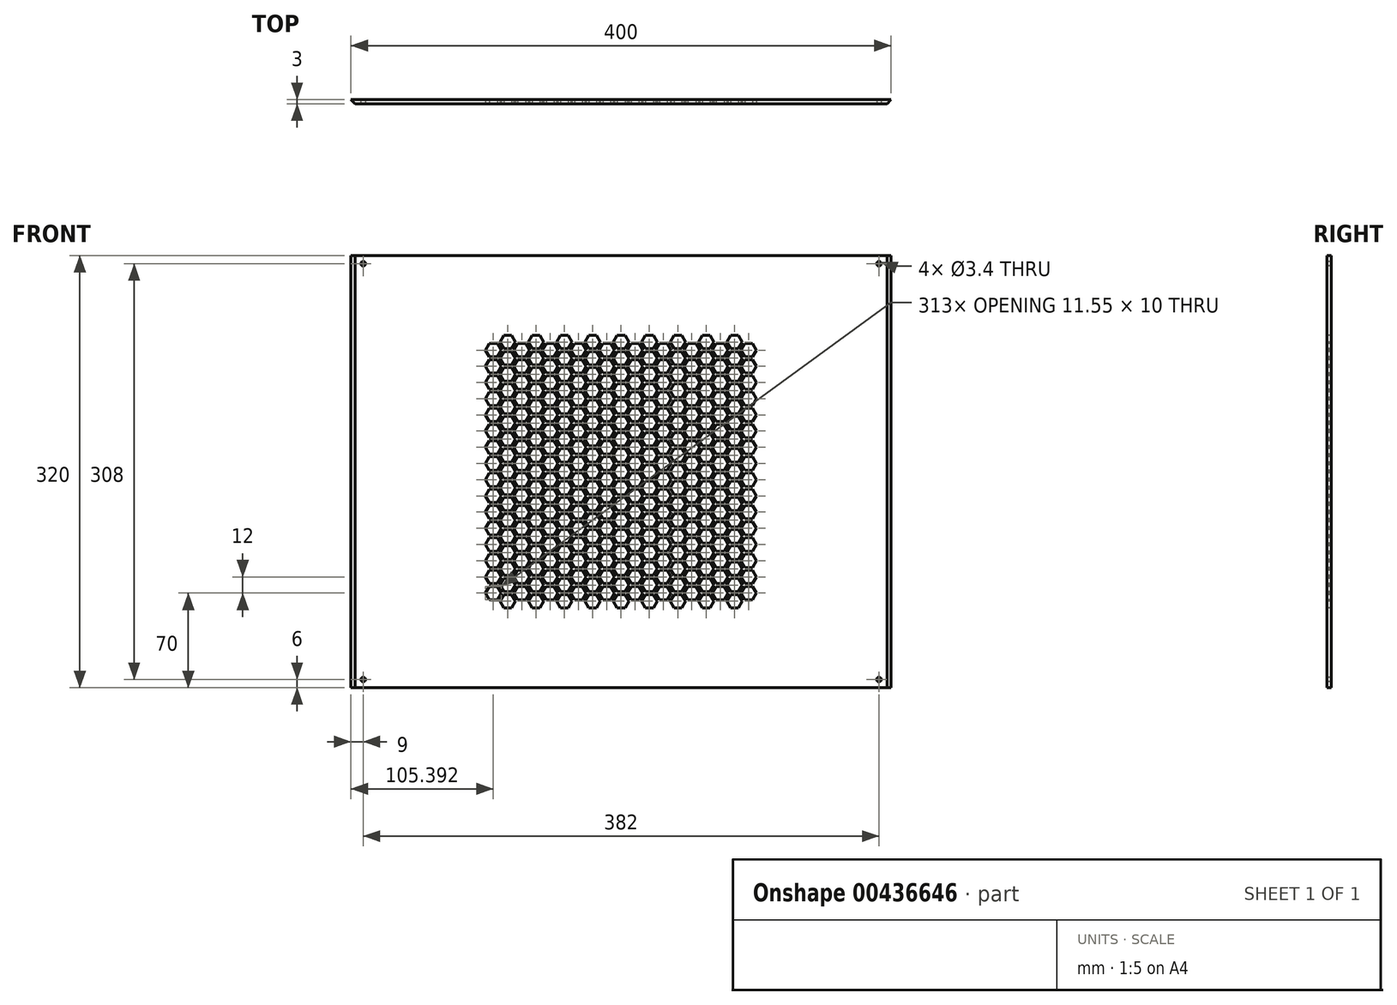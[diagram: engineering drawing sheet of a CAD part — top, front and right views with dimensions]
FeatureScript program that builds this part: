
annotation { "Feature Type Name" : "Feature", "Feature Type Description" : "" }
export const myFeature = defineFeature(function(context is Context, id is Id, definition is map)
    precondition{}
    {
        {
            var Q0;
            Q0=qCreatedBy(makeId("Top.planeOp"),FACE);
            var sketch = newSketch(context, id + "F0", { "sketchPlane" : qUnion([Q0])});
            skLineSegment(sketch, "E0", {"start": v(0, 0) * mm, "end": v(0, 1.5) * mm, "construction": true});
            skLineSegment(sketch, "E1", {"start": v(0, 0) * mm, "end": v(0, -1.5) * mm, "construction": true});
            skLineSegment(sketch, "E2", {"start": v(0, 1.5) * mm, "end": v(-200, 1.5) * mm});
            skLineSegment(sketch, "E3", {"start": v(0, 1.5) * mm, "end": v(200, 1.5) * mm});
            skLineSegment(sketch, "E4", {"start": v(0, -1.5) * mm, "end": v(-197, -1.5) * mm});
            skLineSegment(sketch, "E5", {"start": v(0, -1.5) * mm, "end": v(197, -1.5) * mm});
            skLineSegment(sketch, "E6", {"start": v(-197, -1.5) * mm, "end": v(-200, 1.5) * mm});
            skLineSegment(sketch, "E7", {"start": v(197, -1.5) * mm, "end": v(200, 1.5) * mm});
            skLineSegment(sketch, "E8", {"start": v(0, 0) * mm, "end": v(140, 0) * mm, "construction": true});
            skLineSegment(sketch, "E9", {"start": v(0, 0) * mm, "end": v(-140, 0) * mm, "construction": true});
            skLineSegment(sketch, "E10", {"start": v(140, 0) * mm, "end": v(140, 1.5) * mm});
            skLineSegment(sketch, "E11", {"start": v(140, 0) * mm, "end": v(140, -1.5) * mm});
            skLineSegment(sketch, "E12", {"start": v(-140, 0) * mm, "end": v(-140, 1.5) * mm});
            skLineSegment(sketch, "E13", {"start": v(-140, 0) * mm, "end": v(-140, -1.5) * mm});
            skSolve(sketch);
        }
        {
            var Q0;
            {var subQ8=sQuery(id+"F0.wireOp",EDGE,"E10");Q0=makeQuery(id+"F0.imprint","IMPRINT",FACE,{"disambiguationData":[TD([[makeQuery(id+"F0.imprint","IMPRINT",EDGE,{"derivedFrom":subQ8}),1.0]])]});}
            extrude(context, id + "F1", {"entities" : qUnion([Q0]), "oppositeDirection" : true, "depth" : 320 * mm});
        }
        {
            var Q0;
            {var subQ1=sQuery(id+"F0.wireOp",EDGE,"E6");Q0=makeQuery(id+"F0.imprint","IMPRINT",FACE,{"disambiguationData":[TD([[makeQuery(id+"F0.imprint","IMPRINT",EDGE,{"derivedFrom":subQ1}),-1.0]])]});}
            var Q1;
            {var subQ1=sQuery(id+"F0.wireOp",EDGE,"E7");Q1=makeQuery(id+"F0.imprint","IMPRINT",FACE,{"disambiguationData":[TD([[makeQuery(id+"F0.imprint","IMPRINT",EDGE,{"derivedFrom":subQ1}),1.0]])]});}
            extrude(context, id + "F2", {"entities" : qUnion([Q0, Q1]), "operationType" : NewBodyOperationType.ADD, "oppositeDirection" : true, "depth" : 320 * mm});
        }
        {
            var Q0;
            {var subQ0=sQuery(id+"F0.wireOp",EDGE,"E5");var subQ1=sQuery(id+"F0.wireOp",EDGE,"E4");Q0=makeQuery(id+"F2.boolean.opBoolean","MERGE",FACE,{"derivedFrom":[makeQuery(id+"F1.opExtrude","SWEPT_FACE",FACE,{"disambiguationData":[OSD([subQ1,subQ0])]}),makeQuery(id+"F2.opExtrude","SWEPT_FACE",FACE,{"disambiguationData":[OSD([subQ1])]}),makeQuery(id+"F2.opExtrude","SWEPT_FACE",FACE,{"disambiguationData":[OSD([subQ0])]})]});}
            var sketch = newSketch(context, id + "F3", { "sketchPlane" : qUnion([Q0])});
            skLineSegment(sketch, "E14", {"start": v(0, 0) * mm, "end": v(-191, 0) * mm, "construction": true});
            skLineSegment(sketch, "E15", {"start": v(-191, 0) * mm, "end": v(-191, -6) * mm, "construction": true});
            skCircle(sketch, "E16", {"center": v(-191, -6) * mm, "radius": 1.7 * mm});
            skLineSegment(sketch, "E17", {"start": v(-191, -6) * mm, "end": v(-191, -314) * mm, "construction": true});
            skCircle(sketch, "E18", {"center": v(-191, -314) * mm, "radius": 1.7 * mm});
            skLineSegment(sketch, "E19", {"start": v(0, 0) * mm, "end": v(191, 0) * mm, "construction": true});
            skLineSegment(sketch, "E20", {"start": v(191, 0) * mm, "end": v(191, -6) * mm, "construction": true});
            skLineSegment(sketch, "E21", {"start": v(191, -6) * mm, "end": v(191, -314) * mm, "construction": true});
            skCircle(sketch, "E22", {"center": v(191, -6) * mm, "radius": 1.7 * mm});
            skCircle(sketch, "E23", {"center": v(191, -314) * mm, "radius": 1.7 * mm});
            skSolve(sketch);
        }
        {
            var Q0;
            Q0=makeQuery(id+"F3.imprint","IMPRINT",FACE,{"disambiguationData":[TD([[makeQuery(id+"F3.imprint","IMPRINT",EDGE,{"derivedFrom":sQuery(id+"F3.wireOp",EDGE,"E22")}),1.0]])]});
            var Q1;
            Q1=makeQuery(id+"F3.imprint","IMPRINT",FACE,{"disambiguationData":[TD([[makeQuery(id+"F3.imprint","IMPRINT",EDGE,{"derivedFrom":sQuery(id+"F3.wireOp",EDGE,"E23")}),1.0]])]});
            var Q2;
            Q2=makeQuery(id+"F3.imprint","IMPRINT",FACE,{"disambiguationData":[TD([[makeQuery(id+"F3.imprint","IMPRINT",EDGE,{"derivedFrom":sQuery(id+"F3.wireOp",EDGE,"E18")}),1.0]])]});
            var Q3;
            Q3=makeQuery(id+"F3.imprint","IMPRINT",FACE,{"disambiguationData":[TD([[makeQuery(id+"F3.imprint","IMPRINT",EDGE,{"derivedFrom":sQuery(id+"F3.wireOp",EDGE,"E16")}),1.0]])]});
            extrude(context, id + "F4", {"entities" : qUnion([Q0, Q1, Q2, Q3]), "operationType" : NewBodyOperationType.REMOVE, "oppositeDirection" : true, "depth" : 3 * mm});
        }
        {
            var Q0;
            {var subQ0=sQuery(id+"F0.wireOp",EDGE,"E5");var subQ1=sQuery(id+"F0.wireOp",EDGE,"E4");Q0=makeQuery(id+"F2.boolean.opBoolean","MERGE",FACE,{"derivedFrom":[makeQuery(id+"F1.opExtrude","SWEPT_FACE",FACE,{"disambiguationData":[OSD([subQ1,subQ0])]}),makeQuery(id+"F2.opExtrude","SWEPT_FACE",FACE,{"disambiguationData":[OSD([subQ1])]}),makeQuery(id+"F2.opExtrude","SWEPT_FACE",FACE,{"disambiguationData":[OSD([subQ0])]})]});}
            var sketch = newSketch(context, id + "F5", { "sketchPlane" : qUnion([Q0])});
            skLineSegment(sketch, "E24", {"start": v(0, 0) * mm, "end": v(0, -160) * mm, "construction": true});
            skPoint(sketch, "E24.endSnap0", {"position": v(0, -320) * mm});
            skLineSegment(sketch, "E25.bottom", {"start": v(100, -260) * mm, "end": v(-100, -260) * mm, "construction": true});
            skLineSegment(sketch, "E25.top", {"start": v(100, -60) * mm, "end": v(-100, -60) * mm, "construction": true});
            skLineSegment(sketch, "E25.left", {"start": v(100, -260) * mm, "end": v(100, -60) * mm, "construction": true});
            skLineSegment(sketch, "E25.right", {"start": v(-100, -260) * mm, "end": v(-100, -60) * mm, "construction": true});
            skLineSegment(sketch, "E26", {"start": v(0, 0) * mm, "end": v(84, 0) * mm, "construction": true});
            skLineSegment(sketch, "E27", {"start": v(84, 0) * mm, "end": v(84, -64) * mm, "construction": true});
            skCircle(sketch, "E28.cCircle", {"center": v(84, -64) * mm, "radius": 5 * mm, "construction": true});
            skLineSegment(sketch, "E28.0", {"start": v(81.11, -59) * mm, "end": v(86.89, -59) * mm});
            skLineSegment(sketch, "E28.1", {"start": v(86.89, -59) * mm, "end": v(89.77, -64) * mm});
            skLineSegment(sketch, "E28.2", {"start": v(89.77, -64) * mm, "end": v(86.89, -69) * mm});
            skLineSegment(sketch, "E28.3", {"start": v(86.89, -69) * mm, "end": v(81.11, -69) * mm});
            skLineSegment(sketch, "E28.4", {"start": v(81.11, -69) * mm, "end": v(78.23, -64) * mm});
            skLineSegment(sketch, "E28.5", {"start": v(78.23, -64) * mm, "end": v(81.11, -59) * mm});
            skPoint(sketch, "E28.0.midPoint", {"position": v(84, -59) * mm});
            skLineSegment(sketch, "E29", {"start": v(84, -64) * mm, "end": v(94.4, -70) * mm, "construction": true});
            skCircle(sketch, "E30.cCircle", {"center": v(94.4, -70) * mm, "radius": 5 * mm, "construction": true});
            skLineSegment(sketch, "E30.0", {"start": v(91.5, -65) * mm, "end": v(97.28, -65) * mm});
            skLineSegment(sketch, "E30.1", {"start": v(97.28, -65) * mm, "end": v(100.17, -70) * mm});
            skLineSegment(sketch, "E30.2", {"start": v(100.17, -70) * mm, "end": v(97.28, -75) * mm});
            skLineSegment(sketch, "E30.3", {"start": v(97.28, -75) * mm, "end": v(91.5, -75) * mm});
            skLineSegment(sketch, "E30.4", {"start": v(91.5, -75) * mm, "end": v(88.62, -70) * mm});
            skLineSegment(sketch, "E30.5", {"start": v(88.62, -70) * mm, "end": v(91.5, -65) * mm});
            skPoint(sketch, "E30.0.midPoint", {"position": v(94.4, -65) * mm});
            skLineSegment(sketch, "E31.0.1.0", {"start": v(97.28, -77) * mm, "end": v(100.17, -82) * mm});
            skLineSegment(sketch, "E31.0.1.1", {"start": v(91.5, -87) * mm, "end": v(88.62, -82) * mm});
            skLineSegment(sketch, "E31.0.1.2", {"start": v(88.62, -82) * mm, "end": v(91.5, -77) * mm});
            skLineSegment(sketch, "E31.0.1.3", {"start": v(89.77, -76) * mm, "end": v(86.89, -81) * mm});
            skLineSegment(sketch, "E31.0.1.4", {"start": v(100.17, -82) * mm, "end": v(97.28, -87) * mm});
            skPoint(sketch, "E31.0.1.5", {"position": v(94.4, -77) * mm});
            skLineSegment(sketch, "E31.0.1.6", {"start": v(86.89, -71) * mm, "end": v(89.77, -76) * mm});
            skLineSegment(sketch, "E31.0.1.7", {"start": v(81.11, -71) * mm, "end": v(86.89, -71) * mm});
            skPoint(sketch, "E31.0.1.8", {"position": v(84, -71) * mm});
            skLineSegment(sketch, "E31.0.1.9", {"start": v(86.89, -81) * mm, "end": v(81.11, -81) * mm});
            skLineSegment(sketch, "E31.0.1.10", {"start": v(81.11, -81) * mm, "end": v(78.23, -76) * mm});
            skLineSegment(sketch, "E31.0.1.11", {"start": v(78.23, -76) * mm, "end": v(81.11, -71) * mm});
            skLineSegment(sketch, "E31.0.1.12", {"start": v(91.5, -77) * mm, "end": v(97.28, -77) * mm});
            skLineSegment(sketch, "E31.0.1.13", {"start": v(97.28, -87) * mm, "end": v(91.5, -87) * mm});
            skLineSegment(sketch, "E31.0.2.0", {"start": v(97.28, -89) * mm, "end": v(100.17, -94) * mm});
            skLineSegment(sketch, "E31.0.2.1", {"start": v(91.5, -99) * mm, "end": v(88.62, -94) * mm});
            skLineSegment(sketch, "E31.0.2.2", {"start": v(88.62, -94) * mm, "end": v(91.5, -89) * mm});
            skLineSegment(sketch, "E31.0.2.3", {"start": v(89.77, -88) * mm, "end": v(86.89, -93) * mm});
            skLineSegment(sketch, "E31.0.2.4", {"start": v(100.17, -94) * mm, "end": v(97.28, -99) * mm});
            skPoint(sketch, "E31.0.2.5", {"position": v(94.4, -89) * mm});
            skLineSegment(sketch, "E31.0.2.6", {"start": v(86.89, -83) * mm, "end": v(89.77, -88) * mm});
            skLineSegment(sketch, "E31.0.2.7", {"start": v(81.11, -83) * mm, "end": v(86.89, -83) * mm});
            skPoint(sketch, "E31.0.2.8", {"position": v(84, -83) * mm});
            skLineSegment(sketch, "E31.0.2.9", {"start": v(86.89, -93) * mm, "end": v(81.11, -93) * mm});
            skLineSegment(sketch, "E31.0.2.10", {"start": v(81.11, -93) * mm, "end": v(78.23, -88) * mm});
            skLineSegment(sketch, "E31.0.2.11", {"start": v(78.23, -88) * mm, "end": v(81.11, -83) * mm});
            skLineSegment(sketch, "E31.0.2.12", {"start": v(91.5, -89) * mm, "end": v(97.28, -89) * mm});
            skLineSegment(sketch, "E31.0.2.13", {"start": v(97.28, -99) * mm, "end": v(91.5, -99) * mm});
            skLineSegment(sketch, "E31.0.3.0", {"start": v(97.28, -101) * mm, "end": v(100.17, -106) * mm});
            skLineSegment(sketch, "E31.0.3.1", {"start": v(91.5, -111) * mm, "end": v(88.62, -106) * mm});
            skLineSegment(sketch, "E31.0.3.2", {"start": v(88.62, -106) * mm, "end": v(91.5, -101) * mm});
            skLineSegment(sketch, "E31.0.3.3", {"start": v(89.77, -100) * mm, "end": v(86.89, -105) * mm});
            skLineSegment(sketch, "E31.0.3.4", {"start": v(100.17, -106) * mm, "end": v(97.28, -111) * mm});
            skPoint(sketch, "E31.0.3.5", {"position": v(94.4, -101) * mm});
            skLineSegment(sketch, "E31.0.3.6", {"start": v(86.89, -95) * mm, "end": v(89.77, -100) * mm});
            skLineSegment(sketch, "E31.0.3.7", {"start": v(81.11, -95) * mm, "end": v(86.89, -95) * mm});
            skPoint(sketch, "E31.0.3.8", {"position": v(84, -95) * mm});
            skLineSegment(sketch, "E31.0.3.9", {"start": v(86.89, -105) * mm, "end": v(81.11, -105) * mm});
            skLineSegment(sketch, "E31.0.3.10", {"start": v(81.11, -105) * mm, "end": v(78.23, -100) * mm});
            skLineSegment(sketch, "E31.0.3.11", {"start": v(78.23, -100) * mm, "end": v(81.11, -95) * mm});
            skLineSegment(sketch, "E31.0.3.12", {"start": v(91.5, -101) * mm, "end": v(97.28, -101) * mm});
            skLineSegment(sketch, "E31.0.3.13", {"start": v(97.28, -111) * mm, "end": v(91.5, -111) * mm});
            skLineSegment(sketch, "E31.0.4.0", {"start": v(97.28, -113) * mm, "end": v(100.17, -118) * mm});
            skLineSegment(sketch, "E31.0.4.1", {"start": v(91.5, -123) * mm, "end": v(88.62, -118) * mm});
            skLineSegment(sketch, "E31.0.4.2", {"start": v(88.62, -118) * mm, "end": v(91.5, -113) * mm});
            skLineSegment(sketch, "E31.0.4.3", {"start": v(89.77, -112) * mm, "end": v(86.89, -117) * mm});
            skLineSegment(sketch, "E31.0.4.4", {"start": v(100.17, -118) * mm, "end": v(97.28, -123) * mm});
            skPoint(sketch, "E31.0.4.5", {"position": v(94.4, -113) * mm});
            skLineSegment(sketch, "E31.0.4.6", {"start": v(86.89, -107) * mm, "end": v(89.77, -112) * mm});
            skLineSegment(sketch, "E31.0.4.7", {"start": v(81.11, -107) * mm, "end": v(86.89, -107) * mm});
            skPoint(sketch, "E31.0.4.8", {"position": v(84, -107) * mm});
            skLineSegment(sketch, "E31.0.4.9", {"start": v(86.89, -117) * mm, "end": v(81.11, -117) * mm});
            skLineSegment(sketch, "E31.0.4.10", {"start": v(81.11, -117) * mm, "end": v(78.23, -112) * mm});
            skLineSegment(sketch, "E31.0.4.11", {"start": v(78.23, -112) * mm, "end": v(81.11, -107) * mm});
            skLineSegment(sketch, "E31.0.4.12", {"start": v(91.5, -113) * mm, "end": v(97.28, -113) * mm});
            skLineSegment(sketch, "E31.0.4.13", {"start": v(97.28, -123) * mm, "end": v(91.5, -123) * mm});
            skLineSegment(sketch, "E31.0.5.0", {"start": v(97.28, -125) * mm, "end": v(100.17, -130) * mm});
            skLineSegment(sketch, "E31.0.5.1", {"start": v(91.5, -135) * mm, "end": v(88.62, -130) * mm});
            skLineSegment(sketch, "E31.0.5.2", {"start": v(88.62, -130) * mm, "end": v(91.5, -125) * mm});
            skLineSegment(sketch, "E31.0.5.3", {"start": v(89.77, -124) * mm, "end": v(86.89, -129) * mm});
            skLineSegment(sketch, "E31.0.5.4", {"start": v(100.17, -130) * mm, "end": v(97.28, -135) * mm});
            skPoint(sketch, "E31.0.5.5", {"position": v(94.4, -125) * mm});
            skLineSegment(sketch, "E31.0.5.6", {"start": v(86.89, -119) * mm, "end": v(89.77, -124) * mm});
            skLineSegment(sketch, "E31.0.5.7", {"start": v(81.11, -119) * mm, "end": v(86.89, -119) * mm});
            skPoint(sketch, "E31.0.5.8", {"position": v(84, -119) * mm});
            skLineSegment(sketch, "E31.0.5.9", {"start": v(86.89, -129) * mm, "end": v(81.11, -129) * mm});
            skLineSegment(sketch, "E31.0.5.10", {"start": v(81.11, -129) * mm, "end": v(78.23, -124) * mm});
            skLineSegment(sketch, "E31.0.5.11", {"start": v(78.23, -124) * mm, "end": v(81.11, -119) * mm});
            skLineSegment(sketch, "E31.0.5.12", {"start": v(91.5, -125) * mm, "end": v(97.28, -125) * mm});
            skLineSegment(sketch, "E31.0.5.13", {"start": v(97.28, -135) * mm, "end": v(91.5, -135) * mm});
            skLineSegment(sketch, "E31.0.6.0", {"start": v(97.28, -137) * mm, "end": v(100.17, -142) * mm});
            skLineSegment(sketch, "E31.0.6.1", {"start": v(91.5, -147) * mm, "end": v(88.62, -142) * mm});
            skLineSegment(sketch, "E31.0.6.2", {"start": v(88.62, -142) * mm, "end": v(91.5, -137) * mm});
            skLineSegment(sketch, "E31.0.6.3", {"start": v(89.77, -136) * mm, "end": v(86.89, -141) * mm});
            skLineSegment(sketch, "E31.0.6.4", {"start": v(100.17, -142) * mm, "end": v(97.28, -147) * mm});
            skPoint(sketch, "E31.0.6.5", {"position": v(94.4, -137) * mm});
            skLineSegment(sketch, "E31.0.6.6", {"start": v(86.89, -131) * mm, "end": v(89.77, -136) * mm});
            skLineSegment(sketch, "E31.0.6.7", {"start": v(81.11, -131) * mm, "end": v(86.89, -131) * mm});
            skPoint(sketch, "E31.0.6.8", {"position": v(84, -131) * mm});
            skLineSegment(sketch, "E31.0.6.9", {"start": v(86.89, -141) * mm, "end": v(81.11, -141) * mm});
            skLineSegment(sketch, "E31.0.6.10", {"start": v(81.11, -141) * mm, "end": v(78.23, -136) * mm});
            skLineSegment(sketch, "E31.0.6.11", {"start": v(78.23, -136) * mm, "end": v(81.11, -131) * mm});
            skLineSegment(sketch, "E31.0.6.12", {"start": v(91.5, -137) * mm, "end": v(97.28, -137) * mm});
            skLineSegment(sketch, "E31.0.6.13", {"start": v(97.28, -147) * mm, "end": v(91.5, -147) * mm});
            skLineSegment(sketch, "E31.0.7.0", {"start": v(97.28, -149) * mm, "end": v(100.17, -154) * mm});
            skLineSegment(sketch, "E31.0.7.1", {"start": v(91.5, -159) * mm, "end": v(88.62, -154) * mm});
            skLineSegment(sketch, "E31.0.7.2", {"start": v(88.62, -154) * mm, "end": v(91.5, -149) * mm});
            skLineSegment(sketch, "E31.0.7.3", {"start": v(89.77, -148) * mm, "end": v(86.89, -153) * mm});
            skLineSegment(sketch, "E31.0.7.4", {"start": v(100.17, -154) * mm, "end": v(97.28, -159) * mm});
            skPoint(sketch, "E31.0.7.5", {"position": v(94.4, -149) * mm});
            skLineSegment(sketch, "E31.0.7.6", {"start": v(86.89, -143) * mm, "end": v(89.77, -148) * mm});
            skLineSegment(sketch, "E31.0.7.7", {"start": v(81.11, -143) * mm, "end": v(86.89, -143) * mm});
            skPoint(sketch, "E31.0.7.8", {"position": v(84, -143) * mm});
            skLineSegment(sketch, "E31.0.7.9", {"start": v(86.89, -153) * mm, "end": v(81.11, -153) * mm});
            skLineSegment(sketch, "E31.0.7.10", {"start": v(81.11, -153) * mm, "end": v(78.23, -148) * mm});
            skLineSegment(sketch, "E31.0.7.11", {"start": v(78.23, -148) * mm, "end": v(81.11, -143) * mm});
            skLineSegment(sketch, "E31.0.7.12", {"start": v(91.5, -149) * mm, "end": v(97.28, -149) * mm});
            skLineSegment(sketch, "E31.0.7.13", {"start": v(97.28, -159) * mm, "end": v(91.5, -159) * mm});
            skLineSegment(sketch, "E31.0.8.0", {"start": v(97.28, -161) * mm, "end": v(100.17, -166) * mm});
            skLineSegment(sketch, "E31.0.8.1", {"start": v(91.5, -171) * mm, "end": v(88.62, -166) * mm});
            skLineSegment(sketch, "E31.0.8.2", {"start": v(88.62, -166) * mm, "end": v(91.5, -161) * mm});
            skLineSegment(sketch, "E31.0.8.3", {"start": v(89.77, -160) * mm, "end": v(86.89, -165) * mm});
            skLineSegment(sketch, "E31.0.8.4", {"start": v(100.17, -166) * mm, "end": v(97.28, -171) * mm});
            skPoint(sketch, "E31.0.8.5", {"position": v(94.4, -161) * mm});
            skLineSegment(sketch, "E31.0.8.6", {"start": v(86.89, -155) * mm, "end": v(89.77, -160) * mm});
            skLineSegment(sketch, "E31.0.8.7", {"start": v(81.11, -155) * mm, "end": v(86.89, -155) * mm});
            skPoint(sketch, "E31.0.8.8", {"position": v(84, -155) * mm});
            skLineSegment(sketch, "E31.0.8.9", {"start": v(86.89, -165) * mm, "end": v(81.11, -165) * mm});
            skLineSegment(sketch, "E31.0.8.10", {"start": v(81.11, -165) * mm, "end": v(78.23, -160) * mm});
            skLineSegment(sketch, "E31.0.8.11", {"start": v(78.23, -160) * mm, "end": v(81.11, -155) * mm});
            skLineSegment(sketch, "E31.0.8.12", {"start": v(91.5, -161) * mm, "end": v(97.28, -161) * mm});
            skLineSegment(sketch, "E31.0.8.13", {"start": v(97.28, -171) * mm, "end": v(91.5, -171) * mm});
            skLineSegment(sketch, "E31.0.9.0", {"start": v(97.28, -173) * mm, "end": v(100.17, -178) * mm});
            skLineSegment(sketch, "E31.0.9.1", {"start": v(91.5, -183) * mm, "end": v(88.62, -178) * mm});
            skLineSegment(sketch, "E31.0.9.2", {"start": v(88.62, -178) * mm, "end": v(91.5, -173) * mm});
            skLineSegment(sketch, "E31.0.9.3", {"start": v(89.77, -172) * mm, "end": v(86.89, -177) * mm});
            skLineSegment(sketch, "E31.0.9.4", {"start": v(100.17, -178) * mm, "end": v(97.28, -183) * mm});
            skPoint(sketch, "E31.0.9.5", {"position": v(94.4, -173) * mm});
            skLineSegment(sketch, "E31.0.9.6", {"start": v(86.89, -167) * mm, "end": v(89.77, -172) * mm});
            skLineSegment(sketch, "E31.0.9.7", {"start": v(81.11, -167) * mm, "end": v(86.89, -167) * mm});
            skPoint(sketch, "E31.0.9.8", {"position": v(84, -167) * mm});
            skLineSegment(sketch, "E31.0.9.9", {"start": v(86.89, -177) * mm, "end": v(81.11, -177) * mm});
            skLineSegment(sketch, "E31.0.9.10", {"start": v(81.11, -177) * mm, "end": v(78.23, -172) * mm});
            skLineSegment(sketch, "E31.0.9.11", {"start": v(78.23, -172) * mm, "end": v(81.11, -167) * mm});
            skLineSegment(sketch, "E31.0.9.12", {"start": v(91.5, -173) * mm, "end": v(97.28, -173) * mm});
            skLineSegment(sketch, "E31.0.9.13", {"start": v(97.28, -183) * mm, "end": v(91.5, -183) * mm});
            skLineSegment(sketch, "E31.0.10.0", {"start": v(97.28, -185) * mm, "end": v(100.17, -190) * mm});
            skLineSegment(sketch, "E31.0.10.1", {"start": v(91.5, -195) * mm, "end": v(88.62, -190) * mm});
            skLineSegment(sketch, "E31.0.10.2", {"start": v(88.62, -190) * mm, "end": v(91.5, -185) * mm});
            skLineSegment(sketch, "E31.0.10.3", {"start": v(89.77, -184) * mm, "end": v(86.89, -189) * mm});
            skLineSegment(sketch, "E31.0.10.4", {"start": v(100.17, -190) * mm, "end": v(97.28, -195) * mm});
            skPoint(sketch, "E31.0.10.5", {"position": v(94.4, -185) * mm});
            skLineSegment(sketch, "E31.0.10.6", {"start": v(86.89, -179) * mm, "end": v(89.77, -184) * mm});
            skLineSegment(sketch, "E31.0.10.7", {"start": v(81.11, -179) * mm, "end": v(86.89, -179) * mm});
            skPoint(sketch, "E31.0.10.8", {"position": v(84, -179) * mm});
            skLineSegment(sketch, "E31.0.10.9", {"start": v(86.89, -189) * mm, "end": v(81.11, -189) * mm});
            skLineSegment(sketch, "E31.0.10.10", {"start": v(81.11, -189) * mm, "end": v(78.23, -184) * mm});
            skLineSegment(sketch, "E31.0.10.11", {"start": v(78.23, -184) * mm, "end": v(81.11, -179) * mm});
            skLineSegment(sketch, "E31.0.10.12", {"start": v(91.5, -185) * mm, "end": v(97.28, -185) * mm});
            skLineSegment(sketch, "E31.0.10.13", {"start": v(97.28, -195) * mm, "end": v(91.5, -195) * mm});
            skLineSegment(sketch, "E31.0.11.0", {"start": v(97.28, -197) * mm, "end": v(100.17, -202) * mm});
            skLineSegment(sketch, "E31.0.11.1", {"start": v(91.5, -207) * mm, "end": v(88.62, -202) * mm});
            skLineSegment(sketch, "E31.0.11.2", {"start": v(88.62, -202) * mm, "end": v(91.5, -197) * mm});
            skLineSegment(sketch, "E31.0.11.3", {"start": v(89.77, -196) * mm, "end": v(86.89, -201) * mm});
            skLineSegment(sketch, "E31.0.11.4", {"start": v(100.17, -202) * mm, "end": v(97.28, -207) * mm});
            skPoint(sketch, "E31.0.11.5", {"position": v(94.4, -197) * mm});
            skLineSegment(sketch, "E31.0.11.6", {"start": v(86.89, -191) * mm, "end": v(89.77, -196) * mm});
            skLineSegment(sketch, "E31.0.11.7", {"start": v(81.11, -191) * mm, "end": v(86.89, -191) * mm});
            skPoint(sketch, "E31.0.11.8", {"position": v(84, -191) * mm});
            skLineSegment(sketch, "E31.0.11.9", {"start": v(86.89, -201) * mm, "end": v(81.11, -201) * mm});
            skLineSegment(sketch, "E31.0.11.10", {"start": v(81.11, -201) * mm, "end": v(78.23, -196) * mm});
            skLineSegment(sketch, "E31.0.11.11", {"start": v(78.23, -196) * mm, "end": v(81.11, -191) * mm});
            skLineSegment(sketch, "E31.0.11.12", {"start": v(91.5, -197) * mm, "end": v(97.28, -197) * mm});
            skLineSegment(sketch, "E31.0.11.13", {"start": v(97.28, -207) * mm, "end": v(91.5, -207) * mm});
            skLineSegment(sketch, "E31.0.12.0", {"start": v(97.28, -209) * mm, "end": v(100.17, -214) * mm});
            skLineSegment(sketch, "E31.0.12.1", {"start": v(91.5, -219) * mm, "end": v(88.62, -214) * mm});
            skLineSegment(sketch, "E31.0.12.2", {"start": v(88.62, -214) * mm, "end": v(91.5, -209) * mm});
            skLineSegment(sketch, "E31.0.12.3", {"start": v(89.77, -208) * mm, "end": v(86.89, -213) * mm});
            skLineSegment(sketch, "E31.0.12.4", {"start": v(100.17, -214) * mm, "end": v(97.28, -219) * mm});
            skPoint(sketch, "E31.0.12.5", {"position": v(94.4, -209) * mm});
            skLineSegment(sketch, "E31.0.12.6", {"start": v(86.89, -203) * mm, "end": v(89.77, -208) * mm});
            skLineSegment(sketch, "E31.0.12.7", {"start": v(81.11, -203) * mm, "end": v(86.89, -203) * mm});
            skPoint(sketch, "E31.0.12.8", {"position": v(84, -203) * mm});
            skLineSegment(sketch, "E31.0.12.9", {"start": v(86.89, -213) * mm, "end": v(81.11, -213) * mm});
            skLineSegment(sketch, "E31.0.12.10", {"start": v(81.11, -213) * mm, "end": v(78.23, -208) * mm});
            skLineSegment(sketch, "E31.0.12.11", {"start": v(78.23, -208) * mm, "end": v(81.11, -203) * mm});
            skLineSegment(sketch, "E31.0.12.12", {"start": v(91.5, -209) * mm, "end": v(97.28, -209) * mm});
            skLineSegment(sketch, "E31.0.12.13", {"start": v(97.28, -219) * mm, "end": v(91.5, -219) * mm});
            skLineSegment(sketch, "E31.0.13.0", {"start": v(97.28, -221) * mm, "end": v(100.17, -226) * mm});
            skLineSegment(sketch, "E31.0.13.1", {"start": v(91.5, -231) * mm, "end": v(88.62, -226) * mm});
            skLineSegment(sketch, "E31.0.13.2", {"start": v(88.62, -226) * mm, "end": v(91.5, -221) * mm});
            skLineSegment(sketch, "E31.0.13.3", {"start": v(89.77, -220) * mm, "end": v(86.89, -225) * mm});
            skLineSegment(sketch, "E31.0.13.4", {"start": v(100.17, -226) * mm, "end": v(97.28, -231) * mm});
            skPoint(sketch, "E31.0.13.5", {"position": v(94.4, -221) * mm});
            skLineSegment(sketch, "E31.0.13.6", {"start": v(86.89, -215) * mm, "end": v(89.77, -220) * mm});
            skLineSegment(sketch, "E31.0.13.7", {"start": v(81.11, -215) * mm, "end": v(86.89, -215) * mm});
            skPoint(sketch, "E31.0.13.8", {"position": v(84, -215) * mm});
            skLineSegment(sketch, "E31.0.13.9", {"start": v(86.89, -225) * mm, "end": v(81.11, -225) * mm});
            skLineSegment(sketch, "E31.0.13.10", {"start": v(81.11, -225) * mm, "end": v(78.23, -220) * mm});
            skLineSegment(sketch, "E31.0.13.11", {"start": v(78.23, -220) * mm, "end": v(81.11, -215) * mm});
            skLineSegment(sketch, "E31.0.13.12", {"start": v(91.5, -221) * mm, "end": v(97.28, -221) * mm});
            skLineSegment(sketch, "E31.0.13.13", {"start": v(97.28, -231) * mm, "end": v(91.5, -231) * mm});
            skLineSegment(sketch, "E31.0.14.0", {"start": v(97.28, -233) * mm, "end": v(100.17, -238) * mm});
            skLineSegment(sketch, "E31.0.14.1", {"start": v(91.5, -243) * mm, "end": v(88.62, -238) * mm});
            skLineSegment(sketch, "E31.0.14.2", {"start": v(88.62, -238) * mm, "end": v(91.5, -233) * mm});
            skLineSegment(sketch, "E31.0.14.3", {"start": v(89.77, -232) * mm, "end": v(86.89, -237) * mm});
            skLineSegment(sketch, "E31.0.14.4", {"start": v(100.17, -238) * mm, "end": v(97.28, -243) * mm});
            skPoint(sketch, "E31.0.14.5", {"position": v(94.4, -233) * mm});
            skLineSegment(sketch, "E31.0.14.6", {"start": v(86.89, -227) * mm, "end": v(89.77, -232) * mm});
            skLineSegment(sketch, "E31.0.14.7", {"start": v(81.11, -227) * mm, "end": v(86.89, -227) * mm});
            skPoint(sketch, "E31.0.14.8", {"position": v(84, -227) * mm});
            skLineSegment(sketch, "E31.0.14.9", {"start": v(86.89, -237) * mm, "end": v(81.11, -237) * mm});
            skLineSegment(sketch, "E31.0.14.10", {"start": v(81.11, -237) * mm, "end": v(78.23, -232) * mm});
            skLineSegment(sketch, "E31.0.14.11", {"start": v(78.23, -232) * mm, "end": v(81.11, -227) * mm});
            skLineSegment(sketch, "E31.0.14.12", {"start": v(91.5, -233) * mm, "end": v(97.28, -233) * mm});
            skLineSegment(sketch, "E31.0.14.13", {"start": v(97.28, -243) * mm, "end": v(91.5, -243) * mm});
            skLineSegment(sketch, "E31.0.15.0", {"start": v(97.28, -245) * mm, "end": v(100.17, -250) * mm});
            skLineSegment(sketch, "E31.0.15.1", {"start": v(91.5, -255) * mm, "end": v(88.62, -250) * mm});
            skLineSegment(sketch, "E31.0.15.2", {"start": v(88.62, -250) * mm, "end": v(91.5, -245) * mm});
            skLineSegment(sketch, "E31.0.15.3", {"start": v(89.77, -244) * mm, "end": v(86.89, -249) * mm});
            skLineSegment(sketch, "E31.0.15.4", {"start": v(100.17, -250) * mm, "end": v(97.28, -255) * mm});
            skPoint(sketch, "E31.0.15.5", {"position": v(94.4, -245) * mm});
            skLineSegment(sketch, "E31.0.15.6", {"start": v(86.89, -239) * mm, "end": v(89.77, -244) * mm});
            skLineSegment(sketch, "E31.0.15.7", {"start": v(81.11, -239) * mm, "end": v(86.89, -239) * mm});
            skPoint(sketch, "E31.0.15.8", {"position": v(84, -239) * mm});
            skLineSegment(sketch, "E31.0.15.9", {"start": v(86.89, -249) * mm, "end": v(81.11, -249) * mm});
            skLineSegment(sketch, "E31.0.15.10", {"start": v(81.11, -249) * mm, "end": v(78.23, -244) * mm});
            skLineSegment(sketch, "E31.0.15.11", {"start": v(78.23, -244) * mm, "end": v(81.11, -239) * mm});
            skLineSegment(sketch, "E31.0.15.12", {"start": v(91.5, -245) * mm, "end": v(97.28, -245) * mm});
            skLineSegment(sketch, "E31.0.15.13", {"start": v(97.28, -255) * mm, "end": v(91.5, -255) * mm});
            skLineSegment(sketch, "E31.0.16.3", {"start": v(89.77, -256) * mm, "end": v(86.89, -261) * mm});
            skLineSegment(sketch, "E31.0.16.6", {"start": v(86.89, -251) * mm, "end": v(89.77, -256) * mm});
            skLineSegment(sketch, "E31.0.16.7", {"start": v(81.11, -251) * mm, "end": v(86.89, -251) * mm});
            skPoint(sketch, "E31.0.16.8", {"position": v(84, -251) * mm});
            skLineSegment(sketch, "E31.0.16.9", {"start": v(86.89, -261) * mm, "end": v(81.11, -261) * mm});
            skLineSegment(sketch, "E31.0.16.10", {"start": v(81.11, -261) * mm, "end": v(78.23, -256) * mm});
            skLineSegment(sketch, "E31.0.16.11", {"start": v(78.23, -256) * mm, "end": v(81.11, -251) * mm});
            skLineSegment(sketch, "E31.1.0.0", {"start": v(76.28, -65) * mm, "end": v(79.17, -70) * mm});
            skLineSegment(sketch, "E31.1.0.1", {"start": v(70.5, -75) * mm, "end": v(67.62, -70) * mm});
            skLineSegment(sketch, "E31.1.0.2", {"start": v(67.62, -70) * mm, "end": v(70.5, -65) * mm});
            skLineSegment(sketch, "E31.1.0.3", {"start": v(68.77, -64) * mm, "end": v(65.89, -69) * mm});
            skLineSegment(sketch, "E31.1.0.4", {"start": v(79.17, -70) * mm, "end": v(76.28, -75) * mm});
            skPoint(sketch, "E31.1.0.5", {"position": v(73.4, -65) * mm});
            skLineSegment(sketch, "E31.1.0.6", {"start": v(65.89, -59) * mm, "end": v(68.77, -64) * mm});
            skLineSegment(sketch, "E31.1.0.7", {"start": v(60.11, -59) * mm, "end": v(65.89, -59) * mm});
            skPoint(sketch, "E31.1.0.8", {"position": v(63, -59) * mm});
            skLineSegment(sketch, "E31.1.0.9", {"start": v(65.89, -69) * mm, "end": v(60.11, -69) * mm});
            skLineSegment(sketch, "E31.1.0.10", {"start": v(60.11, -69) * mm, "end": v(57.23, -64) * mm});
            skLineSegment(sketch, "E31.1.0.11", {"start": v(57.23, -64) * mm, "end": v(60.11, -59) * mm});
            skLineSegment(sketch, "E31.1.0.12", {"start": v(70.5, -65) * mm, "end": v(76.28, -65) * mm});
            skLineSegment(sketch, "E31.1.0.13", {"start": v(76.28, -75) * mm, "end": v(70.5, -75) * mm});
            skLineSegment(sketch, "E31.1.1.0", {"start": v(76.28, -77) * mm, "end": v(79.17, -82) * mm});
            skLineSegment(sketch, "E31.1.1.1", {"start": v(70.5, -87) * mm, "end": v(67.62, -82) * mm});
            skLineSegment(sketch, "E31.1.1.2", {"start": v(67.62, -82) * mm, "end": v(70.5, -77) * mm});
            skLineSegment(sketch, "E31.1.1.3", {"start": v(68.77, -76) * mm, "end": v(65.89, -81) * mm});
            skLineSegment(sketch, "E31.1.1.4", {"start": v(79.17, -82) * mm, "end": v(76.28, -87) * mm});
            skPoint(sketch, "E31.1.1.5", {"position": v(73.4, -77) * mm});
            skLineSegment(sketch, "E31.1.1.6", {"start": v(65.89, -71) * mm, "end": v(68.77, -76) * mm});
            skLineSegment(sketch, "E31.1.1.7", {"start": v(60.11, -71) * mm, "end": v(65.89, -71) * mm});
            skPoint(sketch, "E31.1.1.8", {"position": v(63, -71) * mm});
            skLineSegment(sketch, "E31.1.1.9", {"start": v(65.89, -81) * mm, "end": v(60.11, -81) * mm});
            skLineSegment(sketch, "E31.1.1.10", {"start": v(60.11, -81) * mm, "end": v(57.23, -76) * mm});
            skLineSegment(sketch, "E31.1.1.11", {"start": v(57.23, -76) * mm, "end": v(60.11, -71) * mm});
            skLineSegment(sketch, "E31.1.1.12", {"start": v(70.5, -77) * mm, "end": v(76.28, -77) * mm});
            skLineSegment(sketch, "E31.1.1.13", {"start": v(76.28, -87) * mm, "end": v(70.5, -87) * mm});
            skLineSegment(sketch, "E31.1.2.0", {"start": v(76.28, -89) * mm, "end": v(79.17, -94) * mm});
            skLineSegment(sketch, "E31.1.2.1", {"start": v(70.5, -99) * mm, "end": v(67.62, -94) * mm});
            skLineSegment(sketch, "E31.1.2.2", {"start": v(67.62, -94) * mm, "end": v(70.5, -89) * mm});
            skLineSegment(sketch, "E31.1.2.3", {"start": v(68.77, -88) * mm, "end": v(65.89, -93) * mm});
            skLineSegment(sketch, "E31.1.2.4", {"start": v(79.17, -94) * mm, "end": v(76.28, -99) * mm});
            skPoint(sketch, "E31.1.2.5", {"position": v(73.4, -89) * mm});
            skLineSegment(sketch, "E31.1.2.6", {"start": v(65.89, -83) * mm, "end": v(68.77, -88) * mm});
            skLineSegment(sketch, "E31.1.2.7", {"start": v(60.11, -83) * mm, "end": v(65.89, -83) * mm});
            skPoint(sketch, "E31.1.2.8", {"position": v(63, -83) * mm});
            skLineSegment(sketch, "E31.1.2.9", {"start": v(65.89, -93) * mm, "end": v(60.11, -93) * mm});
            skLineSegment(sketch, "E31.1.2.10", {"start": v(60.11, -93) * mm, "end": v(57.23, -88) * mm});
            skLineSegment(sketch, "E31.1.2.11", {"start": v(57.23, -88) * mm, "end": v(60.11, -83) * mm});
            skLineSegment(sketch, "E31.1.2.12", {"start": v(70.5, -89) * mm, "end": v(76.28, -89) * mm});
            skLineSegment(sketch, "E31.1.2.13", {"start": v(76.28, -99) * mm, "end": v(70.5, -99) * mm});
            skLineSegment(sketch, "E31.1.3.0", {"start": v(76.28, -101) * mm, "end": v(79.17, -106) * mm});
            skLineSegment(sketch, "E31.1.3.1", {"start": v(70.5, -111) * mm, "end": v(67.62, -106) * mm});
            skLineSegment(sketch, "E31.1.3.2", {"start": v(67.62, -106) * mm, "end": v(70.5, -101) * mm});
            skLineSegment(sketch, "E31.1.3.3", {"start": v(68.77, -100) * mm, "end": v(65.89, -105) * mm});
            skLineSegment(sketch, "E31.1.3.4", {"start": v(79.17, -106) * mm, "end": v(76.28, -111) * mm});
            skPoint(sketch, "E31.1.3.5", {"position": v(73.4, -101) * mm});
            skLineSegment(sketch, "E31.1.3.6", {"start": v(65.89, -95) * mm, "end": v(68.77, -100) * mm});
            skLineSegment(sketch, "E31.1.3.7", {"start": v(60.11, -95) * mm, "end": v(65.89, -95) * mm});
            skPoint(sketch, "E31.1.3.8", {"position": v(63, -95) * mm});
            skLineSegment(sketch, "E31.1.3.9", {"start": v(65.89, -105) * mm, "end": v(60.11, -105) * mm});
            skLineSegment(sketch, "E31.1.3.10", {"start": v(60.11, -105) * mm, "end": v(57.23, -100) * mm});
            skLineSegment(sketch, "E31.1.3.11", {"start": v(57.23, -100) * mm, "end": v(60.11, -95) * mm});
            skLineSegment(sketch, "E31.1.3.12", {"start": v(70.5, -101) * mm, "end": v(76.28, -101) * mm});
            skLineSegment(sketch, "E31.1.3.13", {"start": v(76.28, -111) * mm, "end": v(70.5, -111) * mm});
            skLineSegment(sketch, "E31.1.4.0", {"start": v(76.28, -113) * mm, "end": v(79.17, -118) * mm});
            skLineSegment(sketch, "E31.1.4.1", {"start": v(70.5, -123) * mm, "end": v(67.62, -118) * mm});
            skLineSegment(sketch, "E31.1.4.2", {"start": v(67.62, -118) * mm, "end": v(70.5, -113) * mm});
            skLineSegment(sketch, "E31.1.4.3", {"start": v(68.77, -112) * mm, "end": v(65.89, -117) * mm});
            skLineSegment(sketch, "E31.1.4.4", {"start": v(79.17, -118) * mm, "end": v(76.28, -123) * mm});
            skPoint(sketch, "E31.1.4.5", {"position": v(73.4, -113) * mm});
            skLineSegment(sketch, "E31.1.4.6", {"start": v(65.89, -107) * mm, "end": v(68.77, -112) * mm});
            skLineSegment(sketch, "E31.1.4.7", {"start": v(60.11, -107) * mm, "end": v(65.89, -107) * mm});
            skPoint(sketch, "E31.1.4.8", {"position": v(63, -107) * mm});
            skLineSegment(sketch, "E31.1.4.9", {"start": v(65.89, -117) * mm, "end": v(60.11, -117) * mm});
            skLineSegment(sketch, "E31.1.4.10", {"start": v(60.11, -117) * mm, "end": v(57.23, -112) * mm});
            skLineSegment(sketch, "E31.1.4.11", {"start": v(57.23, -112) * mm, "end": v(60.11, -107) * mm});
            skLineSegment(sketch, "E31.1.4.12", {"start": v(70.5, -113) * mm, "end": v(76.28, -113) * mm});
            skLineSegment(sketch, "E31.1.4.13", {"start": v(76.28, -123) * mm, "end": v(70.5, -123) * mm});
            skLineSegment(sketch, "E31.1.5.0", {"start": v(76.28, -125) * mm, "end": v(79.17, -130) * mm});
            skLineSegment(sketch, "E31.1.5.1", {"start": v(70.5, -135) * mm, "end": v(67.62, -130) * mm});
            skLineSegment(sketch, "E31.1.5.2", {"start": v(67.62, -130) * mm, "end": v(70.5, -125) * mm});
            skLineSegment(sketch, "E31.1.5.3", {"start": v(68.77, -124) * mm, "end": v(65.89, -129) * mm});
            skLineSegment(sketch, "E31.1.5.4", {"start": v(79.17, -130) * mm, "end": v(76.28, -135) * mm});
            skPoint(sketch, "E31.1.5.5", {"position": v(73.4, -125) * mm});
            skLineSegment(sketch, "E31.1.5.6", {"start": v(65.89, -119) * mm, "end": v(68.77, -124) * mm});
            skLineSegment(sketch, "E31.1.5.7", {"start": v(60.11, -119) * mm, "end": v(65.89, -119) * mm});
            skPoint(sketch, "E31.1.5.8", {"position": v(63, -119) * mm});
            skLineSegment(sketch, "E31.1.5.9", {"start": v(65.89, -129) * mm, "end": v(60.11, -129) * mm});
            skLineSegment(sketch, "E31.1.5.10", {"start": v(60.11, -129) * mm, "end": v(57.23, -124) * mm});
            skLineSegment(sketch, "E31.1.5.11", {"start": v(57.23, -124) * mm, "end": v(60.11, -119) * mm});
            skLineSegment(sketch, "E31.1.5.12", {"start": v(70.5, -125) * mm, "end": v(76.28, -125) * mm});
            skLineSegment(sketch, "E31.1.5.13", {"start": v(76.28, -135) * mm, "end": v(70.5, -135) * mm});
            skLineSegment(sketch, "E31.1.6.0", {"start": v(76.28, -137) * mm, "end": v(79.17, -142) * mm});
            skLineSegment(sketch, "E31.1.6.1", {"start": v(70.5, -147) * mm, "end": v(67.62, -142) * mm});
            skLineSegment(sketch, "E31.1.6.2", {"start": v(67.62, -142) * mm, "end": v(70.5, -137) * mm});
            skLineSegment(sketch, "E31.1.6.3", {"start": v(68.77, -136) * mm, "end": v(65.89, -141) * mm});
            skLineSegment(sketch, "E31.1.6.4", {"start": v(79.17, -142) * mm, "end": v(76.28, -147) * mm});
            skPoint(sketch, "E31.1.6.5", {"position": v(73.4, -137) * mm});
            skLineSegment(sketch, "E31.1.6.6", {"start": v(65.89, -131) * mm, "end": v(68.77, -136) * mm});
            skLineSegment(sketch, "E31.1.6.7", {"start": v(60.11, -131) * mm, "end": v(65.89, -131) * mm});
            skPoint(sketch, "E31.1.6.8", {"position": v(63, -131) * mm});
            skLineSegment(sketch, "E31.1.6.9", {"start": v(65.89, -141) * mm, "end": v(60.11, -141) * mm});
            skLineSegment(sketch, "E31.1.6.10", {"start": v(60.11, -141) * mm, "end": v(57.23, -136) * mm});
            skLineSegment(sketch, "E31.1.6.11", {"start": v(57.23, -136) * mm, "end": v(60.11, -131) * mm});
            skLineSegment(sketch, "E31.1.6.12", {"start": v(70.5, -137) * mm, "end": v(76.28, -137) * mm});
            skLineSegment(sketch, "E31.1.6.13", {"start": v(76.28, -147) * mm, "end": v(70.5, -147) * mm});
            skLineSegment(sketch, "E31.1.7.0", {"start": v(76.28, -149) * mm, "end": v(79.17, -154) * mm});
            skLineSegment(sketch, "E31.1.7.1", {"start": v(70.5, -159) * mm, "end": v(67.62, -154) * mm});
            skLineSegment(sketch, "E31.1.7.2", {"start": v(67.62, -154) * mm, "end": v(70.5, -149) * mm});
            skLineSegment(sketch, "E31.1.7.3", {"start": v(68.77, -148) * mm, "end": v(65.89, -153) * mm});
            skLineSegment(sketch, "E31.1.7.4", {"start": v(79.17, -154) * mm, "end": v(76.28, -159) * mm});
            skPoint(sketch, "E31.1.7.5", {"position": v(73.4, -149) * mm});
            skLineSegment(sketch, "E31.1.7.6", {"start": v(65.89, -143) * mm, "end": v(68.77, -148) * mm});
            skLineSegment(sketch, "E31.1.7.7", {"start": v(60.11, -143) * mm, "end": v(65.89, -143) * mm});
            skPoint(sketch, "E31.1.7.8", {"position": v(63, -143) * mm});
            skLineSegment(sketch, "E31.1.7.9", {"start": v(65.89, -153) * mm, "end": v(60.11, -153) * mm});
            skLineSegment(sketch, "E31.1.7.10", {"start": v(60.11, -153) * mm, "end": v(57.23, -148) * mm});
            skLineSegment(sketch, "E31.1.7.11", {"start": v(57.23, -148) * mm, "end": v(60.11, -143) * mm});
            skLineSegment(sketch, "E31.1.7.12", {"start": v(70.5, -149) * mm, "end": v(76.28, -149) * mm});
            skLineSegment(sketch, "E31.1.7.13", {"start": v(76.28, -159) * mm, "end": v(70.5, -159) * mm});
            skLineSegment(sketch, "E31.1.8.0", {"start": v(76.28, -161) * mm, "end": v(79.17, -166) * mm});
            skLineSegment(sketch, "E31.1.8.1", {"start": v(70.5, -171) * mm, "end": v(67.62, -166) * mm});
            skLineSegment(sketch, "E31.1.8.2", {"start": v(67.62, -166) * mm, "end": v(70.5, -161) * mm});
            skLineSegment(sketch, "E31.1.8.3", {"start": v(68.77, -160) * mm, "end": v(65.89, -165) * mm});
            skLineSegment(sketch, "E31.1.8.4", {"start": v(79.17, -166) * mm, "end": v(76.28, -171) * mm});
            skPoint(sketch, "E31.1.8.5", {"position": v(73.4, -161) * mm});
            skLineSegment(sketch, "E31.1.8.6", {"start": v(65.89, -155) * mm, "end": v(68.77, -160) * mm});
            skLineSegment(sketch, "E31.1.8.7", {"start": v(60.11, -155) * mm, "end": v(65.89, -155) * mm});
            skPoint(sketch, "E31.1.8.8", {"position": v(63, -155) * mm});
            skLineSegment(sketch, "E31.1.8.9", {"start": v(65.89, -165) * mm, "end": v(60.11, -165) * mm});
            skLineSegment(sketch, "E31.1.8.10", {"start": v(60.11, -165) * mm, "end": v(57.23, -160) * mm});
            skLineSegment(sketch, "E31.1.8.11", {"start": v(57.23, -160) * mm, "end": v(60.11, -155) * mm});
            skLineSegment(sketch, "E31.1.8.12", {"start": v(70.5, -161) * mm, "end": v(76.28, -161) * mm});
            skLineSegment(sketch, "E31.1.8.13", {"start": v(76.28, -171) * mm, "end": v(70.5, -171) * mm});
            skLineSegment(sketch, "E31.1.9.0", {"start": v(76.28, -173) * mm, "end": v(79.17, -178) * mm});
            skLineSegment(sketch, "E31.1.9.1", {"start": v(70.5, -183) * mm, "end": v(67.62, -178) * mm});
            skLineSegment(sketch, "E31.1.9.2", {"start": v(67.62, -178) * mm, "end": v(70.5, -173) * mm});
            skLineSegment(sketch, "E31.1.9.3", {"start": v(68.77, -172) * mm, "end": v(65.89, -177) * mm});
            skLineSegment(sketch, "E31.1.9.4", {"start": v(79.17, -178) * mm, "end": v(76.28, -183) * mm});
            skPoint(sketch, "E31.1.9.5", {"position": v(73.4, -173) * mm});
            skLineSegment(sketch, "E31.1.9.6", {"start": v(65.89, -167) * mm, "end": v(68.77, -172) * mm});
            skLineSegment(sketch, "E31.1.9.7", {"start": v(60.11, -167) * mm, "end": v(65.89, -167) * mm});
            skPoint(sketch, "E31.1.9.8", {"position": v(63, -167) * mm});
            skLineSegment(sketch, "E31.1.9.9", {"start": v(65.89, -177) * mm, "end": v(60.11, -177) * mm});
            skLineSegment(sketch, "E31.1.9.10", {"start": v(60.11, -177) * mm, "end": v(57.23, -172) * mm});
            skLineSegment(sketch, "E31.1.9.11", {"start": v(57.23, -172) * mm, "end": v(60.11, -167) * mm});
            skLineSegment(sketch, "E31.1.9.12", {"start": v(70.5, -173) * mm, "end": v(76.28, -173) * mm});
            skLineSegment(sketch, "E31.1.9.13", {"start": v(76.28, -183) * mm, "end": v(70.5, -183) * mm});
            skLineSegment(sketch, "E31.1.10.0", {"start": v(76.28, -185) * mm, "end": v(79.17, -190) * mm});
            skLineSegment(sketch, "E31.1.10.1", {"start": v(70.5, -195) * mm, "end": v(67.62, -190) * mm});
            skLineSegment(sketch, "E31.1.10.2", {"start": v(67.62, -190) * mm, "end": v(70.5, -185) * mm});
            skLineSegment(sketch, "E31.1.10.3", {"start": v(68.77, -184) * mm, "end": v(65.89, -189) * mm});
            skLineSegment(sketch, "E31.1.10.4", {"start": v(79.17, -190) * mm, "end": v(76.28, -195) * mm});
            skPoint(sketch, "E31.1.10.5", {"position": v(73.4, -185) * mm});
            skLineSegment(sketch, "E31.1.10.6", {"start": v(65.89, -179) * mm, "end": v(68.77, -184) * mm});
            skLineSegment(sketch, "E31.1.10.7", {"start": v(60.11, -179) * mm, "end": v(65.89, -179) * mm});
            skPoint(sketch, "E31.1.10.8", {"position": v(63, -179) * mm});
            skLineSegment(sketch, "E31.1.10.9", {"start": v(65.89, -189) * mm, "end": v(60.11, -189) * mm});
            skLineSegment(sketch, "E31.1.10.10", {"start": v(60.11, -189) * mm, "end": v(57.23, -184) * mm});
            skLineSegment(sketch, "E31.1.10.11", {"start": v(57.23, -184) * mm, "end": v(60.11, -179) * mm});
            skLineSegment(sketch, "E31.1.10.12", {"start": v(70.5, -185) * mm, "end": v(76.28, -185) * mm});
            skLineSegment(sketch, "E31.1.10.13", {"start": v(76.28, -195) * mm, "end": v(70.5, -195) * mm});
            skLineSegment(sketch, "E31.1.11.0", {"start": v(76.28, -197) * mm, "end": v(79.17, -202) * mm});
            skLineSegment(sketch, "E31.1.11.1", {"start": v(70.5, -207) * mm, "end": v(67.62, -202) * mm});
            skLineSegment(sketch, "E31.1.11.2", {"start": v(67.62, -202) * mm, "end": v(70.5, -197) * mm});
            skLineSegment(sketch, "E31.1.11.3", {"start": v(68.77, -196) * mm, "end": v(65.89, -201) * mm});
            skLineSegment(sketch, "E31.1.11.4", {"start": v(79.17, -202) * mm, "end": v(76.28, -207) * mm});
            skPoint(sketch, "E31.1.11.5", {"position": v(73.4, -197) * mm});
            skLineSegment(sketch, "E31.1.11.6", {"start": v(65.89, -191) * mm, "end": v(68.77, -196) * mm});
            skLineSegment(sketch, "E31.1.11.7", {"start": v(60.11, -191) * mm, "end": v(65.89, -191) * mm});
            skPoint(sketch, "E31.1.11.8", {"position": v(63, -191) * mm});
            skLineSegment(sketch, "E31.1.11.9", {"start": v(65.89, -201) * mm, "end": v(60.11, -201) * mm});
            skLineSegment(sketch, "E31.1.11.10", {"start": v(60.11, -201) * mm, "end": v(57.23, -196) * mm});
            skLineSegment(sketch, "E31.1.11.11", {"start": v(57.23, -196) * mm, "end": v(60.11, -191) * mm});
            skLineSegment(sketch, "E31.1.11.12", {"start": v(70.5, -197) * mm, "end": v(76.28, -197) * mm});
            skLineSegment(sketch, "E31.1.11.13", {"start": v(76.28, -207) * mm, "end": v(70.5, -207) * mm});
            skLineSegment(sketch, "E31.1.12.0", {"start": v(76.28, -209) * mm, "end": v(79.17, -214) * mm});
            skLineSegment(sketch, "E31.1.12.1", {"start": v(70.5, -219) * mm, "end": v(67.62, -214) * mm});
            skLineSegment(sketch, "E31.1.12.2", {"start": v(67.62, -214) * mm, "end": v(70.5, -209) * mm});
            skLineSegment(sketch, "E31.1.12.3", {"start": v(68.77, -208) * mm, "end": v(65.89, -213) * mm});
            skLineSegment(sketch, "E31.1.12.4", {"start": v(79.17, -214) * mm, "end": v(76.28, -219) * mm});
            skPoint(sketch, "E31.1.12.5", {"position": v(73.4, -209) * mm});
            skLineSegment(sketch, "E31.1.12.6", {"start": v(65.89, -203) * mm, "end": v(68.77, -208) * mm});
            skLineSegment(sketch, "E31.1.12.7", {"start": v(60.11, -203) * mm, "end": v(65.89, -203) * mm});
            skPoint(sketch, "E31.1.12.8", {"position": v(63, -203) * mm});
            skLineSegment(sketch, "E31.1.12.9", {"start": v(65.89, -213) * mm, "end": v(60.11, -213) * mm});
            skLineSegment(sketch, "E31.1.12.10", {"start": v(60.11, -213) * mm, "end": v(57.23, -208) * mm});
            skLineSegment(sketch, "E31.1.12.11", {"start": v(57.23, -208) * mm, "end": v(60.11, -203) * mm});
            skLineSegment(sketch, "E31.1.12.12", {"start": v(70.5, -209) * mm, "end": v(76.28, -209) * mm});
            skLineSegment(sketch, "E31.1.12.13", {"start": v(76.28, -219) * mm, "end": v(70.5, -219) * mm});
            skLineSegment(sketch, "E31.1.13.0", {"start": v(76.28, -221) * mm, "end": v(79.17, -226) * mm});
            skLineSegment(sketch, "E31.1.13.1", {"start": v(70.5, -231) * mm, "end": v(67.62, -226) * mm});
            skLineSegment(sketch, "E31.1.13.2", {"start": v(67.62, -226) * mm, "end": v(70.5, -221) * mm});
            skLineSegment(sketch, "E31.1.13.3", {"start": v(68.77, -220) * mm, "end": v(65.89, -225) * mm});
            skLineSegment(sketch, "E31.1.13.4", {"start": v(79.17, -226) * mm, "end": v(76.28, -231) * mm});
            skPoint(sketch, "E31.1.13.5", {"position": v(73.4, -221) * mm});
            skLineSegment(sketch, "E31.1.13.6", {"start": v(65.89, -215) * mm, "end": v(68.77, -220) * mm});
            skLineSegment(sketch, "E31.1.13.7", {"start": v(60.11, -215) * mm, "end": v(65.89, -215) * mm});
            skPoint(sketch, "E31.1.13.8", {"position": v(63, -215) * mm});
            skLineSegment(sketch, "E31.1.13.9", {"start": v(65.89, -225) * mm, "end": v(60.11, -225) * mm});
            skLineSegment(sketch, "E31.1.13.10", {"start": v(60.11, -225) * mm, "end": v(57.23, -220) * mm});
            skLineSegment(sketch, "E31.1.13.11", {"start": v(57.23, -220) * mm, "end": v(60.11, -215) * mm});
            skLineSegment(sketch, "E31.1.13.12", {"start": v(70.5, -221) * mm, "end": v(76.28, -221) * mm});
            skLineSegment(sketch, "E31.1.13.13", {"start": v(76.28, -231) * mm, "end": v(70.5, -231) * mm});
            skLineSegment(sketch, "E31.1.14.0", {"start": v(76.28, -233) * mm, "end": v(79.17, -238) * mm});
            skLineSegment(sketch, "E31.1.14.1", {"start": v(70.5, -243) * mm, "end": v(67.62, -238) * mm});
            skLineSegment(sketch, "E31.1.14.2", {"start": v(67.62, -238) * mm, "end": v(70.5, -233) * mm});
            skLineSegment(sketch, "E31.1.14.3", {"start": v(68.77, -232) * mm, "end": v(65.89, -237) * mm});
            skLineSegment(sketch, "E31.1.14.4", {"start": v(79.17, -238) * mm, "end": v(76.28, -243) * mm});
            skPoint(sketch, "E31.1.14.5", {"position": v(73.4, -233) * mm});
            skLineSegment(sketch, "E31.1.14.6", {"start": v(65.89, -227) * mm, "end": v(68.77, -232) * mm});
            skLineSegment(sketch, "E31.1.14.7", {"start": v(60.11, -227) * mm, "end": v(65.89, -227) * mm});
            skPoint(sketch, "E31.1.14.8", {"position": v(63, -227) * mm});
            skLineSegment(sketch, "E31.1.14.9", {"start": v(65.89, -237) * mm, "end": v(60.11, -237) * mm});
            skLineSegment(sketch, "E31.1.14.10", {"start": v(60.11, -237) * mm, "end": v(57.23, -232) * mm});
            skLineSegment(sketch, "E31.1.14.11", {"start": v(57.23, -232) * mm, "end": v(60.11, -227) * mm});
            skLineSegment(sketch, "E31.1.14.12", {"start": v(70.5, -233) * mm, "end": v(76.28, -233) * mm});
            skLineSegment(sketch, "E31.1.14.13", {"start": v(76.28, -243) * mm, "end": v(70.5, -243) * mm});
            skLineSegment(sketch, "E31.1.15.0", {"start": v(76.28, -245) * mm, "end": v(79.17, -250) * mm});
            skLineSegment(sketch, "E31.1.15.1", {"start": v(70.5, -255) * mm, "end": v(67.62, -250) * mm});
            skLineSegment(sketch, "E31.1.15.2", {"start": v(67.62, -250) * mm, "end": v(70.5, -245) * mm});
            skLineSegment(sketch, "E31.1.15.3", {"start": v(68.77, -244) * mm, "end": v(65.89, -249) * mm});
            skLineSegment(sketch, "E31.1.15.4", {"start": v(79.17, -250) * mm, "end": v(76.28, -255) * mm});
            skPoint(sketch, "E31.1.15.5", {"position": v(73.4, -245) * mm});
            skLineSegment(sketch, "E31.1.15.6", {"start": v(65.89, -239) * mm, "end": v(68.77, -244) * mm});
            skLineSegment(sketch, "E31.1.15.7", {"start": v(60.11, -239) * mm, "end": v(65.89, -239) * mm});
            skPoint(sketch, "E31.1.15.8", {"position": v(63, -239) * mm});
            skLineSegment(sketch, "E31.1.15.9", {"start": v(65.89, -249) * mm, "end": v(60.11, -249) * mm});
            skLineSegment(sketch, "E31.1.15.10", {"start": v(60.11, -249) * mm, "end": v(57.23, -244) * mm});
            skLineSegment(sketch, "E31.1.15.11", {"start": v(57.23, -244) * mm, "end": v(60.11, -239) * mm});
            skLineSegment(sketch, "E31.1.15.12", {"start": v(70.5, -245) * mm, "end": v(76.28, -245) * mm});
            skLineSegment(sketch, "E31.1.15.13", {"start": v(76.28, -255) * mm, "end": v(70.5, -255) * mm});
            skLineSegment(sketch, "E31.1.16.3", {"start": v(68.77, -256) * mm, "end": v(65.89, -261) * mm});
            skLineSegment(sketch, "E31.1.16.6", {"start": v(65.89, -251) * mm, "end": v(68.77, -256) * mm});
            skLineSegment(sketch, "E31.1.16.7", {"start": v(60.11, -251) * mm, "end": v(65.89, -251) * mm});
            skPoint(sketch, "E31.1.16.8", {"position": v(63, -251) * mm});
            skLineSegment(sketch, "E31.1.16.9", {"start": v(65.89, -261) * mm, "end": v(60.11, -261) * mm});
            skLineSegment(sketch, "E31.1.16.10", {"start": v(60.11, -261) * mm, "end": v(57.23, -256) * mm});
            skLineSegment(sketch, "E31.1.16.11", {"start": v(57.23, -256) * mm, "end": v(60.11, -251) * mm});
            skLineSegment(sketch, "E31.2.0.0", {"start": v(55.28, -65) * mm, "end": v(58.17, -70) * mm});
            skLineSegment(sketch, "E31.2.0.1", {"start": v(49.5, -75) * mm, "end": v(46.62, -70) * mm});
            skLineSegment(sketch, "E31.2.0.2", {"start": v(46.62, -70) * mm, "end": v(49.5, -65) * mm});
            skLineSegment(sketch, "E31.2.0.3", {"start": v(47.77, -64) * mm, "end": v(44.89, -69) * mm});
            skLineSegment(sketch, "E31.2.0.4", {"start": v(58.17, -70) * mm, "end": v(55.28, -75) * mm});
            skPoint(sketch, "E31.2.0.5", {"position": v(52.4, -65) * mm});
            skLineSegment(sketch, "E31.2.0.6", {"start": v(44.89, -59) * mm, "end": v(47.77, -64) * mm});
            skLineSegment(sketch, "E31.2.0.7", {"start": v(39.11, -59) * mm, "end": v(44.89, -59) * mm});
            skPoint(sketch, "E31.2.0.8", {"position": v(42, -59) * mm});
            skLineSegment(sketch, "E31.2.0.9", {"start": v(44.89, -69) * mm, "end": v(39.11, -69) * mm});
            skLineSegment(sketch, "E31.2.0.10", {"start": v(39.11, -69) * mm, "end": v(36.23, -64) * mm});
            skLineSegment(sketch, "E31.2.0.11", {"start": v(36.23, -64) * mm, "end": v(39.11, -59) * mm});
            skLineSegment(sketch, "E31.2.0.12", {"start": v(49.5, -65) * mm, "end": v(55.28, -65) * mm});
            skLineSegment(sketch, "E31.2.0.13", {"start": v(55.28, -75) * mm, "end": v(49.5, -75) * mm});
            skLineSegment(sketch, "E31.2.1.0", {"start": v(55.28, -77) * mm, "end": v(58.17, -82) * mm});
            skLineSegment(sketch, "E31.2.1.1", {"start": v(49.5, -87) * mm, "end": v(46.62, -82) * mm});
            skLineSegment(sketch, "E31.2.1.2", {"start": v(46.62, -82) * mm, "end": v(49.5, -77) * mm});
            skLineSegment(sketch, "E31.2.1.3", {"start": v(47.77, -76) * mm, "end": v(44.89, -81) * mm});
            skLineSegment(sketch, "E31.2.1.4", {"start": v(58.17, -82) * mm, "end": v(55.28, -87) * mm});
            skPoint(sketch, "E31.2.1.5", {"position": v(52.4, -77) * mm});
            skLineSegment(sketch, "E31.2.1.6", {"start": v(44.89, -71) * mm, "end": v(47.77, -76) * mm});
            skLineSegment(sketch, "E31.2.1.7", {"start": v(39.11, -71) * mm, "end": v(44.89, -71) * mm});
            skPoint(sketch, "E31.2.1.8", {"position": v(42, -71) * mm});
            skLineSegment(sketch, "E31.2.1.9", {"start": v(44.89, -81) * mm, "end": v(39.11, -81) * mm});
            skLineSegment(sketch, "E31.2.1.10", {"start": v(39.11, -81) * mm, "end": v(36.23, -76) * mm});
            skLineSegment(sketch, "E31.2.1.11", {"start": v(36.23, -76) * mm, "end": v(39.11, -71) * mm});
            skLineSegment(sketch, "E31.2.1.12", {"start": v(49.5, -77) * mm, "end": v(55.28, -77) * mm});
            skLineSegment(sketch, "E31.2.1.13", {"start": v(55.28, -87) * mm, "end": v(49.5, -87) * mm});
            skLineSegment(sketch, "E31.2.2.0", {"start": v(55.28, -89) * mm, "end": v(58.17, -94) * mm});
            skLineSegment(sketch, "E31.2.2.1", {"start": v(49.5, -99) * mm, "end": v(46.62, -94) * mm});
            skLineSegment(sketch, "E31.2.2.2", {"start": v(46.62, -94) * mm, "end": v(49.5, -89) * mm});
            skLineSegment(sketch, "E31.2.2.3", {"start": v(47.77, -88) * mm, "end": v(44.89, -93) * mm});
            skLineSegment(sketch, "E31.2.2.4", {"start": v(58.17, -94) * mm, "end": v(55.28, -99) * mm});
            skPoint(sketch, "E31.2.2.5", {"position": v(52.4, -89) * mm});
            skLineSegment(sketch, "E31.2.2.6", {"start": v(44.89, -83) * mm, "end": v(47.77, -88) * mm});
            skLineSegment(sketch, "E31.2.2.7", {"start": v(39.11, -83) * mm, "end": v(44.89, -83) * mm});
            skPoint(sketch, "E31.2.2.8", {"position": v(42, -83) * mm});
            skLineSegment(sketch, "E31.2.2.9", {"start": v(44.89, -93) * mm, "end": v(39.11, -93) * mm});
            skLineSegment(sketch, "E31.2.2.10", {"start": v(39.11, -93) * mm, "end": v(36.23, -88) * mm});
            skLineSegment(sketch, "E31.2.2.11", {"start": v(36.23, -88) * mm, "end": v(39.11, -83) * mm});
            skLineSegment(sketch, "E31.2.2.12", {"start": v(49.5, -89) * mm, "end": v(55.28, -89) * mm});
            skLineSegment(sketch, "E31.2.2.13", {"start": v(55.28, -99) * mm, "end": v(49.5, -99) * mm});
            skLineSegment(sketch, "E31.2.3.0", {"start": v(55.28, -101) * mm, "end": v(58.17, -106) * mm});
            skLineSegment(sketch, "E31.2.3.1", {"start": v(49.5, -111) * mm, "end": v(46.62, -106) * mm});
            skLineSegment(sketch, "E31.2.3.2", {"start": v(46.62, -106) * mm, "end": v(49.5, -101) * mm});
            skLineSegment(sketch, "E31.2.3.3", {"start": v(47.77, -100) * mm, "end": v(44.89, -105) * mm});
            skLineSegment(sketch, "E31.2.3.4", {"start": v(58.17, -106) * mm, "end": v(55.28, -111) * mm});
            skPoint(sketch, "E31.2.3.5", {"position": v(52.4, -101) * mm});
            skLineSegment(sketch, "E31.2.3.6", {"start": v(44.89, -95) * mm, "end": v(47.77, -100) * mm});
            skLineSegment(sketch, "E31.2.3.7", {"start": v(39.11, -95) * mm, "end": v(44.89, -95) * mm});
            skPoint(sketch, "E31.2.3.8", {"position": v(42, -95) * mm});
            skLineSegment(sketch, "E31.2.3.9", {"start": v(44.89, -105) * mm, "end": v(39.11, -105) * mm});
            skLineSegment(sketch, "E31.2.3.10", {"start": v(39.11, -105) * mm, "end": v(36.23, -100) * mm});
            skLineSegment(sketch, "E31.2.3.11", {"start": v(36.23, -100) * mm, "end": v(39.11, -95) * mm});
            skLineSegment(sketch, "E31.2.3.12", {"start": v(49.5, -101) * mm, "end": v(55.28, -101) * mm});
            skLineSegment(sketch, "E31.2.3.13", {"start": v(55.28, -111) * mm, "end": v(49.5, -111) * mm});
            skLineSegment(sketch, "E31.2.4.0", {"start": v(55.28, -113) * mm, "end": v(58.17, -118) * mm});
            skLineSegment(sketch, "E31.2.4.1", {"start": v(49.5, -123) * mm, "end": v(46.62, -118) * mm});
            skLineSegment(sketch, "E31.2.4.2", {"start": v(46.62, -118) * mm, "end": v(49.5, -113) * mm});
            skLineSegment(sketch, "E31.2.4.3", {"start": v(47.77, -112) * mm, "end": v(44.89, -117) * mm});
            skLineSegment(sketch, "E31.2.4.4", {"start": v(58.17, -118) * mm, "end": v(55.28, -123) * mm});
            skPoint(sketch, "E31.2.4.5", {"position": v(52.4, -113) * mm});
            skLineSegment(sketch, "E31.2.4.6", {"start": v(44.89, -107) * mm, "end": v(47.77, -112) * mm});
            skLineSegment(sketch, "E31.2.4.7", {"start": v(39.11, -107) * mm, "end": v(44.89, -107) * mm});
            skPoint(sketch, "E31.2.4.8", {"position": v(42, -107) * mm});
            skLineSegment(sketch, "E31.2.4.9", {"start": v(44.89, -117) * mm, "end": v(39.11, -117) * mm});
            skLineSegment(sketch, "E31.2.4.10", {"start": v(39.11, -117) * mm, "end": v(36.23, -112) * mm});
            skLineSegment(sketch, "E31.2.4.11", {"start": v(36.23, -112) * mm, "end": v(39.11, -107) * mm});
            skLineSegment(sketch, "E31.2.4.12", {"start": v(49.5, -113) * mm, "end": v(55.28, -113) * mm});
            skLineSegment(sketch, "E31.2.4.13", {"start": v(55.28, -123) * mm, "end": v(49.5, -123) * mm});
            skLineSegment(sketch, "E31.2.5.0", {"start": v(55.28, -125) * mm, "end": v(58.17, -130) * mm});
            skLineSegment(sketch, "E31.2.5.1", {"start": v(49.5, -135) * mm, "end": v(46.62, -130) * mm});
            skLineSegment(sketch, "E31.2.5.2", {"start": v(46.62, -130) * mm, "end": v(49.5, -125) * mm});
            skLineSegment(sketch, "E31.2.5.3", {"start": v(47.77, -124) * mm, "end": v(44.89, -129) * mm});
            skLineSegment(sketch, "E31.2.5.4", {"start": v(58.17, -130) * mm, "end": v(55.28, -135) * mm});
            skPoint(sketch, "E31.2.5.5", {"position": v(52.4, -125) * mm});
            skLineSegment(sketch, "E31.2.5.6", {"start": v(44.89, -119) * mm, "end": v(47.77, -124) * mm});
            skLineSegment(sketch, "E31.2.5.7", {"start": v(39.11, -119) * mm, "end": v(44.89, -119) * mm});
            skPoint(sketch, "E31.2.5.8", {"position": v(42, -119) * mm});
            skLineSegment(sketch, "E31.2.5.9", {"start": v(44.89, -129) * mm, "end": v(39.11, -129) * mm});
            skLineSegment(sketch, "E31.2.5.10", {"start": v(39.11, -129) * mm, "end": v(36.23, -124) * mm});
            skLineSegment(sketch, "E31.2.5.11", {"start": v(36.23, -124) * mm, "end": v(39.11, -119) * mm});
            skLineSegment(sketch, "E31.2.5.12", {"start": v(49.5, -125) * mm, "end": v(55.28, -125) * mm});
            skLineSegment(sketch, "E31.2.5.13", {"start": v(55.28, -135) * mm, "end": v(49.5, -135) * mm});
            skLineSegment(sketch, "E31.2.6.0", {"start": v(55.28, -137) * mm, "end": v(58.17, -142) * mm});
            skLineSegment(sketch, "E31.2.6.1", {"start": v(49.5, -147) * mm, "end": v(46.62, -142) * mm});
            skLineSegment(sketch, "E31.2.6.2", {"start": v(46.62, -142) * mm, "end": v(49.5, -137) * mm});
            skLineSegment(sketch, "E31.2.6.3", {"start": v(47.77, -136) * mm, "end": v(44.89, -141) * mm});
            skLineSegment(sketch, "E31.2.6.4", {"start": v(58.17, -142) * mm, "end": v(55.28, -147) * mm});
            skPoint(sketch, "E31.2.6.5", {"position": v(52.4, -137) * mm});
            skLineSegment(sketch, "E31.2.6.6", {"start": v(44.89, -131) * mm, "end": v(47.77, -136) * mm});
            skLineSegment(sketch, "E31.2.6.7", {"start": v(39.11, -131) * mm, "end": v(44.89, -131) * mm});
            skPoint(sketch, "E31.2.6.8", {"position": v(42, -131) * mm});
            skLineSegment(sketch, "E31.2.6.9", {"start": v(44.89, -141) * mm, "end": v(39.11, -141) * mm});
            skLineSegment(sketch, "E31.2.6.10", {"start": v(39.11, -141) * mm, "end": v(36.23, -136) * mm});
            skLineSegment(sketch, "E31.2.6.11", {"start": v(36.23, -136) * mm, "end": v(39.11, -131) * mm});
            skLineSegment(sketch, "E31.2.6.12", {"start": v(49.5, -137) * mm, "end": v(55.28, -137) * mm});
            skLineSegment(sketch, "E31.2.6.13", {"start": v(55.28, -147) * mm, "end": v(49.5, -147) * mm});
            skLineSegment(sketch, "E31.2.7.0", {"start": v(55.28, -149) * mm, "end": v(58.17, -154) * mm});
            skLineSegment(sketch, "E31.2.7.1", {"start": v(49.5, -159) * mm, "end": v(46.62, -154) * mm});
            skLineSegment(sketch, "E31.2.7.2", {"start": v(46.62, -154) * mm, "end": v(49.5, -149) * mm});
            skLineSegment(sketch, "E31.2.7.3", {"start": v(47.77, -148) * mm, "end": v(44.89, -153) * mm});
            skLineSegment(sketch, "E31.2.7.4", {"start": v(58.17, -154) * mm, "end": v(55.28, -159) * mm});
            skPoint(sketch, "E31.2.7.5", {"position": v(52.4, -149) * mm});
            skLineSegment(sketch, "E31.2.7.6", {"start": v(44.89, -143) * mm, "end": v(47.77, -148) * mm});
            skLineSegment(sketch, "E31.2.7.7", {"start": v(39.11, -143) * mm, "end": v(44.89, -143) * mm});
            skPoint(sketch, "E31.2.7.8", {"position": v(42, -143) * mm});
            skLineSegment(sketch, "E31.2.7.9", {"start": v(44.89, -153) * mm, "end": v(39.11, -153) * mm});
            skLineSegment(sketch, "E31.2.7.10", {"start": v(39.11, -153) * mm, "end": v(36.23, -148) * mm});
            skLineSegment(sketch, "E31.2.7.11", {"start": v(36.23, -148) * mm, "end": v(39.11, -143) * mm});
            skLineSegment(sketch, "E31.2.7.12", {"start": v(49.5, -149) * mm, "end": v(55.28, -149) * mm});
            skLineSegment(sketch, "E31.2.7.13", {"start": v(55.28, -159) * mm, "end": v(49.5, -159) * mm});
            skLineSegment(sketch, "E31.2.8.0", {"start": v(55.28, -161) * mm, "end": v(58.17, -166) * mm});
            skLineSegment(sketch, "E31.2.8.1", {"start": v(49.5, -171) * mm, "end": v(46.62, -166) * mm});
            skLineSegment(sketch, "E31.2.8.2", {"start": v(46.62, -166) * mm, "end": v(49.5, -161) * mm});
            skLineSegment(sketch, "E31.2.8.3", {"start": v(47.77, -160) * mm, "end": v(44.89, -165) * mm});
            skLineSegment(sketch, "E31.2.8.4", {"start": v(58.17, -166) * mm, "end": v(55.28, -171) * mm});
            skPoint(sketch, "E31.2.8.5", {"position": v(52.4, -161) * mm});
            skLineSegment(sketch, "E31.2.8.6", {"start": v(44.89, -155) * mm, "end": v(47.77, -160) * mm});
            skLineSegment(sketch, "E31.2.8.7", {"start": v(39.11, -155) * mm, "end": v(44.89, -155) * mm});
            skPoint(sketch, "E31.2.8.8", {"position": v(42, -155) * mm});
            skLineSegment(sketch, "E31.2.8.9", {"start": v(44.89, -165) * mm, "end": v(39.11, -165) * mm});
            skLineSegment(sketch, "E31.2.8.10", {"start": v(39.11, -165) * mm, "end": v(36.23, -160) * mm});
            skLineSegment(sketch, "E31.2.8.11", {"start": v(36.23, -160) * mm, "end": v(39.11, -155) * mm});
            skLineSegment(sketch, "E31.2.8.12", {"start": v(49.5, -161) * mm, "end": v(55.28, -161) * mm});
            skLineSegment(sketch, "E31.2.8.13", {"start": v(55.28, -171) * mm, "end": v(49.5, -171) * mm});
            skLineSegment(sketch, "E31.2.9.0", {"start": v(55.28, -173) * mm, "end": v(58.17, -178) * mm});
            skLineSegment(sketch, "E31.2.9.1", {"start": v(49.5, -183) * mm, "end": v(46.62, -178) * mm});
            skLineSegment(sketch, "E31.2.9.2", {"start": v(46.62, -178) * mm, "end": v(49.5, -173) * mm});
            skLineSegment(sketch, "E31.2.9.3", {"start": v(47.77, -172) * mm, "end": v(44.89, -177) * mm});
            skLineSegment(sketch, "E31.2.9.4", {"start": v(58.17, -178) * mm, "end": v(55.28, -183) * mm});
            skPoint(sketch, "E31.2.9.5", {"position": v(52.4, -173) * mm});
            skLineSegment(sketch, "E31.2.9.6", {"start": v(44.89, -167) * mm, "end": v(47.77, -172) * mm});
            skLineSegment(sketch, "E31.2.9.7", {"start": v(39.11, -167) * mm, "end": v(44.89, -167) * mm});
            skPoint(sketch, "E31.2.9.8", {"position": v(42, -167) * mm});
            skLineSegment(sketch, "E31.2.9.9", {"start": v(44.89, -177) * mm, "end": v(39.11, -177) * mm});
            skLineSegment(sketch, "E31.2.9.10", {"start": v(39.11, -177) * mm, "end": v(36.23, -172) * mm});
            skLineSegment(sketch, "E31.2.9.11", {"start": v(36.23, -172) * mm, "end": v(39.11, -167) * mm});
            skLineSegment(sketch, "E31.2.9.12", {"start": v(49.5, -173) * mm, "end": v(55.28, -173) * mm});
            skLineSegment(sketch, "E31.2.9.13", {"start": v(55.28, -183) * mm, "end": v(49.5, -183) * mm});
            skLineSegment(sketch, "E31.2.10.0", {"start": v(55.28, -185) * mm, "end": v(58.17, -190) * mm});
            skLineSegment(sketch, "E31.2.10.1", {"start": v(49.5, -195) * mm, "end": v(46.62, -190) * mm});
            skLineSegment(sketch, "E31.2.10.2", {"start": v(46.62, -190) * mm, "end": v(49.5, -185) * mm});
            skLineSegment(sketch, "E31.2.10.3", {"start": v(47.77, -184) * mm, "end": v(44.89, -189) * mm});
            skLineSegment(sketch, "E31.2.10.4", {"start": v(58.17, -190) * mm, "end": v(55.28, -195) * mm});
            skPoint(sketch, "E31.2.10.5", {"position": v(52.4, -185) * mm});
            skLineSegment(sketch, "E31.2.10.6", {"start": v(44.89, -179) * mm, "end": v(47.77, -184) * mm});
            skLineSegment(sketch, "E31.2.10.7", {"start": v(39.11, -179) * mm, "end": v(44.89, -179) * mm});
            skPoint(sketch, "E31.2.10.8", {"position": v(42, -179) * mm});
            skLineSegment(sketch, "E31.2.10.9", {"start": v(44.89, -189) * mm, "end": v(39.11, -189) * mm});
            skLineSegment(sketch, "E31.2.10.10", {"start": v(39.11, -189) * mm, "end": v(36.23, -184) * mm});
            skLineSegment(sketch, "E31.2.10.11", {"start": v(36.23, -184) * mm, "end": v(39.11, -179) * mm});
            skLineSegment(sketch, "E31.2.10.12", {"start": v(49.5, -185) * mm, "end": v(55.28, -185) * mm});
            skLineSegment(sketch, "E31.2.10.13", {"start": v(55.28, -195) * mm, "end": v(49.5, -195) * mm});
            skLineSegment(sketch, "E31.2.11.0", {"start": v(55.28, -197) * mm, "end": v(58.17, -202) * mm});
            skLineSegment(sketch, "E31.2.11.1", {"start": v(49.5, -207) * mm, "end": v(46.62, -202) * mm});
            skLineSegment(sketch, "E31.2.11.2", {"start": v(46.62, -202) * mm, "end": v(49.5, -197) * mm});
            skLineSegment(sketch, "E31.2.11.3", {"start": v(47.77, -196) * mm, "end": v(44.89, -201) * mm});
            skLineSegment(sketch, "E31.2.11.4", {"start": v(58.17, -202) * mm, "end": v(55.28, -207) * mm});
            skPoint(sketch, "E31.2.11.5", {"position": v(52.4, -197) * mm});
            skLineSegment(sketch, "E31.2.11.6", {"start": v(44.89, -191) * mm, "end": v(47.77, -196) * mm});
            skLineSegment(sketch, "E31.2.11.7", {"start": v(39.11, -191) * mm, "end": v(44.89, -191) * mm});
            skPoint(sketch, "E31.2.11.8", {"position": v(42, -191) * mm});
            skLineSegment(sketch, "E31.2.11.9", {"start": v(44.89, -201) * mm, "end": v(39.11, -201) * mm});
            skLineSegment(sketch, "E31.2.11.10", {"start": v(39.11, -201) * mm, "end": v(36.23, -196) * mm});
            skLineSegment(sketch, "E31.2.11.11", {"start": v(36.23, -196) * mm, "end": v(39.11, -191) * mm});
            skLineSegment(sketch, "E31.2.11.12", {"start": v(49.5, -197) * mm, "end": v(55.28, -197) * mm});
            skLineSegment(sketch, "E31.2.11.13", {"start": v(55.28, -207) * mm, "end": v(49.5, -207) * mm});
            skLineSegment(sketch, "E31.2.12.0", {"start": v(55.28, -209) * mm, "end": v(58.17, -214) * mm});
            skLineSegment(sketch, "E31.2.12.1", {"start": v(49.5, -219) * mm, "end": v(46.62, -214) * mm});
            skLineSegment(sketch, "E31.2.12.2", {"start": v(46.62, -214) * mm, "end": v(49.5, -209) * mm});
            skLineSegment(sketch, "E31.2.12.3", {"start": v(47.77, -208) * mm, "end": v(44.89, -213) * mm});
            skLineSegment(sketch, "E31.2.12.4", {"start": v(58.17, -214) * mm, "end": v(55.28, -219) * mm});
            skPoint(sketch, "E31.2.12.5", {"position": v(52.4, -209) * mm});
            skLineSegment(sketch, "E31.2.12.6", {"start": v(44.89, -203) * mm, "end": v(47.77, -208) * mm});
            skLineSegment(sketch, "E31.2.12.7", {"start": v(39.11, -203) * mm, "end": v(44.89, -203) * mm});
            skPoint(sketch, "E31.2.12.8", {"position": v(42, -203) * mm});
            skLineSegment(sketch, "E31.2.12.9", {"start": v(44.89, -213) * mm, "end": v(39.11, -213) * mm});
            skLineSegment(sketch, "E31.2.12.10", {"start": v(39.11, -213) * mm, "end": v(36.23, -208) * mm});
            skLineSegment(sketch, "E31.2.12.11", {"start": v(36.23, -208) * mm, "end": v(39.11, -203) * mm});
            skLineSegment(sketch, "E31.2.12.12", {"start": v(49.5, -209) * mm, "end": v(55.28, -209) * mm});
            skLineSegment(sketch, "E31.2.12.13", {"start": v(55.28, -219) * mm, "end": v(49.5, -219) * mm});
            skLineSegment(sketch, "E31.2.13.0", {"start": v(55.28, -221) * mm, "end": v(58.17, -226) * mm});
            skLineSegment(sketch, "E31.2.13.1", {"start": v(49.5, -231) * mm, "end": v(46.62, -226) * mm});
            skLineSegment(sketch, "E31.2.13.2", {"start": v(46.62, -226) * mm, "end": v(49.5, -221) * mm});
            skLineSegment(sketch, "E31.2.13.3", {"start": v(47.77, -220) * mm, "end": v(44.89, -225) * mm});
            skLineSegment(sketch, "E31.2.13.4", {"start": v(58.17, -226) * mm, "end": v(55.28, -231) * mm});
            skPoint(sketch, "E31.2.13.5", {"position": v(52.4, -221) * mm});
            skLineSegment(sketch, "E31.2.13.6", {"start": v(44.89, -215) * mm, "end": v(47.77, -220) * mm});
            skLineSegment(sketch, "E31.2.13.7", {"start": v(39.11, -215) * mm, "end": v(44.89, -215) * mm});
            skPoint(sketch, "E31.2.13.8", {"position": v(42, -215) * mm});
            skLineSegment(sketch, "E31.2.13.9", {"start": v(44.89, -225) * mm, "end": v(39.11, -225) * mm});
            skLineSegment(sketch, "E31.2.13.10", {"start": v(39.11, -225) * mm, "end": v(36.23, -220) * mm});
            skLineSegment(sketch, "E31.2.13.11", {"start": v(36.23, -220) * mm, "end": v(39.11, -215) * mm});
            skLineSegment(sketch, "E31.2.13.12", {"start": v(49.5, -221) * mm, "end": v(55.28, -221) * mm});
            skLineSegment(sketch, "E31.2.13.13", {"start": v(55.28, -231) * mm, "end": v(49.5, -231) * mm});
            skLineSegment(sketch, "E31.2.14.0", {"start": v(55.28, -233) * mm, "end": v(58.17, -238) * mm});
            skLineSegment(sketch, "E31.2.14.1", {"start": v(49.5, -243) * mm, "end": v(46.62, -238) * mm});
            skLineSegment(sketch, "E31.2.14.2", {"start": v(46.62, -238) * mm, "end": v(49.5, -233) * mm});
            skLineSegment(sketch, "E31.2.14.3", {"start": v(47.77, -232) * mm, "end": v(44.89, -237) * mm});
            skLineSegment(sketch, "E31.2.14.4", {"start": v(58.17, -238) * mm, "end": v(55.28, -243) * mm});
            skPoint(sketch, "E31.2.14.5", {"position": v(52.4, -233) * mm});
            skLineSegment(sketch, "E31.2.14.6", {"start": v(44.89, -227) * mm, "end": v(47.77, -232) * mm});
            skLineSegment(sketch, "E31.2.14.7", {"start": v(39.11, -227) * mm, "end": v(44.89, -227) * mm});
            skPoint(sketch, "E31.2.14.8", {"position": v(42, -227) * mm});
            skLineSegment(sketch, "E31.2.14.9", {"start": v(44.89, -237) * mm, "end": v(39.11, -237) * mm});
            skLineSegment(sketch, "E31.2.14.10", {"start": v(39.11, -237) * mm, "end": v(36.23, -232) * mm});
            skLineSegment(sketch, "E31.2.14.11", {"start": v(36.23, -232) * mm, "end": v(39.11, -227) * mm});
            skLineSegment(sketch, "E31.2.14.12", {"start": v(49.5, -233) * mm, "end": v(55.28, -233) * mm});
            skLineSegment(sketch, "E31.2.14.13", {"start": v(55.28, -243) * mm, "end": v(49.5, -243) * mm});
            skLineSegment(sketch, "E31.2.15.0", {"start": v(55.28, -245) * mm, "end": v(58.17, -250) * mm});
            skLineSegment(sketch, "E31.2.15.1", {"start": v(49.5, -255) * mm, "end": v(46.62, -250) * mm});
            skLineSegment(sketch, "E31.2.15.2", {"start": v(46.62, -250) * mm, "end": v(49.5, -245) * mm});
            skLineSegment(sketch, "E31.2.15.3", {"start": v(47.77, -244) * mm, "end": v(44.89, -249) * mm});
            skLineSegment(sketch, "E31.2.15.4", {"start": v(58.17, -250) * mm, "end": v(55.28, -255) * mm});
            skPoint(sketch, "E31.2.15.5", {"position": v(52.4, -245) * mm});
            skLineSegment(sketch, "E31.2.15.6", {"start": v(44.89, -239) * mm, "end": v(47.77, -244) * mm});
            skLineSegment(sketch, "E31.2.15.7", {"start": v(39.11, -239) * mm, "end": v(44.89, -239) * mm});
            skPoint(sketch, "E31.2.15.8", {"position": v(42, -239) * mm});
            skLineSegment(sketch, "E31.2.15.9", {"start": v(44.89, -249) * mm, "end": v(39.11, -249) * mm});
            skLineSegment(sketch, "E31.2.15.10", {"start": v(39.11, -249) * mm, "end": v(36.23, -244) * mm});
            skLineSegment(sketch, "E31.2.15.11", {"start": v(36.23, -244) * mm, "end": v(39.11, -239) * mm});
            skLineSegment(sketch, "E31.2.15.12", {"start": v(49.5, -245) * mm, "end": v(55.28, -245) * mm});
            skLineSegment(sketch, "E31.2.15.13", {"start": v(55.28, -255) * mm, "end": v(49.5, -255) * mm});
            skLineSegment(sketch, "E31.2.16.3", {"start": v(47.77, -256) * mm, "end": v(44.89, -261) * mm});
            skLineSegment(sketch, "E31.2.16.6", {"start": v(44.89, -251) * mm, "end": v(47.77, -256) * mm});
            skLineSegment(sketch, "E31.2.16.7", {"start": v(39.11, -251) * mm, "end": v(44.89, -251) * mm});
            skPoint(sketch, "E31.2.16.8", {"position": v(42, -251) * mm});
            skLineSegment(sketch, "E31.2.16.9", {"start": v(44.89, -261) * mm, "end": v(39.11, -261) * mm});
            skLineSegment(sketch, "E31.2.16.10", {"start": v(39.11, -261) * mm, "end": v(36.23, -256) * mm});
            skLineSegment(sketch, "E31.2.16.11", {"start": v(36.23, -256) * mm, "end": v(39.11, -251) * mm});
            skLineSegment(sketch, "E31.3.0.0", {"start": v(34.28, -65) * mm, "end": v(37.17, -70) * mm});
            skLineSegment(sketch, "E31.3.0.1", {"start": v(28.5, -75) * mm, "end": v(25.62, -70) * mm});
            skLineSegment(sketch, "E31.3.0.2", {"start": v(25.62, -70) * mm, "end": v(28.5, -65) * mm});
            skLineSegment(sketch, "E31.3.0.3", {"start": v(26.77, -64) * mm, "end": v(23.89, -69) * mm});
            skLineSegment(sketch, "E31.3.0.4", {"start": v(37.17, -70) * mm, "end": v(34.28, -75) * mm});
            skPoint(sketch, "E31.3.0.5", {"position": v(31.4, -65) * mm});
            skLineSegment(sketch, "E31.3.0.6", {"start": v(23.89, -59) * mm, "end": v(26.77, -64) * mm});
            skLineSegment(sketch, "E31.3.0.7", {"start": v(18.11, -59) * mm, "end": v(23.89, -59) * mm});
            skPoint(sketch, "E31.3.0.8", {"position": v(21, -59) * mm});
            skLineSegment(sketch, "E31.3.0.9", {"start": v(23.89, -69) * mm, "end": v(18.11, -69) * mm});
            skLineSegment(sketch, "E31.3.0.10", {"start": v(18.11, -69) * mm, "end": v(15.23, -64) * mm});
            skLineSegment(sketch, "E31.3.0.11", {"start": v(15.23, -64) * mm, "end": v(18.11, -59) * mm});
            skLineSegment(sketch, "E31.3.0.12", {"start": v(28.5, -65) * mm, "end": v(34.28, -65) * mm});
            skLineSegment(sketch, "E31.3.0.13", {"start": v(34.28, -75) * mm, "end": v(28.5, -75) * mm});
            skLineSegment(sketch, "E31.3.1.0", {"start": v(34.28, -77) * mm, "end": v(37.17, -82) * mm});
            skLineSegment(sketch, "E31.3.1.1", {"start": v(28.5, -87) * mm, "end": v(25.62, -82) * mm});
            skLineSegment(sketch, "E31.3.1.2", {"start": v(25.62, -82) * mm, "end": v(28.5, -77) * mm});
            skLineSegment(sketch, "E31.3.1.3", {"start": v(26.77, -76) * mm, "end": v(23.89, -81) * mm});
            skLineSegment(sketch, "E31.3.1.4", {"start": v(37.17, -82) * mm, "end": v(34.28, -87) * mm});
            skPoint(sketch, "E31.3.1.5", {"position": v(31.4, -77) * mm});
            skLineSegment(sketch, "E31.3.1.6", {"start": v(23.89, -71) * mm, "end": v(26.77, -76) * mm});
            skLineSegment(sketch, "E31.3.1.7", {"start": v(18.11, -71) * mm, "end": v(23.89, -71) * mm});
            skPoint(sketch, "E31.3.1.8", {"position": v(21, -71) * mm});
            skLineSegment(sketch, "E31.3.1.9", {"start": v(23.89, -81) * mm, "end": v(18.11, -81) * mm});
            skLineSegment(sketch, "E31.3.1.10", {"start": v(18.11, -81) * mm, "end": v(15.23, -76) * mm});
            skLineSegment(sketch, "E31.3.1.11", {"start": v(15.23, -76) * mm, "end": v(18.11, -71) * mm});
            skLineSegment(sketch, "E31.3.1.12", {"start": v(28.5, -77) * mm, "end": v(34.28, -77) * mm});
            skLineSegment(sketch, "E31.3.1.13", {"start": v(34.28, -87) * mm, "end": v(28.5, -87) * mm});
            skLineSegment(sketch, "E31.3.2.0", {"start": v(34.28, -89) * mm, "end": v(37.17, -94) * mm});
            skLineSegment(sketch, "E31.3.2.1", {"start": v(28.5, -99) * mm, "end": v(25.62, -94) * mm});
            skLineSegment(sketch, "E31.3.2.2", {"start": v(25.62, -94) * mm, "end": v(28.5, -89) * mm});
            skLineSegment(sketch, "E31.3.2.3", {"start": v(26.77, -88) * mm, "end": v(23.89, -93) * mm});
            skLineSegment(sketch, "E31.3.2.4", {"start": v(37.17, -94) * mm, "end": v(34.28, -99) * mm});
            skPoint(sketch, "E31.3.2.5", {"position": v(31.4, -89) * mm});
            skLineSegment(sketch, "E31.3.2.6", {"start": v(23.89, -83) * mm, "end": v(26.77, -88) * mm});
            skLineSegment(sketch, "E31.3.2.7", {"start": v(18.11, -83) * mm, "end": v(23.89, -83) * mm});
            skPoint(sketch, "E31.3.2.8", {"position": v(21, -83) * mm});
            skLineSegment(sketch, "E31.3.2.9", {"start": v(23.89, -93) * mm, "end": v(18.11, -93) * mm});
            skLineSegment(sketch, "E31.3.2.10", {"start": v(18.11, -93) * mm, "end": v(15.23, -88) * mm});
            skLineSegment(sketch, "E31.3.2.11", {"start": v(15.23, -88) * mm, "end": v(18.11, -83) * mm});
            skLineSegment(sketch, "E31.3.2.12", {"start": v(28.5, -89) * mm, "end": v(34.28, -89) * mm});
            skLineSegment(sketch, "E31.3.2.13", {"start": v(34.28, -99) * mm, "end": v(28.5, -99) * mm});
            skLineSegment(sketch, "E31.3.3.0", {"start": v(34.28, -101) * mm, "end": v(37.17, -106) * mm});
            skLineSegment(sketch, "E31.3.3.1", {"start": v(28.5, -111) * mm, "end": v(25.62, -106) * mm});
            skLineSegment(sketch, "E31.3.3.2", {"start": v(25.62, -106) * mm, "end": v(28.5, -101) * mm});
            skLineSegment(sketch, "E31.3.3.3", {"start": v(26.77, -100) * mm, "end": v(23.89, -105) * mm});
            skLineSegment(sketch, "E31.3.3.4", {"start": v(37.17, -106) * mm, "end": v(34.28, -111) * mm});
            skPoint(sketch, "E31.3.3.5", {"position": v(31.4, -101) * mm});
            skLineSegment(sketch, "E31.3.3.6", {"start": v(23.89, -95) * mm, "end": v(26.77, -100) * mm});
            skLineSegment(sketch, "E31.3.3.7", {"start": v(18.11, -95) * mm, "end": v(23.89, -95) * mm});
            skPoint(sketch, "E31.3.3.8", {"position": v(21, -95) * mm});
            skLineSegment(sketch, "E31.3.3.9", {"start": v(23.89, -105) * mm, "end": v(18.11, -105) * mm});
            skLineSegment(sketch, "E31.3.3.10", {"start": v(18.11, -105) * mm, "end": v(15.23, -100) * mm});
            skLineSegment(sketch, "E31.3.3.11", {"start": v(15.23, -100) * mm, "end": v(18.11, -95) * mm});
            skLineSegment(sketch, "E31.3.3.12", {"start": v(28.5, -101) * mm, "end": v(34.28, -101) * mm});
            skLineSegment(sketch, "E31.3.3.13", {"start": v(34.28, -111) * mm, "end": v(28.5, -111) * mm});
            skLineSegment(sketch, "E31.3.4.0", {"start": v(34.28, -113) * mm, "end": v(37.17, -118) * mm});
            skLineSegment(sketch, "E31.3.4.1", {"start": v(28.5, -123) * mm, "end": v(25.62, -118) * mm});
            skLineSegment(sketch, "E31.3.4.2", {"start": v(25.62, -118) * mm, "end": v(28.5, -113) * mm});
            skLineSegment(sketch, "E31.3.4.3", {"start": v(26.77, -112) * mm, "end": v(23.89, -117) * mm});
            skLineSegment(sketch, "E31.3.4.4", {"start": v(37.17, -118) * mm, "end": v(34.28, -123) * mm});
            skPoint(sketch, "E31.3.4.5", {"position": v(31.4, -113) * mm});
            skLineSegment(sketch, "E31.3.4.6", {"start": v(23.89, -107) * mm, "end": v(26.77, -112) * mm});
            skLineSegment(sketch, "E31.3.4.7", {"start": v(18.11, -107) * mm, "end": v(23.89, -107) * mm});
            skPoint(sketch, "E31.3.4.8", {"position": v(21, -107) * mm});
            skLineSegment(sketch, "E31.3.4.9", {"start": v(23.89, -117) * mm, "end": v(18.11, -117) * mm});
            skLineSegment(sketch, "E31.3.4.10", {"start": v(18.11, -117) * mm, "end": v(15.23, -112) * mm});
            skLineSegment(sketch, "E31.3.4.11", {"start": v(15.23, -112) * mm, "end": v(18.11, -107) * mm});
            skLineSegment(sketch, "E31.3.4.12", {"start": v(28.5, -113) * mm, "end": v(34.28, -113) * mm});
            skLineSegment(sketch, "E31.3.4.13", {"start": v(34.28, -123) * mm, "end": v(28.5, -123) * mm});
            skLineSegment(sketch, "E31.3.5.0", {"start": v(34.28, -125) * mm, "end": v(37.17, -130) * mm});
            skLineSegment(sketch, "E31.3.5.1", {"start": v(28.5, -135) * mm, "end": v(25.62, -130) * mm});
            skLineSegment(sketch, "E31.3.5.2", {"start": v(25.62, -130) * mm, "end": v(28.5, -125) * mm});
            skLineSegment(sketch, "E31.3.5.3", {"start": v(26.77, -124) * mm, "end": v(23.89, -129) * mm});
            skLineSegment(sketch, "E31.3.5.4", {"start": v(37.17, -130) * mm, "end": v(34.28, -135) * mm});
            skPoint(sketch, "E31.3.5.5", {"position": v(31.4, -125) * mm});
            skLineSegment(sketch, "E31.3.5.6", {"start": v(23.89, -119) * mm, "end": v(26.77, -124) * mm});
            skLineSegment(sketch, "E31.3.5.7", {"start": v(18.11, -119) * mm, "end": v(23.89, -119) * mm});
            skPoint(sketch, "E31.3.5.8", {"position": v(21, -119) * mm});
            skLineSegment(sketch, "E31.3.5.9", {"start": v(23.89, -129) * mm, "end": v(18.11, -129) * mm});
            skLineSegment(sketch, "E31.3.5.10", {"start": v(18.11, -129) * mm, "end": v(15.23, -124) * mm});
            skLineSegment(sketch, "E31.3.5.11", {"start": v(15.23, -124) * mm, "end": v(18.11, -119) * mm});
            skLineSegment(sketch, "E31.3.5.12", {"start": v(28.5, -125) * mm, "end": v(34.28, -125) * mm});
            skLineSegment(sketch, "E31.3.5.13", {"start": v(34.28, -135) * mm, "end": v(28.5, -135) * mm});
            skLineSegment(sketch, "E31.3.6.0", {"start": v(34.28, -137) * mm, "end": v(37.17, -142) * mm});
            skLineSegment(sketch, "E31.3.6.1", {"start": v(28.5, -147) * mm, "end": v(25.62, -142) * mm});
            skLineSegment(sketch, "E31.3.6.2", {"start": v(25.62, -142) * mm, "end": v(28.5, -137) * mm});
            skLineSegment(sketch, "E31.3.6.3", {"start": v(26.77, -136) * mm, "end": v(23.89, -141) * mm});
            skLineSegment(sketch, "E31.3.6.4", {"start": v(37.17, -142) * mm, "end": v(34.28, -147) * mm});
            skPoint(sketch, "E31.3.6.5", {"position": v(31.4, -137) * mm});
            skLineSegment(sketch, "E31.3.6.6", {"start": v(23.89, -131) * mm, "end": v(26.77, -136) * mm});
            skLineSegment(sketch, "E31.3.6.7", {"start": v(18.11, -131) * mm, "end": v(23.89, -131) * mm});
            skPoint(sketch, "E31.3.6.8", {"position": v(21, -131) * mm});
            skLineSegment(sketch, "E31.3.6.9", {"start": v(23.89, -141) * mm, "end": v(18.11, -141) * mm});
            skLineSegment(sketch, "E31.3.6.10", {"start": v(18.11, -141) * mm, "end": v(15.23, -136) * mm});
            skLineSegment(sketch, "E31.3.6.11", {"start": v(15.23, -136) * mm, "end": v(18.11, -131) * mm});
            skLineSegment(sketch, "E31.3.6.12", {"start": v(28.5, -137) * mm, "end": v(34.28, -137) * mm});
            skLineSegment(sketch, "E31.3.6.13", {"start": v(34.28, -147) * mm, "end": v(28.5, -147) * mm});
            skLineSegment(sketch, "E31.3.7.0", {"start": v(34.28, -149) * mm, "end": v(37.17, -154) * mm});
            skLineSegment(sketch, "E31.3.7.1", {"start": v(28.5, -159) * mm, "end": v(25.62, -154) * mm});
            skLineSegment(sketch, "E31.3.7.2", {"start": v(25.62, -154) * mm, "end": v(28.5, -149) * mm});
            skLineSegment(sketch, "E31.3.7.3", {"start": v(26.77, -148) * mm, "end": v(23.89, -153) * mm});
            skLineSegment(sketch, "E31.3.7.4", {"start": v(37.17, -154) * mm, "end": v(34.28, -159) * mm});
            skPoint(sketch, "E31.3.7.5", {"position": v(31.4, -149) * mm});
            skLineSegment(sketch, "E31.3.7.6", {"start": v(23.89, -143) * mm, "end": v(26.77, -148) * mm});
            skLineSegment(sketch, "E31.3.7.7", {"start": v(18.11, -143) * mm, "end": v(23.89, -143) * mm});
            skPoint(sketch, "E31.3.7.8", {"position": v(21, -143) * mm});
            skLineSegment(sketch, "E31.3.7.9", {"start": v(23.89, -153) * mm, "end": v(18.11, -153) * mm});
            skLineSegment(sketch, "E31.3.7.10", {"start": v(18.11, -153) * mm, "end": v(15.23, -148) * mm});
            skLineSegment(sketch, "E31.3.7.11", {"start": v(15.23, -148) * mm, "end": v(18.11, -143) * mm});
            skLineSegment(sketch, "E31.3.7.12", {"start": v(28.5, -149) * mm, "end": v(34.28, -149) * mm});
            skLineSegment(sketch, "E31.3.7.13", {"start": v(34.28, -159) * mm, "end": v(28.5, -159) * mm});
            skLineSegment(sketch, "E31.3.8.0", {"start": v(34.28, -161) * mm, "end": v(37.17, -166) * mm});
            skLineSegment(sketch, "E31.3.8.1", {"start": v(28.5, -171) * mm, "end": v(25.62, -166) * mm});
            skLineSegment(sketch, "E31.3.8.2", {"start": v(25.62, -166) * mm, "end": v(28.5, -161) * mm});
            skLineSegment(sketch, "E31.3.8.3", {"start": v(26.77, -160) * mm, "end": v(23.89, -165) * mm});
            skLineSegment(sketch, "E31.3.8.4", {"start": v(37.17, -166) * mm, "end": v(34.28, -171) * mm});
            skPoint(sketch, "E31.3.8.5", {"position": v(31.4, -161) * mm});
            skLineSegment(sketch, "E31.3.8.6", {"start": v(23.89, -155) * mm, "end": v(26.77, -160) * mm});
            skLineSegment(sketch, "E31.3.8.7", {"start": v(18.11, -155) * mm, "end": v(23.89, -155) * mm});
            skPoint(sketch, "E31.3.8.8", {"position": v(21, -155) * mm});
            skLineSegment(sketch, "E31.3.8.9", {"start": v(23.89, -165) * mm, "end": v(18.11, -165) * mm});
            skLineSegment(sketch, "E31.3.8.10", {"start": v(18.11, -165) * mm, "end": v(15.23, -160) * mm});
            skLineSegment(sketch, "E31.3.8.11", {"start": v(15.23, -160) * mm, "end": v(18.11, -155) * mm});
            skLineSegment(sketch, "E31.3.8.12", {"start": v(28.5, -161) * mm, "end": v(34.28, -161) * mm});
            skLineSegment(sketch, "E31.3.8.13", {"start": v(34.28, -171) * mm, "end": v(28.5, -171) * mm});
            skLineSegment(sketch, "E31.3.9.0", {"start": v(34.28, -173) * mm, "end": v(37.17, -178) * mm});
            skLineSegment(sketch, "E31.3.9.1", {"start": v(28.5, -183) * mm, "end": v(25.62, -178) * mm});
            skLineSegment(sketch, "E31.3.9.2", {"start": v(25.62, -178) * mm, "end": v(28.5, -173) * mm});
            skLineSegment(sketch, "E31.3.9.3", {"start": v(26.77, -172) * mm, "end": v(23.89, -177) * mm});
            skLineSegment(sketch, "E31.3.9.4", {"start": v(37.17, -178) * mm, "end": v(34.28, -183) * mm});
            skPoint(sketch, "E31.3.9.5", {"position": v(31.4, -173) * mm});
            skLineSegment(sketch, "E31.3.9.6", {"start": v(23.89, -167) * mm, "end": v(26.77, -172) * mm});
            skLineSegment(sketch, "E31.3.9.7", {"start": v(18.11, -167) * mm, "end": v(23.89, -167) * mm});
            skPoint(sketch, "E31.3.9.8", {"position": v(21, -167) * mm});
            skLineSegment(sketch, "E31.3.9.9", {"start": v(23.89, -177) * mm, "end": v(18.11, -177) * mm});
            skLineSegment(sketch, "E31.3.9.10", {"start": v(18.11, -177) * mm, "end": v(15.23, -172) * mm});
            skLineSegment(sketch, "E31.3.9.11", {"start": v(15.23, -172) * mm, "end": v(18.11, -167) * mm});
            skLineSegment(sketch, "E31.3.9.12", {"start": v(28.5, -173) * mm, "end": v(34.28, -173) * mm});
            skLineSegment(sketch, "E31.3.9.13", {"start": v(34.28, -183) * mm, "end": v(28.5, -183) * mm});
            skLineSegment(sketch, "E31.3.10.0", {"start": v(34.28, -185) * mm, "end": v(37.17, -190) * mm});
            skLineSegment(sketch, "E31.3.10.1", {"start": v(28.5, -195) * mm, "end": v(25.62, -190) * mm});
            skLineSegment(sketch, "E31.3.10.2", {"start": v(25.62, -190) * mm, "end": v(28.5, -185) * mm});
            skLineSegment(sketch, "E31.3.10.3", {"start": v(26.77, -184) * mm, "end": v(23.89, -189) * mm});
            skLineSegment(sketch, "E31.3.10.4", {"start": v(37.17, -190) * mm, "end": v(34.28, -195) * mm});
            skPoint(sketch, "E31.3.10.5", {"position": v(31.4, -185) * mm});
            skLineSegment(sketch, "E31.3.10.6", {"start": v(23.89, -179) * mm, "end": v(26.77, -184) * mm});
            skLineSegment(sketch, "E31.3.10.7", {"start": v(18.11, -179) * mm, "end": v(23.89, -179) * mm});
            skPoint(sketch, "E31.3.10.8", {"position": v(21, -179) * mm});
            skLineSegment(sketch, "E31.3.10.9", {"start": v(23.89, -189) * mm, "end": v(18.11, -189) * mm});
            skLineSegment(sketch, "E31.3.10.10", {"start": v(18.11, -189) * mm, "end": v(15.23, -184) * mm});
            skLineSegment(sketch, "E31.3.10.11", {"start": v(15.23, -184) * mm, "end": v(18.11, -179) * mm});
            skLineSegment(sketch, "E31.3.10.12", {"start": v(28.5, -185) * mm, "end": v(34.28, -185) * mm});
            skLineSegment(sketch, "E31.3.10.13", {"start": v(34.28, -195) * mm, "end": v(28.5, -195) * mm});
            skLineSegment(sketch, "E31.3.11.0", {"start": v(34.28, -197) * mm, "end": v(37.17, -202) * mm});
            skLineSegment(sketch, "E31.3.11.1", {"start": v(28.5, -207) * mm, "end": v(25.62, -202) * mm});
            skLineSegment(sketch, "E31.3.11.2", {"start": v(25.62, -202) * mm, "end": v(28.5, -197) * mm});
            skLineSegment(sketch, "E31.3.11.3", {"start": v(26.77, -196) * mm, "end": v(23.89, -201) * mm});
            skLineSegment(sketch, "E31.3.11.4", {"start": v(37.17, -202) * mm, "end": v(34.28, -207) * mm});
            skPoint(sketch, "E31.3.11.5", {"position": v(31.4, -197) * mm});
            skLineSegment(sketch, "E31.3.11.6", {"start": v(23.89, -191) * mm, "end": v(26.77, -196) * mm});
            skLineSegment(sketch, "E31.3.11.7", {"start": v(18.11, -191) * mm, "end": v(23.89, -191) * mm});
            skPoint(sketch, "E31.3.11.8", {"position": v(21, -191) * mm});
            skLineSegment(sketch, "E31.3.11.9", {"start": v(23.89, -201) * mm, "end": v(18.11, -201) * mm});
            skLineSegment(sketch, "E31.3.11.10", {"start": v(18.11, -201) * mm, "end": v(15.23, -196) * mm});
            skLineSegment(sketch, "E31.3.11.11", {"start": v(15.23, -196) * mm, "end": v(18.11, -191) * mm});
            skLineSegment(sketch, "E31.3.11.12", {"start": v(28.5, -197) * mm, "end": v(34.28, -197) * mm});
            skLineSegment(sketch, "E31.3.11.13", {"start": v(34.28, -207) * mm, "end": v(28.5, -207) * mm});
            skLineSegment(sketch, "E31.3.12.0", {"start": v(34.28, -209) * mm, "end": v(37.17, -214) * mm});
            skLineSegment(sketch, "E31.3.12.1", {"start": v(28.5, -219) * mm, "end": v(25.62, -214) * mm});
            skLineSegment(sketch, "E31.3.12.2", {"start": v(25.62, -214) * mm, "end": v(28.5, -209) * mm});
            skLineSegment(sketch, "E31.3.12.3", {"start": v(26.77, -208) * mm, "end": v(23.89, -213) * mm});
            skLineSegment(sketch, "E31.3.12.4", {"start": v(37.17, -214) * mm, "end": v(34.28, -219) * mm});
            skPoint(sketch, "E31.3.12.5", {"position": v(31.4, -209) * mm});
            skLineSegment(sketch, "E31.3.12.6", {"start": v(23.89, -203) * mm, "end": v(26.77, -208) * mm});
            skLineSegment(sketch, "E31.3.12.7", {"start": v(18.11, -203) * mm, "end": v(23.89, -203) * mm});
            skPoint(sketch, "E31.3.12.8", {"position": v(21, -203) * mm});
            skLineSegment(sketch, "E31.3.12.9", {"start": v(23.89, -213) * mm, "end": v(18.11, -213) * mm});
            skLineSegment(sketch, "E31.3.12.10", {"start": v(18.11, -213) * mm, "end": v(15.23, -208) * mm});
            skLineSegment(sketch, "E31.3.12.11", {"start": v(15.23, -208) * mm, "end": v(18.11, -203) * mm});
            skLineSegment(sketch, "E31.3.12.12", {"start": v(28.5, -209) * mm, "end": v(34.28, -209) * mm});
            skLineSegment(sketch, "E31.3.12.13", {"start": v(34.28, -219) * mm, "end": v(28.5, -219) * mm});
            skLineSegment(sketch, "E31.3.13.0", {"start": v(34.28, -221) * mm, "end": v(37.17, -226) * mm});
            skLineSegment(sketch, "E31.3.13.1", {"start": v(28.5, -231) * mm, "end": v(25.62, -226) * mm});
            skLineSegment(sketch, "E31.3.13.2", {"start": v(25.62, -226) * mm, "end": v(28.5, -221) * mm});
            skLineSegment(sketch, "E31.3.13.3", {"start": v(26.77, -220) * mm, "end": v(23.89, -225) * mm});
            skLineSegment(sketch, "E31.3.13.4", {"start": v(37.17, -226) * mm, "end": v(34.28, -231) * mm});
            skPoint(sketch, "E31.3.13.5", {"position": v(31.4, -221) * mm});
            skLineSegment(sketch, "E31.3.13.6", {"start": v(23.89, -215) * mm, "end": v(26.77, -220) * mm});
            skLineSegment(sketch, "E31.3.13.7", {"start": v(18.11, -215) * mm, "end": v(23.89, -215) * mm});
            skPoint(sketch, "E31.3.13.8", {"position": v(21, -215) * mm});
            skLineSegment(sketch, "E31.3.13.9", {"start": v(23.89, -225) * mm, "end": v(18.11, -225) * mm});
            skLineSegment(sketch, "E31.3.13.10", {"start": v(18.11, -225) * mm, "end": v(15.23, -220) * mm});
            skLineSegment(sketch, "E31.3.13.11", {"start": v(15.23, -220) * mm, "end": v(18.11, -215) * mm});
            skLineSegment(sketch, "E31.3.13.12", {"start": v(28.5, -221) * mm, "end": v(34.28, -221) * mm});
            skLineSegment(sketch, "E31.3.13.13", {"start": v(34.28, -231) * mm, "end": v(28.5, -231) * mm});
            skLineSegment(sketch, "E31.3.14.0", {"start": v(34.28, -233) * mm, "end": v(37.17, -238) * mm});
            skLineSegment(sketch, "E31.3.14.1", {"start": v(28.5, -243) * mm, "end": v(25.62, -238) * mm});
            skLineSegment(sketch, "E31.3.14.2", {"start": v(25.62, -238) * mm, "end": v(28.5, -233) * mm});
            skLineSegment(sketch, "E31.3.14.3", {"start": v(26.77, -232) * mm, "end": v(23.89, -237) * mm});
            skLineSegment(sketch, "E31.3.14.4", {"start": v(37.17, -238) * mm, "end": v(34.28, -243) * mm});
            skPoint(sketch, "E31.3.14.5", {"position": v(31.4, -233) * mm});
            skLineSegment(sketch, "E31.3.14.6", {"start": v(23.89, -227) * mm, "end": v(26.77, -232) * mm});
            skLineSegment(sketch, "E31.3.14.7", {"start": v(18.11, -227) * mm, "end": v(23.89, -227) * mm});
            skPoint(sketch, "E31.3.14.8", {"position": v(21, -227) * mm});
            skLineSegment(sketch, "E31.3.14.9", {"start": v(23.89, -237) * mm, "end": v(18.11, -237) * mm});
            skLineSegment(sketch, "E31.3.14.10", {"start": v(18.11, -237) * mm, "end": v(15.23, -232) * mm});
            skLineSegment(sketch, "E31.3.14.11", {"start": v(15.23, -232) * mm, "end": v(18.11, -227) * mm});
            skLineSegment(sketch, "E31.3.14.12", {"start": v(28.5, -233) * mm, "end": v(34.28, -233) * mm});
            skLineSegment(sketch, "E31.3.14.13", {"start": v(34.28, -243) * mm, "end": v(28.5, -243) * mm});
            skLineSegment(sketch, "E31.3.15.0", {"start": v(34.28, -245) * mm, "end": v(37.17, -250) * mm});
            skLineSegment(sketch, "E31.3.15.1", {"start": v(28.5, -255) * mm, "end": v(25.62, -250) * mm});
            skLineSegment(sketch, "E31.3.15.2", {"start": v(25.62, -250) * mm, "end": v(28.5, -245) * mm});
            skLineSegment(sketch, "E31.3.15.3", {"start": v(26.77, -244) * mm, "end": v(23.89, -249) * mm});
            skLineSegment(sketch, "E31.3.15.4", {"start": v(37.17, -250) * mm, "end": v(34.28, -255) * mm});
            skPoint(sketch, "E31.3.15.5", {"position": v(31.4, -245) * mm});
            skLineSegment(sketch, "E31.3.15.6", {"start": v(23.89, -239) * mm, "end": v(26.77, -244) * mm});
            skLineSegment(sketch, "E31.3.15.7", {"start": v(18.11, -239) * mm, "end": v(23.89, -239) * mm});
            skPoint(sketch, "E31.3.15.8", {"position": v(21, -239) * mm});
            skLineSegment(sketch, "E31.3.15.9", {"start": v(23.89, -249) * mm, "end": v(18.11, -249) * mm});
            skLineSegment(sketch, "E31.3.15.10", {"start": v(18.11, -249) * mm, "end": v(15.23, -244) * mm});
            skLineSegment(sketch, "E31.3.15.11", {"start": v(15.23, -244) * mm, "end": v(18.11, -239) * mm});
            skLineSegment(sketch, "E31.3.15.12", {"start": v(28.5, -245) * mm, "end": v(34.28, -245) * mm});
            skLineSegment(sketch, "E31.3.15.13", {"start": v(34.28, -255) * mm, "end": v(28.5, -255) * mm});
            skLineSegment(sketch, "E31.3.16.3", {"start": v(26.77, -256) * mm, "end": v(23.89, -261) * mm});
            skLineSegment(sketch, "E31.3.16.6", {"start": v(23.89, -251) * mm, "end": v(26.77, -256) * mm});
            skLineSegment(sketch, "E31.3.16.7", {"start": v(18.11, -251) * mm, "end": v(23.89, -251) * mm});
            skPoint(sketch, "E31.3.16.8", {"position": v(21, -251) * mm});
            skLineSegment(sketch, "E31.3.16.9", {"start": v(23.89, -261) * mm, "end": v(18.11, -261) * mm});
            skLineSegment(sketch, "E31.3.16.10", {"start": v(18.11, -261) * mm, "end": v(15.23, -256) * mm});
            skLineSegment(sketch, "E31.3.16.11", {"start": v(15.23, -256) * mm, "end": v(18.11, -251) * mm});
            skLineSegment(sketch, "E31.4.0.0", {"start": v(13.28, -65) * mm, "end": v(16.17, -70) * mm});
            skLineSegment(sketch, "E31.4.0.1", {"start": v(7.5, -75) * mm, "end": v(4.62, -70) * mm});
            skLineSegment(sketch, "E31.4.0.2", {"start": v(4.62, -70) * mm, "end": v(7.5, -65) * mm});
            skLineSegment(sketch, "E31.4.0.3", {"start": v(5.77, -64) * mm, "end": v(2.89, -69) * mm});
            skLineSegment(sketch, "E31.4.0.4", {"start": v(16.17, -70) * mm, "end": v(13.28, -75) * mm});
            skPoint(sketch, "E31.4.0.5", {"position": v(10.4, -65) * mm});
            skLineSegment(sketch, "E31.4.0.6", {"start": v(2.89, -59) * mm, "end": v(5.77, -64) * mm});
            skLineSegment(sketch, "E31.4.0.7", {"start": v(-2.89, -59) * mm, "end": v(2.89, -59) * mm});
            skPoint(sketch, "E31.4.0.8", {"position": v(0, -59) * mm});
            skLineSegment(sketch, "E31.4.0.9", {"start": v(2.89, -69) * mm, "end": v(-2.89, -69) * mm});
            skLineSegment(sketch, "E31.4.0.10", {"start": v(-2.89, -69) * mm, "end": v(-5.77, -64) * mm});
            skLineSegment(sketch, "E31.4.0.11", {"start": v(-5.77, -64) * mm, "end": v(-2.89, -59) * mm});
            skLineSegment(sketch, "E31.4.0.12", {"start": v(7.5, -65) * mm, "end": v(13.28, -65) * mm});
            skLineSegment(sketch, "E31.4.0.13", {"start": v(13.28, -75) * mm, "end": v(7.5, -75) * mm});
            skLineSegment(sketch, "E31.4.1.0", {"start": v(13.28, -77) * mm, "end": v(16.17, -82) * mm});
            skLineSegment(sketch, "E31.4.1.1", {"start": v(7.5, -87) * mm, "end": v(4.62, -82) * mm});
            skLineSegment(sketch, "E31.4.1.2", {"start": v(4.62, -82) * mm, "end": v(7.5, -77) * mm});
            skLineSegment(sketch, "E31.4.1.3", {"start": v(5.77, -76) * mm, "end": v(2.89, -81) * mm});
            skLineSegment(sketch, "E31.4.1.4", {"start": v(16.17, -82) * mm, "end": v(13.28, -87) * mm});
            skPoint(sketch, "E31.4.1.5", {"position": v(10.4, -77) * mm});
            skLineSegment(sketch, "E31.4.1.6", {"start": v(2.89, -71) * mm, "end": v(5.77, -76) * mm});
            skLineSegment(sketch, "E31.4.1.7", {"start": v(-2.89, -71) * mm, "end": v(2.89, -71) * mm});
            skPoint(sketch, "E31.4.1.8", {"position": v(0, -71) * mm});
            skLineSegment(sketch, "E31.4.1.9", {"start": v(2.89, -81) * mm, "end": v(-2.89, -81) * mm});
            skLineSegment(sketch, "E31.4.1.10", {"start": v(-2.89, -81) * mm, "end": v(-5.77, -76) * mm});
            skLineSegment(sketch, "E31.4.1.11", {"start": v(-5.77, -76) * mm, "end": v(-2.89, -71) * mm});
            skLineSegment(sketch, "E31.4.1.12", {"start": v(7.5, -77) * mm, "end": v(13.28, -77) * mm});
            skLineSegment(sketch, "E31.4.1.13", {"start": v(13.28, -87) * mm, "end": v(7.5, -87) * mm});
            skLineSegment(sketch, "E31.4.2.0", {"start": v(13.28, -89) * mm, "end": v(16.17, -94) * mm});
            skLineSegment(sketch, "E31.4.2.1", {"start": v(7.5, -99) * mm, "end": v(4.62, -94) * mm});
            skLineSegment(sketch, "E31.4.2.2", {"start": v(4.62, -94) * mm, "end": v(7.5, -89) * mm});
            skLineSegment(sketch, "E31.4.2.3", {"start": v(5.77, -88) * mm, "end": v(2.89, -93) * mm});
            skLineSegment(sketch, "E31.4.2.4", {"start": v(16.17, -94) * mm, "end": v(13.28, -99) * mm});
            skPoint(sketch, "E31.4.2.5", {"position": v(10.4, -89) * mm});
            skLineSegment(sketch, "E31.4.2.6", {"start": v(2.89, -83) * mm, "end": v(5.77, -88) * mm});
            skLineSegment(sketch, "E31.4.2.7", {"start": v(-2.89, -83) * mm, "end": v(2.89, -83) * mm});
            skPoint(sketch, "E31.4.2.8", {"position": v(0, -83) * mm});
            skLineSegment(sketch, "E31.4.2.9", {"start": v(2.89, -93) * mm, "end": v(-2.89, -93) * mm});
            skLineSegment(sketch, "E31.4.2.10", {"start": v(-2.89, -93) * mm, "end": v(-5.77, -88) * mm});
            skLineSegment(sketch, "E31.4.2.11", {"start": v(-5.77, -88) * mm, "end": v(-2.89, -83) * mm});
            skLineSegment(sketch, "E31.4.2.12", {"start": v(7.5, -89) * mm, "end": v(13.28, -89) * mm});
            skLineSegment(sketch, "E31.4.2.13", {"start": v(13.28, -99) * mm, "end": v(7.5, -99) * mm});
            skLineSegment(sketch, "E31.4.3.0", {"start": v(13.28, -101) * mm, "end": v(16.17, -106) * mm});
            skLineSegment(sketch, "E31.4.3.1", {"start": v(7.5, -111) * mm, "end": v(4.62, -106) * mm});
            skLineSegment(sketch, "E31.4.3.2", {"start": v(4.62, -106) * mm, "end": v(7.5, -101) * mm});
            skLineSegment(sketch, "E31.4.3.3", {"start": v(5.77, -100) * mm, "end": v(2.89, -105) * mm});
            skLineSegment(sketch, "E31.4.3.4", {"start": v(16.17, -106) * mm, "end": v(13.28, -111) * mm});
            skPoint(sketch, "E31.4.3.5", {"position": v(10.4, -101) * mm});
            skLineSegment(sketch, "E31.4.3.6", {"start": v(2.89, -95) * mm, "end": v(5.77, -100) * mm});
            skLineSegment(sketch, "E31.4.3.7", {"start": v(-2.89, -95) * mm, "end": v(2.89, -95) * mm});
            skPoint(sketch, "E31.4.3.8", {"position": v(0, -95) * mm});
            skLineSegment(sketch, "E31.4.3.9", {"start": v(2.89, -105) * mm, "end": v(-2.89, -105) * mm});
            skLineSegment(sketch, "E31.4.3.10", {"start": v(-2.89, -105) * mm, "end": v(-5.77, -100) * mm});
            skLineSegment(sketch, "E31.4.3.11", {"start": v(-5.77, -100) * mm, "end": v(-2.89, -95) * mm});
            skLineSegment(sketch, "E31.4.3.12", {"start": v(7.5, -101) * mm, "end": v(13.28, -101) * mm});
            skLineSegment(sketch, "E31.4.3.13", {"start": v(13.28, -111) * mm, "end": v(7.5, -111) * mm});
            skLineSegment(sketch, "E31.4.4.0", {"start": v(13.28, -113) * mm, "end": v(16.17, -118) * mm});
            skLineSegment(sketch, "E31.4.4.1", {"start": v(7.5, -123) * mm, "end": v(4.62, -118) * mm});
            skLineSegment(sketch, "E31.4.4.2", {"start": v(4.62, -118) * mm, "end": v(7.5, -113) * mm});
            skLineSegment(sketch, "E31.4.4.3", {"start": v(5.77, -112) * mm, "end": v(2.89, -117) * mm});
            skLineSegment(sketch, "E31.4.4.4", {"start": v(16.17, -118) * mm, "end": v(13.28, -123) * mm});
            skPoint(sketch, "E31.4.4.5", {"position": v(10.4, -113) * mm});
            skLineSegment(sketch, "E31.4.4.6", {"start": v(2.89, -107) * mm, "end": v(5.77, -112) * mm});
            skLineSegment(sketch, "E31.4.4.7", {"start": v(-2.89, -107) * mm, "end": v(2.89, -107) * mm});
            skPoint(sketch, "E31.4.4.8", {"position": v(0, -107) * mm});
            skLineSegment(sketch, "E31.4.4.9", {"start": v(2.89, -117) * mm, "end": v(-2.89, -117) * mm});
            skLineSegment(sketch, "E31.4.4.10", {"start": v(-2.89, -117) * mm, "end": v(-5.77, -112) * mm});
            skLineSegment(sketch, "E31.4.4.11", {"start": v(-5.77, -112) * mm, "end": v(-2.89, -107) * mm});
            skLineSegment(sketch, "E31.4.4.12", {"start": v(7.5, -113) * mm, "end": v(13.28, -113) * mm});
            skLineSegment(sketch, "E31.4.4.13", {"start": v(13.28, -123) * mm, "end": v(7.5, -123) * mm});
            skLineSegment(sketch, "E31.4.5.0", {"start": v(13.28, -125) * mm, "end": v(16.17, -130) * mm});
            skLineSegment(sketch, "E31.4.5.1", {"start": v(7.5, -135) * mm, "end": v(4.62, -130) * mm});
            skLineSegment(sketch, "E31.4.5.2", {"start": v(4.62, -130) * mm, "end": v(7.5, -125) * mm});
            skLineSegment(sketch, "E31.4.5.3", {"start": v(5.77, -124) * mm, "end": v(2.89, -129) * mm});
            skLineSegment(sketch, "E31.4.5.4", {"start": v(16.17, -130) * mm, "end": v(13.28, -135) * mm});
            skPoint(sketch, "E31.4.5.5", {"position": v(10.4, -125) * mm});
            skLineSegment(sketch, "E31.4.5.6", {"start": v(2.89, -119) * mm, "end": v(5.77, -124) * mm});
            skLineSegment(sketch, "E31.4.5.7", {"start": v(-2.89, -119) * mm, "end": v(2.89, -119) * mm});
            skPoint(sketch, "E31.4.5.8", {"position": v(0, -119) * mm});
            skLineSegment(sketch, "E31.4.5.9", {"start": v(2.89, -129) * mm, "end": v(-2.89, -129) * mm});
            skLineSegment(sketch, "E31.4.5.10", {"start": v(-2.89, -129) * mm, "end": v(-5.77, -124) * mm});
            skLineSegment(sketch, "E31.4.5.11", {"start": v(-5.77, -124) * mm, "end": v(-2.89, -119) * mm});
            skLineSegment(sketch, "E31.4.5.12", {"start": v(7.5, -125) * mm, "end": v(13.28, -125) * mm});
            skLineSegment(sketch, "E31.4.5.13", {"start": v(13.28, -135) * mm, "end": v(7.5, -135) * mm});
            skLineSegment(sketch, "E31.4.6.0", {"start": v(13.28, -137) * mm, "end": v(16.17, -142) * mm});
            skLineSegment(sketch, "E31.4.6.1", {"start": v(7.5, -147) * mm, "end": v(4.62, -142) * mm});
            skLineSegment(sketch, "E31.4.6.2", {"start": v(4.62, -142) * mm, "end": v(7.5, -137) * mm});
            skLineSegment(sketch, "E31.4.6.3", {"start": v(5.77, -136) * mm, "end": v(2.89, -141) * mm});
            skLineSegment(sketch, "E31.4.6.4", {"start": v(16.17, -142) * mm, "end": v(13.28, -147) * mm});
            skPoint(sketch, "E31.4.6.5", {"position": v(10.4, -137) * mm});
            skLineSegment(sketch, "E31.4.6.6", {"start": v(2.89, -131) * mm, "end": v(5.77, -136) * mm});
            skLineSegment(sketch, "E31.4.6.7", {"start": v(-2.89, -131) * mm, "end": v(2.89, -131) * mm});
            skPoint(sketch, "E31.4.6.8", {"position": v(0, -131) * mm});
            skLineSegment(sketch, "E31.4.6.9", {"start": v(2.89, -141) * mm, "end": v(-2.89, -141) * mm});
            skLineSegment(sketch, "E31.4.6.10", {"start": v(-2.89, -141) * mm, "end": v(-5.77, -136) * mm});
            skLineSegment(sketch, "E31.4.6.11", {"start": v(-5.77, -136) * mm, "end": v(-2.89, -131) * mm});
            skLineSegment(sketch, "E31.4.6.12", {"start": v(7.5, -137) * mm, "end": v(13.28, -137) * mm});
            skLineSegment(sketch, "E31.4.6.13", {"start": v(13.28, -147) * mm, "end": v(7.5, -147) * mm});
            skLineSegment(sketch, "E31.4.7.0", {"start": v(13.28, -149) * mm, "end": v(16.17, -154) * mm});
            skLineSegment(sketch, "E31.4.7.1", {"start": v(7.5, -159) * mm, "end": v(4.62, -154) * mm});
            skLineSegment(sketch, "E31.4.7.2", {"start": v(4.62, -154) * mm, "end": v(7.5, -149) * mm});
            skLineSegment(sketch, "E31.4.7.3", {"start": v(5.77, -148) * mm, "end": v(2.89, -153) * mm});
            skLineSegment(sketch, "E31.4.7.4", {"start": v(16.17, -154) * mm, "end": v(13.28, -159) * mm});
            skPoint(sketch, "E31.4.7.5", {"position": v(10.4, -149) * mm});
            skLineSegment(sketch, "E31.4.7.6", {"start": v(2.89, -143) * mm, "end": v(5.77, -148) * mm});
            skLineSegment(sketch, "E31.4.7.7", {"start": v(-2.89, -143) * mm, "end": v(2.89, -143) * mm});
            skPoint(sketch, "E31.4.7.8", {"position": v(0, -143) * mm});
            skLineSegment(sketch, "E31.4.7.9", {"start": v(2.89, -153) * mm, "end": v(-2.89, -153) * mm});
            skLineSegment(sketch, "E31.4.7.10", {"start": v(-2.89, -153) * mm, "end": v(-5.77, -148) * mm});
            skLineSegment(sketch, "E31.4.7.11", {"start": v(-5.77, -148) * mm, "end": v(-2.89, -143) * mm});
            skLineSegment(sketch, "E31.4.7.12", {"start": v(7.5, -149) * mm, "end": v(13.28, -149) * mm});
            skLineSegment(sketch, "E31.4.7.13", {"start": v(13.28, -159) * mm, "end": v(7.5, -159) * mm});
            skLineSegment(sketch, "E31.4.8.0", {"start": v(13.28, -161) * mm, "end": v(16.17, -166) * mm});
            skLineSegment(sketch, "E31.4.8.1", {"start": v(7.5, -171) * mm, "end": v(4.62, -166) * mm});
            skLineSegment(sketch, "E31.4.8.2", {"start": v(4.62, -166) * mm, "end": v(7.5, -161) * mm});
            skLineSegment(sketch, "E31.4.8.3", {"start": v(5.77, -160) * mm, "end": v(2.89, -165) * mm});
            skLineSegment(sketch, "E31.4.8.4", {"start": v(16.17, -166) * mm, "end": v(13.28, -171) * mm});
            skPoint(sketch, "E31.4.8.5", {"position": v(10.4, -161) * mm});
            skLineSegment(sketch, "E31.4.8.6", {"start": v(2.89, -155) * mm, "end": v(5.77, -160) * mm});
            skLineSegment(sketch, "E31.4.8.7", {"start": v(-2.89, -155) * mm, "end": v(2.89, -155) * mm});
            skPoint(sketch, "E31.4.8.8", {"position": v(0, -155) * mm});
            skLineSegment(sketch, "E31.4.8.9", {"start": v(2.89, -165) * mm, "end": v(-2.89, -165) * mm});
            skLineSegment(sketch, "E31.4.8.10", {"start": v(-2.89, -165) * mm, "end": v(-5.77, -160) * mm});
            skLineSegment(sketch, "E31.4.8.11", {"start": v(-5.77, -160) * mm, "end": v(-2.89, -155) * mm});
            skLineSegment(sketch, "E31.4.8.12", {"start": v(7.5, -161) * mm, "end": v(13.28, -161) * mm});
            skLineSegment(sketch, "E31.4.8.13", {"start": v(13.28, -171) * mm, "end": v(7.5, -171) * mm});
            skLineSegment(sketch, "E31.4.9.0", {"start": v(13.28, -173) * mm, "end": v(16.17, -178) * mm});
            skLineSegment(sketch, "E31.4.9.1", {"start": v(7.5, -183) * mm, "end": v(4.62, -178) * mm});
            skLineSegment(sketch, "E31.4.9.2", {"start": v(4.62, -178) * mm, "end": v(7.5, -173) * mm});
            skLineSegment(sketch, "E31.4.9.3", {"start": v(5.77, -172) * mm, "end": v(2.89, -177) * mm});
            skLineSegment(sketch, "E31.4.9.4", {"start": v(16.17, -178) * mm, "end": v(13.28, -183) * mm});
            skPoint(sketch, "E31.4.9.5", {"position": v(10.4, -173) * mm});
            skLineSegment(sketch, "E31.4.9.6", {"start": v(2.89, -167) * mm, "end": v(5.77, -172) * mm});
            skLineSegment(sketch, "E31.4.9.7", {"start": v(-2.89, -167) * mm, "end": v(2.89, -167) * mm});
            skPoint(sketch, "E31.4.9.8", {"position": v(0, -167) * mm});
            skLineSegment(sketch, "E31.4.9.9", {"start": v(2.89, -177) * mm, "end": v(-2.89, -177) * mm});
            skLineSegment(sketch, "E31.4.9.10", {"start": v(-2.89, -177) * mm, "end": v(-5.77, -172) * mm});
            skLineSegment(sketch, "E31.4.9.11", {"start": v(-5.77, -172) * mm, "end": v(-2.89, -167) * mm});
            skLineSegment(sketch, "E31.4.9.12", {"start": v(7.5, -173) * mm, "end": v(13.28, -173) * mm});
            skLineSegment(sketch, "E31.4.9.13", {"start": v(13.28, -183) * mm, "end": v(7.5, -183) * mm});
            skLineSegment(sketch, "E31.4.10.0", {"start": v(13.28, -185) * mm, "end": v(16.17, -190) * mm});
            skLineSegment(sketch, "E31.4.10.1", {"start": v(7.5, -195) * mm, "end": v(4.62, -190) * mm});
            skLineSegment(sketch, "E31.4.10.2", {"start": v(4.62, -190) * mm, "end": v(7.5, -185) * mm});
            skLineSegment(sketch, "E31.4.10.3", {"start": v(5.77, -184) * mm, "end": v(2.89, -189) * mm});
            skLineSegment(sketch, "E31.4.10.4", {"start": v(16.17, -190) * mm, "end": v(13.28, -195) * mm});
            skPoint(sketch, "E31.4.10.5", {"position": v(10.4, -185) * mm});
            skLineSegment(sketch, "E31.4.10.6", {"start": v(2.89, -179) * mm, "end": v(5.77, -184) * mm});
            skLineSegment(sketch, "E31.4.10.7", {"start": v(-2.89, -179) * mm, "end": v(2.89, -179) * mm});
            skPoint(sketch, "E31.4.10.8", {"position": v(0, -179) * mm});
            skLineSegment(sketch, "E31.4.10.9", {"start": v(2.89, -189) * mm, "end": v(-2.89, -189) * mm});
            skLineSegment(sketch, "E31.4.10.10", {"start": v(-2.89, -189) * mm, "end": v(-5.77, -184) * mm});
            skLineSegment(sketch, "E31.4.10.11", {"start": v(-5.77, -184) * mm, "end": v(-2.89, -179) * mm});
            skLineSegment(sketch, "E31.4.10.12", {"start": v(7.5, -185) * mm, "end": v(13.28, -185) * mm});
            skLineSegment(sketch, "E31.4.10.13", {"start": v(13.28, -195) * mm, "end": v(7.5, -195) * mm});
            skLineSegment(sketch, "E31.4.11.0", {"start": v(13.28, -197) * mm, "end": v(16.17, -202) * mm});
            skLineSegment(sketch, "E31.4.11.1", {"start": v(7.5, -207) * mm, "end": v(4.62, -202) * mm});
            skLineSegment(sketch, "E31.4.11.2", {"start": v(4.62, -202) * mm, "end": v(7.5, -197) * mm});
            skLineSegment(sketch, "E31.4.11.3", {"start": v(5.77, -196) * mm, "end": v(2.89, -201) * mm});
            skLineSegment(sketch, "E31.4.11.4", {"start": v(16.17, -202) * mm, "end": v(13.28, -207) * mm});
            skPoint(sketch, "E31.4.11.5", {"position": v(10.4, -197) * mm});
            skLineSegment(sketch, "E31.4.11.6", {"start": v(2.89, -191) * mm, "end": v(5.77, -196) * mm});
            skLineSegment(sketch, "E31.4.11.7", {"start": v(-2.89, -191) * mm, "end": v(2.89, -191) * mm});
            skPoint(sketch, "E31.4.11.8", {"position": v(0, -191) * mm});
            skLineSegment(sketch, "E31.4.11.9", {"start": v(2.89, -201) * mm, "end": v(-2.89, -201) * mm});
            skLineSegment(sketch, "E31.4.11.10", {"start": v(-2.89, -201) * mm, "end": v(-5.77, -196) * mm});
            skLineSegment(sketch, "E31.4.11.11", {"start": v(-5.77, -196) * mm, "end": v(-2.89, -191) * mm});
            skLineSegment(sketch, "E31.4.11.12", {"start": v(7.5, -197) * mm, "end": v(13.28, -197) * mm});
            skLineSegment(sketch, "E31.4.11.13", {"start": v(13.28, -207) * mm, "end": v(7.5, -207) * mm});
            skLineSegment(sketch, "E31.4.12.0", {"start": v(13.28, -209) * mm, "end": v(16.17, -214) * mm});
            skLineSegment(sketch, "E31.4.12.1", {"start": v(7.5, -219) * mm, "end": v(4.62, -214) * mm});
            skLineSegment(sketch, "E31.4.12.2", {"start": v(4.62, -214) * mm, "end": v(7.5, -209) * mm});
            skLineSegment(sketch, "E31.4.12.3", {"start": v(5.77, -208) * mm, "end": v(2.89, -213) * mm});
            skLineSegment(sketch, "E31.4.12.4", {"start": v(16.17, -214) * mm, "end": v(13.28, -219) * mm});
            skPoint(sketch, "E31.4.12.5", {"position": v(10.4, -209) * mm});
            skLineSegment(sketch, "E31.4.12.6", {"start": v(2.89, -203) * mm, "end": v(5.77, -208) * mm});
            skLineSegment(sketch, "E31.4.12.7", {"start": v(-2.89, -203) * mm, "end": v(2.89, -203) * mm});
            skPoint(sketch, "E31.4.12.8", {"position": v(0, -203) * mm});
            skLineSegment(sketch, "E31.4.12.9", {"start": v(2.89, -213) * mm, "end": v(-2.89, -213) * mm});
            skLineSegment(sketch, "E31.4.12.10", {"start": v(-2.89, -213) * mm, "end": v(-5.77, -208) * mm});
            skLineSegment(sketch, "E31.4.12.11", {"start": v(-5.77, -208) * mm, "end": v(-2.89, -203) * mm});
            skLineSegment(sketch, "E31.4.12.12", {"start": v(7.5, -209) * mm, "end": v(13.28, -209) * mm});
            skLineSegment(sketch, "E31.4.12.13", {"start": v(13.28, -219) * mm, "end": v(7.5, -219) * mm});
            skLineSegment(sketch, "E31.4.13.0", {"start": v(13.28, -221) * mm, "end": v(16.17, -226) * mm});
            skLineSegment(sketch, "E31.4.13.1", {"start": v(7.5, -231) * mm, "end": v(4.62, -226) * mm});
            skLineSegment(sketch, "E31.4.13.2", {"start": v(4.62, -226) * mm, "end": v(7.5, -221) * mm});
            skLineSegment(sketch, "E31.4.13.3", {"start": v(5.77, -220) * mm, "end": v(2.89, -225) * mm});
            skLineSegment(sketch, "E31.4.13.4", {"start": v(16.17, -226) * mm, "end": v(13.28, -231) * mm});
            skPoint(sketch, "E31.4.13.5", {"position": v(10.4, -221) * mm});
            skLineSegment(sketch, "E31.4.13.6", {"start": v(2.89, -215) * mm, "end": v(5.77, -220) * mm});
            skLineSegment(sketch, "E31.4.13.7", {"start": v(-2.89, -215) * mm, "end": v(2.89, -215) * mm});
            skPoint(sketch, "E31.4.13.8", {"position": v(0, -215) * mm});
            skLineSegment(sketch, "E31.4.13.9", {"start": v(2.89, -225) * mm, "end": v(-2.89, -225) * mm});
            skLineSegment(sketch, "E31.4.13.10", {"start": v(-2.89, -225) * mm, "end": v(-5.77, -220) * mm});
            skLineSegment(sketch, "E31.4.13.11", {"start": v(-5.77, -220) * mm, "end": v(-2.89, -215) * mm});
            skLineSegment(sketch, "E31.4.13.12", {"start": v(7.5, -221) * mm, "end": v(13.28, -221) * mm});
            skLineSegment(sketch, "E31.4.13.13", {"start": v(13.28, -231) * mm, "end": v(7.5, -231) * mm});
            skLineSegment(sketch, "E31.4.14.0", {"start": v(13.28, -233) * mm, "end": v(16.17, -238) * mm});
            skLineSegment(sketch, "E31.4.14.1", {"start": v(7.5, -243) * mm, "end": v(4.62, -238) * mm});
            skLineSegment(sketch, "E31.4.14.2", {"start": v(4.62, -238) * mm, "end": v(7.5, -233) * mm});
            skLineSegment(sketch, "E31.4.14.3", {"start": v(5.77, -232) * mm, "end": v(2.89, -237) * mm});
            skLineSegment(sketch, "E31.4.14.4", {"start": v(16.17, -238) * mm, "end": v(13.28, -243) * mm});
            skPoint(sketch, "E31.4.14.5", {"position": v(10.4, -233) * mm});
            skLineSegment(sketch, "E31.4.14.6", {"start": v(2.89, -227) * mm, "end": v(5.77, -232) * mm});
            skLineSegment(sketch, "E31.4.14.7", {"start": v(-2.89, -227) * mm, "end": v(2.89, -227) * mm});
            skPoint(sketch, "E31.4.14.8", {"position": v(0, -227) * mm});
            skLineSegment(sketch, "E31.4.14.9", {"start": v(2.89, -237) * mm, "end": v(-2.89, -237) * mm});
            skLineSegment(sketch, "E31.4.14.10", {"start": v(-2.89, -237) * mm, "end": v(-5.77, -232) * mm});
            skLineSegment(sketch, "E31.4.14.11", {"start": v(-5.77, -232) * mm, "end": v(-2.89, -227) * mm});
            skLineSegment(sketch, "E31.4.14.12", {"start": v(7.5, -233) * mm, "end": v(13.28, -233) * mm});
            skLineSegment(sketch, "E31.4.14.13", {"start": v(13.28, -243) * mm, "end": v(7.5, -243) * mm});
            skLineSegment(sketch, "E31.4.15.0", {"start": v(13.28, -245) * mm, "end": v(16.17, -250) * mm});
            skLineSegment(sketch, "E31.4.15.1", {"start": v(7.5, -255) * mm, "end": v(4.62, -250) * mm});
            skLineSegment(sketch, "E31.4.15.2", {"start": v(4.62, -250) * mm, "end": v(7.5, -245) * mm});
            skLineSegment(sketch, "E31.4.15.3", {"start": v(5.77, -244) * mm, "end": v(2.89, -249) * mm});
            skLineSegment(sketch, "E31.4.15.4", {"start": v(16.17, -250) * mm, "end": v(13.28, -255) * mm});
            skPoint(sketch, "E31.4.15.5", {"position": v(10.4, -245) * mm});
            skLineSegment(sketch, "E31.4.15.6", {"start": v(2.89, -239) * mm, "end": v(5.77, -244) * mm});
            skLineSegment(sketch, "E31.4.15.7", {"start": v(-2.89, -239) * mm, "end": v(2.89, -239) * mm});
            skPoint(sketch, "E31.4.15.8", {"position": v(0, -239) * mm});
            skLineSegment(sketch, "E31.4.15.9", {"start": v(2.89, -249) * mm, "end": v(-2.89, -249) * mm});
            skLineSegment(sketch, "E31.4.15.10", {"start": v(-2.89, -249) * mm, "end": v(-5.77, -244) * mm});
            skLineSegment(sketch, "E31.4.15.11", {"start": v(-5.77, -244) * mm, "end": v(-2.89, -239) * mm});
            skLineSegment(sketch, "E31.4.15.12", {"start": v(7.5, -245) * mm, "end": v(13.28, -245) * mm});
            skLineSegment(sketch, "E31.4.15.13", {"start": v(13.28, -255) * mm, "end": v(7.5, -255) * mm});
            skLineSegment(sketch, "E31.4.16.3", {"start": v(5.77, -256) * mm, "end": v(2.89, -261) * mm});
            skLineSegment(sketch, "E31.4.16.6", {"start": v(2.89, -251) * mm, "end": v(5.77, -256) * mm});
            skLineSegment(sketch, "E31.4.16.7", {"start": v(-2.89, -251) * mm, "end": v(2.89, -251) * mm});
            skPoint(sketch, "E31.4.16.8", {"position": v(0, -251) * mm});
            skLineSegment(sketch, "E31.4.16.9", {"start": v(2.89, -261) * mm, "end": v(-2.89, -261) * mm});
            skLineSegment(sketch, "E31.4.16.10", {"start": v(-2.89, -261) * mm, "end": v(-5.77, -256) * mm});
            skLineSegment(sketch, "E31.4.16.11", {"start": v(-5.77, -256) * mm, "end": v(-2.89, -251) * mm});
            skLineSegment(sketch, "E31.5.0.0", {"start": v(-7.72, -65) * mm, "end": v(-4.83, -70) * mm});
            skLineSegment(sketch, "E31.5.0.1", {"start": v(-13.5, -75) * mm, "end": v(-16.38, -70) * mm});
            skLineSegment(sketch, "E31.5.0.2", {"start": v(-16.38, -70) * mm, "end": v(-13.5, -65) * mm});
            skLineSegment(sketch, "E31.5.0.3", {"start": v(-15.23, -64) * mm, "end": v(-18.11, -69) * mm});
            skLineSegment(sketch, "E31.5.0.4", {"start": v(-4.83, -70) * mm, "end": v(-7.72, -75) * mm});
            skPoint(sketch, "E31.5.0.5", {"position": v(-10.6, -65) * mm});
            skLineSegment(sketch, "E31.5.0.6", {"start": v(-18.11, -59) * mm, "end": v(-15.23, -64) * mm});
            skLineSegment(sketch, "E31.5.0.7", {"start": v(-23.89, -59) * mm, "end": v(-18.11, -59) * mm});
            skPoint(sketch, "E31.5.0.8", {"position": v(-21, -59) * mm});
            skLineSegment(sketch, "E31.5.0.9", {"start": v(-18.11, -69) * mm, "end": v(-23.89, -69) * mm});
            skLineSegment(sketch, "E31.5.0.10", {"start": v(-23.89, -69) * mm, "end": v(-26.77, -64) * mm});
            skLineSegment(sketch, "E31.5.0.11", {"start": v(-26.77, -64) * mm, "end": v(-23.89, -59) * mm});
            skLineSegment(sketch, "E31.5.0.12", {"start": v(-13.5, -65) * mm, "end": v(-7.72, -65) * mm});
            skLineSegment(sketch, "E31.5.0.13", {"start": v(-7.72, -75) * mm, "end": v(-13.5, -75) * mm});
            skLineSegment(sketch, "E31.5.1.0", {"start": v(-7.72, -77) * mm, "end": v(-4.83, -82) * mm});
            skLineSegment(sketch, "E31.5.1.1", {"start": v(-13.5, -87) * mm, "end": v(-16.38, -82) * mm});
            skLineSegment(sketch, "E31.5.1.2", {"start": v(-16.38, -82) * mm, "end": v(-13.5, -77) * mm});
            skLineSegment(sketch, "E31.5.1.3", {"start": v(-15.23, -76) * mm, "end": v(-18.11, -81) * mm});
            skLineSegment(sketch, "E31.5.1.4", {"start": v(-4.83, -82) * mm, "end": v(-7.72, -87) * mm});
            skPoint(sketch, "E31.5.1.5", {"position": v(-10.6, -77) * mm});
            skLineSegment(sketch, "E31.5.1.6", {"start": v(-18.11, -71) * mm, "end": v(-15.23, -76) * mm});
            skLineSegment(sketch, "E31.5.1.7", {"start": v(-23.89, -71) * mm, "end": v(-18.11, -71) * mm});
            skPoint(sketch, "E31.5.1.8", {"position": v(-21, -71) * mm});
            skLineSegment(sketch, "E31.5.1.9", {"start": v(-18.11, -81) * mm, "end": v(-23.89, -81) * mm});
            skLineSegment(sketch, "E31.5.1.10", {"start": v(-23.89, -81) * mm, "end": v(-26.77, -76) * mm});
            skLineSegment(sketch, "E31.5.1.11", {"start": v(-26.77, -76) * mm, "end": v(-23.89, -71) * mm});
            skLineSegment(sketch, "E31.5.1.12", {"start": v(-13.5, -77) * mm, "end": v(-7.72, -77) * mm});
            skLineSegment(sketch, "E31.5.1.13", {"start": v(-7.72, -87) * mm, "end": v(-13.5, -87) * mm});
            skLineSegment(sketch, "E31.5.2.0", {"start": v(-7.72, -89) * mm, "end": v(-4.83, -94) * mm});
            skLineSegment(sketch, "E31.5.2.1", {"start": v(-13.5, -99) * mm, "end": v(-16.38, -94) * mm});
            skLineSegment(sketch, "E31.5.2.2", {"start": v(-16.38, -94) * mm, "end": v(-13.5, -89) * mm});
            skLineSegment(sketch, "E31.5.2.3", {"start": v(-15.23, -88) * mm, "end": v(-18.11, -93) * mm});
            skLineSegment(sketch, "E31.5.2.4", {"start": v(-4.83, -94) * mm, "end": v(-7.72, -99) * mm});
            skPoint(sketch, "E31.5.2.5", {"position": v(-10.6, -89) * mm});
            skLineSegment(sketch, "E31.5.2.6", {"start": v(-18.11, -83) * mm, "end": v(-15.23, -88) * mm});
            skLineSegment(sketch, "E31.5.2.7", {"start": v(-23.89, -83) * mm, "end": v(-18.11, -83) * mm});
            skPoint(sketch, "E31.5.2.8", {"position": v(-21, -83) * mm});
            skLineSegment(sketch, "E31.5.2.9", {"start": v(-18.11, -93) * mm, "end": v(-23.89, -93) * mm});
            skLineSegment(sketch, "E31.5.2.10", {"start": v(-23.89, -93) * mm, "end": v(-26.77, -88) * mm});
            skLineSegment(sketch, "E31.5.2.11", {"start": v(-26.77, -88) * mm, "end": v(-23.89, -83) * mm});
            skLineSegment(sketch, "E31.5.2.12", {"start": v(-13.5, -89) * mm, "end": v(-7.72, -89) * mm});
            skLineSegment(sketch, "E31.5.2.13", {"start": v(-7.72, -99) * mm, "end": v(-13.5, -99) * mm});
            skLineSegment(sketch, "E31.5.3.0", {"start": v(-7.72, -101) * mm, "end": v(-4.83, -106) * mm});
            skLineSegment(sketch, "E31.5.3.1", {"start": v(-13.5, -111) * mm, "end": v(-16.38, -106) * mm});
            skLineSegment(sketch, "E31.5.3.2", {"start": v(-16.38, -106) * mm, "end": v(-13.5, -101) * mm});
            skLineSegment(sketch, "E31.5.3.3", {"start": v(-15.23, -100) * mm, "end": v(-18.11, -105) * mm});
            skLineSegment(sketch, "E31.5.3.4", {"start": v(-4.83, -106) * mm, "end": v(-7.72, -111) * mm});
            skPoint(sketch, "E31.5.3.5", {"position": v(-10.6, -101) * mm});
            skLineSegment(sketch, "E31.5.3.6", {"start": v(-18.11, -95) * mm, "end": v(-15.23, -100) * mm});
            skLineSegment(sketch, "E31.5.3.7", {"start": v(-23.89, -95) * mm, "end": v(-18.11, -95) * mm});
            skPoint(sketch, "E31.5.3.8", {"position": v(-21, -95) * mm});
            skLineSegment(sketch, "E31.5.3.9", {"start": v(-18.11, -105) * mm, "end": v(-23.89, -105) * mm});
            skLineSegment(sketch, "E31.5.3.10", {"start": v(-23.89, -105) * mm, "end": v(-26.77, -100) * mm});
            skLineSegment(sketch, "E31.5.3.11", {"start": v(-26.77, -100) * mm, "end": v(-23.89, -95) * mm});
            skLineSegment(sketch, "E31.5.3.12", {"start": v(-13.5, -101) * mm, "end": v(-7.72, -101) * mm});
            skLineSegment(sketch, "E31.5.3.13", {"start": v(-7.72, -111) * mm, "end": v(-13.5, -111) * mm});
            skLineSegment(sketch, "E31.5.4.0", {"start": v(-7.72, -113) * mm, "end": v(-4.83, -118) * mm});
            skLineSegment(sketch, "E31.5.4.1", {"start": v(-13.5, -123) * mm, "end": v(-16.38, -118) * mm});
            skLineSegment(sketch, "E31.5.4.2", {"start": v(-16.38, -118) * mm, "end": v(-13.5, -113) * mm});
            skLineSegment(sketch, "E31.5.4.3", {"start": v(-15.23, -112) * mm, "end": v(-18.11, -117) * mm});
            skLineSegment(sketch, "E31.5.4.4", {"start": v(-4.83, -118) * mm, "end": v(-7.72, -123) * mm});
            skPoint(sketch, "E31.5.4.5", {"position": v(-10.6, -113) * mm});
            skLineSegment(sketch, "E31.5.4.6", {"start": v(-18.11, -107) * mm, "end": v(-15.23, -112) * mm});
            skLineSegment(sketch, "E31.5.4.7", {"start": v(-23.89, -107) * mm, "end": v(-18.11, -107) * mm});
            skPoint(sketch, "E31.5.4.8", {"position": v(-21, -107) * mm});
            skLineSegment(sketch, "E31.5.4.9", {"start": v(-18.11, -117) * mm, "end": v(-23.89, -117) * mm});
            skLineSegment(sketch, "E31.5.4.10", {"start": v(-23.89, -117) * mm, "end": v(-26.77, -112) * mm});
            skLineSegment(sketch, "E31.5.4.11", {"start": v(-26.77, -112) * mm, "end": v(-23.89, -107) * mm});
            skLineSegment(sketch, "E31.5.4.12", {"start": v(-13.5, -113) * mm, "end": v(-7.72, -113) * mm});
            skLineSegment(sketch, "E31.5.4.13", {"start": v(-7.72, -123) * mm, "end": v(-13.5, -123) * mm});
            skLineSegment(sketch, "E31.5.5.0", {"start": v(-7.72, -125) * mm, "end": v(-4.83, -130) * mm});
            skLineSegment(sketch, "E31.5.5.1", {"start": v(-13.5, -135) * mm, "end": v(-16.38, -130) * mm});
            skLineSegment(sketch, "E31.5.5.2", {"start": v(-16.38, -130) * mm, "end": v(-13.5, -125) * mm});
            skLineSegment(sketch, "E31.5.5.3", {"start": v(-15.23, -124) * mm, "end": v(-18.11, -129) * mm});
            skLineSegment(sketch, "E31.5.5.4", {"start": v(-4.83, -130) * mm, "end": v(-7.72, -135) * mm});
            skPoint(sketch, "E31.5.5.5", {"position": v(-10.6, -125) * mm});
            skLineSegment(sketch, "E31.5.5.6", {"start": v(-18.11, -119) * mm, "end": v(-15.23, -124) * mm});
            skLineSegment(sketch, "E31.5.5.7", {"start": v(-23.89, -119) * mm, "end": v(-18.11, -119) * mm});
            skPoint(sketch, "E31.5.5.8", {"position": v(-21, -119) * mm});
            skLineSegment(sketch, "E31.5.5.9", {"start": v(-18.11, -129) * mm, "end": v(-23.89, -129) * mm});
            skLineSegment(sketch, "E31.5.5.10", {"start": v(-23.89, -129) * mm, "end": v(-26.77, -124) * mm});
            skLineSegment(sketch, "E31.5.5.11", {"start": v(-26.77, -124) * mm, "end": v(-23.89, -119) * mm});
            skLineSegment(sketch, "E31.5.5.12", {"start": v(-13.5, -125) * mm, "end": v(-7.72, -125) * mm});
            skLineSegment(sketch, "E31.5.5.13", {"start": v(-7.72, -135) * mm, "end": v(-13.5, -135) * mm});
            skLineSegment(sketch, "E31.5.6.0", {"start": v(-7.72, -137) * mm, "end": v(-4.83, -142) * mm});
            skLineSegment(sketch, "E31.5.6.1", {"start": v(-13.5, -147) * mm, "end": v(-16.38, -142) * mm});
            skLineSegment(sketch, "E31.5.6.2", {"start": v(-16.38, -142) * mm, "end": v(-13.5, -137) * mm});
            skLineSegment(sketch, "E31.5.6.3", {"start": v(-15.23, -136) * mm, "end": v(-18.11, -141) * mm});
            skLineSegment(sketch, "E31.5.6.4", {"start": v(-4.83, -142) * mm, "end": v(-7.72, -147) * mm});
            skPoint(sketch, "E31.5.6.5", {"position": v(-10.6, -137) * mm});
            skLineSegment(sketch, "E31.5.6.6", {"start": v(-18.11, -131) * mm, "end": v(-15.23, -136) * mm});
            skLineSegment(sketch, "E31.5.6.7", {"start": v(-23.89, -131) * mm, "end": v(-18.11, -131) * mm});
            skPoint(sketch, "E31.5.6.8", {"position": v(-21, -131) * mm});
            skLineSegment(sketch, "E31.5.6.9", {"start": v(-18.11, -141) * mm, "end": v(-23.89, -141) * mm});
            skLineSegment(sketch, "E31.5.6.10", {"start": v(-23.89, -141) * mm, "end": v(-26.77, -136) * mm});
            skLineSegment(sketch, "E31.5.6.11", {"start": v(-26.77, -136) * mm, "end": v(-23.89, -131) * mm});
            skLineSegment(sketch, "E31.5.6.12", {"start": v(-13.5, -137) * mm, "end": v(-7.72, -137) * mm});
            skLineSegment(sketch, "E31.5.6.13", {"start": v(-7.72, -147) * mm, "end": v(-13.5, -147) * mm});
            skLineSegment(sketch, "E31.5.7.0", {"start": v(-7.72, -149) * mm, "end": v(-4.83, -154) * mm});
            skLineSegment(sketch, "E31.5.7.1", {"start": v(-13.5, -159) * mm, "end": v(-16.38, -154) * mm});
            skLineSegment(sketch, "E31.5.7.2", {"start": v(-16.38, -154) * mm, "end": v(-13.5, -149) * mm});
            skLineSegment(sketch, "E31.5.7.3", {"start": v(-15.23, -148) * mm, "end": v(-18.11, -153) * mm});
            skLineSegment(sketch, "E31.5.7.4", {"start": v(-4.83, -154) * mm, "end": v(-7.72, -159) * mm});
            skPoint(sketch, "E31.5.7.5", {"position": v(-10.6, -149) * mm});
            skLineSegment(sketch, "E31.5.7.6", {"start": v(-18.11, -143) * mm, "end": v(-15.23, -148) * mm});
            skLineSegment(sketch, "E31.5.7.7", {"start": v(-23.89, -143) * mm, "end": v(-18.11, -143) * mm});
            skPoint(sketch, "E31.5.7.8", {"position": v(-21, -143) * mm});
            skLineSegment(sketch, "E31.5.7.9", {"start": v(-18.11, -153) * mm, "end": v(-23.89, -153) * mm});
            skLineSegment(sketch, "E31.5.7.10", {"start": v(-23.89, -153) * mm, "end": v(-26.77, -148) * mm});
            skLineSegment(sketch, "E31.5.7.11", {"start": v(-26.77, -148) * mm, "end": v(-23.89, -143) * mm});
            skLineSegment(sketch, "E31.5.7.12", {"start": v(-13.5, -149) * mm, "end": v(-7.72, -149) * mm});
            skLineSegment(sketch, "E31.5.7.13", {"start": v(-7.72, -159) * mm, "end": v(-13.5, -159) * mm});
            skLineSegment(sketch, "E31.5.8.0", {"start": v(-7.72, -161) * mm, "end": v(-4.83, -166) * mm});
            skLineSegment(sketch, "E31.5.8.1", {"start": v(-13.5, -171) * mm, "end": v(-16.38, -166) * mm});
            skLineSegment(sketch, "E31.5.8.2", {"start": v(-16.38, -166) * mm, "end": v(-13.5, -161) * mm});
            skLineSegment(sketch, "E31.5.8.3", {"start": v(-15.23, -160) * mm, "end": v(-18.11, -165) * mm});
            skLineSegment(sketch, "E31.5.8.4", {"start": v(-4.83, -166) * mm, "end": v(-7.72, -171) * mm});
            skPoint(sketch, "E31.5.8.5", {"position": v(-10.6, -161) * mm});
            skLineSegment(sketch, "E31.5.8.6", {"start": v(-18.11, -155) * mm, "end": v(-15.23, -160) * mm});
            skLineSegment(sketch, "E31.5.8.7", {"start": v(-23.89, -155) * mm, "end": v(-18.11, -155) * mm});
            skPoint(sketch, "E31.5.8.8", {"position": v(-21, -155) * mm});
            skLineSegment(sketch, "E31.5.8.9", {"start": v(-18.11, -165) * mm, "end": v(-23.89, -165) * mm});
            skLineSegment(sketch, "E31.5.8.10", {"start": v(-23.89, -165) * mm, "end": v(-26.77, -160) * mm});
            skLineSegment(sketch, "E31.5.8.11", {"start": v(-26.77, -160) * mm, "end": v(-23.89, -155) * mm});
            skLineSegment(sketch, "E31.5.8.12", {"start": v(-13.5, -161) * mm, "end": v(-7.72, -161) * mm});
            skLineSegment(sketch, "E31.5.8.13", {"start": v(-7.72, -171) * mm, "end": v(-13.5, -171) * mm});
            skLineSegment(sketch, "E31.5.9.0", {"start": v(-7.72, -173) * mm, "end": v(-4.83, -178) * mm});
            skLineSegment(sketch, "E31.5.9.1", {"start": v(-13.5, -183) * mm, "end": v(-16.38, -178) * mm});
            skLineSegment(sketch, "E31.5.9.2", {"start": v(-16.38, -178) * mm, "end": v(-13.5, -173) * mm});
            skLineSegment(sketch, "E31.5.9.3", {"start": v(-15.23, -172) * mm, "end": v(-18.11, -177) * mm});
            skLineSegment(sketch, "E31.5.9.4", {"start": v(-4.83, -178) * mm, "end": v(-7.72, -183) * mm});
            skPoint(sketch, "E31.5.9.5", {"position": v(-10.6, -173) * mm});
            skLineSegment(sketch, "E31.5.9.6", {"start": v(-18.11, -167) * mm, "end": v(-15.23, -172) * mm});
            skLineSegment(sketch, "E31.5.9.7", {"start": v(-23.89, -167) * mm, "end": v(-18.11, -167) * mm});
            skPoint(sketch, "E31.5.9.8", {"position": v(-21, -167) * mm});
            skLineSegment(sketch, "E31.5.9.9", {"start": v(-18.11, -177) * mm, "end": v(-23.89, -177) * mm});
            skLineSegment(sketch, "E31.5.9.10", {"start": v(-23.89, -177) * mm, "end": v(-26.77, -172) * mm});
            skLineSegment(sketch, "E31.5.9.11", {"start": v(-26.77, -172) * mm, "end": v(-23.89, -167) * mm});
            skLineSegment(sketch, "E31.5.9.12", {"start": v(-13.5, -173) * mm, "end": v(-7.72, -173) * mm});
            skLineSegment(sketch, "E31.5.9.13", {"start": v(-7.72, -183) * mm, "end": v(-13.5, -183) * mm});
            skLineSegment(sketch, "E31.5.10.0", {"start": v(-7.72, -185) * mm, "end": v(-4.83, -190) * mm});
            skLineSegment(sketch, "E31.5.10.1", {"start": v(-13.5, -195) * mm, "end": v(-16.38, -190) * mm});
            skLineSegment(sketch, "E31.5.10.2", {"start": v(-16.38, -190) * mm, "end": v(-13.5, -185) * mm});
            skLineSegment(sketch, "E31.5.10.3", {"start": v(-15.23, -184) * mm, "end": v(-18.11, -189) * mm});
            skLineSegment(sketch, "E31.5.10.4", {"start": v(-4.83, -190) * mm, "end": v(-7.72, -195) * mm});
            skPoint(sketch, "E31.5.10.5", {"position": v(-10.6, -185) * mm});
            skLineSegment(sketch, "E31.5.10.6", {"start": v(-18.11, -179) * mm, "end": v(-15.23, -184) * mm});
            skLineSegment(sketch, "E31.5.10.7", {"start": v(-23.89, -179) * mm, "end": v(-18.11, -179) * mm});
            skPoint(sketch, "E31.5.10.8", {"position": v(-21, -179) * mm});
            skLineSegment(sketch, "E31.5.10.9", {"start": v(-18.11, -189) * mm, "end": v(-23.89, -189) * mm});
            skLineSegment(sketch, "E31.5.10.10", {"start": v(-23.89, -189) * mm, "end": v(-26.77, -184) * mm});
            skLineSegment(sketch, "E31.5.10.11", {"start": v(-26.77, -184) * mm, "end": v(-23.89, -179) * mm});
            skLineSegment(sketch, "E31.5.10.12", {"start": v(-13.5, -185) * mm, "end": v(-7.72, -185) * mm});
            skLineSegment(sketch, "E31.5.10.13", {"start": v(-7.72, -195) * mm, "end": v(-13.5, -195) * mm});
            skLineSegment(sketch, "E31.5.11.0", {"start": v(-7.72, -197) * mm, "end": v(-4.83, -202) * mm});
            skLineSegment(sketch, "E31.5.11.1", {"start": v(-13.5, -207) * mm, "end": v(-16.38, -202) * mm});
            skLineSegment(sketch, "E31.5.11.2", {"start": v(-16.38, -202) * mm, "end": v(-13.5, -197) * mm});
            skLineSegment(sketch, "E31.5.11.3", {"start": v(-15.23, -196) * mm, "end": v(-18.11, -201) * mm});
            skLineSegment(sketch, "E31.5.11.4", {"start": v(-4.83, -202) * mm, "end": v(-7.72, -207) * mm});
            skPoint(sketch, "E31.5.11.5", {"position": v(-10.6, -197) * mm});
            skLineSegment(sketch, "E31.5.11.6", {"start": v(-18.11, -191) * mm, "end": v(-15.23, -196) * mm});
            skLineSegment(sketch, "E31.5.11.7", {"start": v(-23.89, -191) * mm, "end": v(-18.11, -191) * mm});
            skPoint(sketch, "E31.5.11.8", {"position": v(-21, -191) * mm});
            skLineSegment(sketch, "E31.5.11.9", {"start": v(-18.11, -201) * mm, "end": v(-23.89, -201) * mm});
            skLineSegment(sketch, "E31.5.11.10", {"start": v(-23.89, -201) * mm, "end": v(-26.77, -196) * mm});
            skLineSegment(sketch, "E31.5.11.11", {"start": v(-26.77, -196) * mm, "end": v(-23.89, -191) * mm});
            skLineSegment(sketch, "E31.5.11.12", {"start": v(-13.5, -197) * mm, "end": v(-7.72, -197) * mm});
            skLineSegment(sketch, "E31.5.11.13", {"start": v(-7.72, -207) * mm, "end": v(-13.5, -207) * mm});
            skLineSegment(sketch, "E31.5.12.0", {"start": v(-7.72, -209) * mm, "end": v(-4.83, -214) * mm});
            skLineSegment(sketch, "E31.5.12.1", {"start": v(-13.5, -219) * mm, "end": v(-16.38, -214) * mm});
            skLineSegment(sketch, "E31.5.12.2", {"start": v(-16.38, -214) * mm, "end": v(-13.5, -209) * mm});
            skLineSegment(sketch, "E31.5.12.3", {"start": v(-15.23, -208) * mm, "end": v(-18.11, -213) * mm});
            skLineSegment(sketch, "E31.5.12.4", {"start": v(-4.83, -214) * mm, "end": v(-7.72, -219) * mm});
            skPoint(sketch, "E31.5.12.5", {"position": v(-10.6, -209) * mm});
            skLineSegment(sketch, "E31.5.12.6", {"start": v(-18.11, -203) * mm, "end": v(-15.23, -208) * mm});
            skLineSegment(sketch, "E31.5.12.7", {"start": v(-23.89, -203) * mm, "end": v(-18.11, -203) * mm});
            skPoint(sketch, "E31.5.12.8", {"position": v(-21, -203) * mm});
            skLineSegment(sketch, "E31.5.12.9", {"start": v(-18.11, -213) * mm, "end": v(-23.89, -213) * mm});
            skLineSegment(sketch, "E31.5.12.10", {"start": v(-23.89, -213) * mm, "end": v(-26.77, -208) * mm});
            skLineSegment(sketch, "E31.5.12.11", {"start": v(-26.77, -208) * mm, "end": v(-23.89, -203) * mm});
            skLineSegment(sketch, "E31.5.12.12", {"start": v(-13.5, -209) * mm, "end": v(-7.72, -209) * mm});
            skLineSegment(sketch, "E31.5.12.13", {"start": v(-7.72, -219) * mm, "end": v(-13.5, -219) * mm});
            skLineSegment(sketch, "E31.5.13.0", {"start": v(-7.72, -221) * mm, "end": v(-4.83, -226) * mm});
            skLineSegment(sketch, "E31.5.13.1", {"start": v(-13.5, -231) * mm, "end": v(-16.38, -226) * mm});
            skLineSegment(sketch, "E31.5.13.2", {"start": v(-16.38, -226) * mm, "end": v(-13.5, -221) * mm});
            skLineSegment(sketch, "E31.5.13.3", {"start": v(-15.23, -220) * mm, "end": v(-18.11, -225) * mm});
            skLineSegment(sketch, "E31.5.13.4", {"start": v(-4.83, -226) * mm, "end": v(-7.72, -231) * mm});
            skPoint(sketch, "E31.5.13.5", {"position": v(-10.6, -221) * mm});
            skLineSegment(sketch, "E31.5.13.6", {"start": v(-18.11, -215) * mm, "end": v(-15.23, -220) * mm});
            skLineSegment(sketch, "E31.5.13.7", {"start": v(-23.89, -215) * mm, "end": v(-18.11, -215) * mm});
            skPoint(sketch, "E31.5.13.8", {"position": v(-21, -215) * mm});
            skLineSegment(sketch, "E31.5.13.9", {"start": v(-18.11, -225) * mm, "end": v(-23.89, -225) * mm});
            skLineSegment(sketch, "E31.5.13.10", {"start": v(-23.89, -225) * mm, "end": v(-26.77, -220) * mm});
            skLineSegment(sketch, "E31.5.13.11", {"start": v(-26.77, -220) * mm, "end": v(-23.89, -215) * mm});
            skLineSegment(sketch, "E31.5.13.12", {"start": v(-13.5, -221) * mm, "end": v(-7.72, -221) * mm});
            skLineSegment(sketch, "E31.5.13.13", {"start": v(-7.72, -231) * mm, "end": v(-13.5, -231) * mm});
            skLineSegment(sketch, "E31.5.14.0", {"start": v(-7.72, -233) * mm, "end": v(-4.83, -238) * mm});
            skLineSegment(sketch, "E31.5.14.1", {"start": v(-13.5, -243) * mm, "end": v(-16.38, -238) * mm});
            skLineSegment(sketch, "E31.5.14.2", {"start": v(-16.38, -238) * mm, "end": v(-13.5, -233) * mm});
            skLineSegment(sketch, "E31.5.14.3", {"start": v(-15.23, -232) * mm, "end": v(-18.11, -237) * mm});
            skLineSegment(sketch, "E31.5.14.4", {"start": v(-4.83, -238) * mm, "end": v(-7.72, -243) * mm});
            skPoint(sketch, "E31.5.14.5", {"position": v(-10.6, -233) * mm});
            skLineSegment(sketch, "E31.5.14.6", {"start": v(-18.11, -227) * mm, "end": v(-15.23, -232) * mm});
            skLineSegment(sketch, "E31.5.14.7", {"start": v(-23.89, -227) * mm, "end": v(-18.11, -227) * mm});
            skPoint(sketch, "E31.5.14.8", {"position": v(-21, -227) * mm});
            skLineSegment(sketch, "E31.5.14.9", {"start": v(-18.11, -237) * mm, "end": v(-23.89, -237) * mm});
            skLineSegment(sketch, "E31.5.14.10", {"start": v(-23.89, -237) * mm, "end": v(-26.77, -232) * mm});
            skLineSegment(sketch, "E31.5.14.11", {"start": v(-26.77, -232) * mm, "end": v(-23.89, -227) * mm});
            skLineSegment(sketch, "E31.5.14.12", {"start": v(-13.5, -233) * mm, "end": v(-7.72, -233) * mm});
            skLineSegment(sketch, "E31.5.14.13", {"start": v(-7.72, -243) * mm, "end": v(-13.5, -243) * mm});
            skLineSegment(sketch, "E31.5.15.0", {"start": v(-7.72, -245) * mm, "end": v(-4.83, -250) * mm});
            skLineSegment(sketch, "E31.5.15.1", {"start": v(-13.5, -255) * mm, "end": v(-16.38, -250) * mm});
            skLineSegment(sketch, "E31.5.15.2", {"start": v(-16.38, -250) * mm, "end": v(-13.5, -245) * mm});
            skLineSegment(sketch, "E31.5.15.3", {"start": v(-15.23, -244) * mm, "end": v(-18.11, -249) * mm});
            skLineSegment(sketch, "E31.5.15.4", {"start": v(-4.83, -250) * mm, "end": v(-7.72, -255) * mm});
            skPoint(sketch, "E31.5.15.5", {"position": v(-10.6, -245) * mm});
            skLineSegment(sketch, "E31.5.15.6", {"start": v(-18.11, -239) * mm, "end": v(-15.23, -244) * mm});
            skLineSegment(sketch, "E31.5.15.7", {"start": v(-23.89, -239) * mm, "end": v(-18.11, -239) * mm});
            skPoint(sketch, "E31.5.15.8", {"position": v(-21, -239) * mm});
            skLineSegment(sketch, "E31.5.15.9", {"start": v(-18.11, -249) * mm, "end": v(-23.89, -249) * mm});
            skLineSegment(sketch, "E31.5.15.10", {"start": v(-23.89, -249) * mm, "end": v(-26.77, -244) * mm});
            skLineSegment(sketch, "E31.5.15.11", {"start": v(-26.77, -244) * mm, "end": v(-23.89, -239) * mm});
            skLineSegment(sketch, "E31.5.15.12", {"start": v(-13.5, -245) * mm, "end": v(-7.72, -245) * mm});
            skLineSegment(sketch, "E31.5.15.13", {"start": v(-7.72, -255) * mm, "end": v(-13.5, -255) * mm});
            skLineSegment(sketch, "E31.5.16.3", {"start": v(-15.23, -256) * mm, "end": v(-18.11, -261) * mm});
            skLineSegment(sketch, "E31.5.16.6", {"start": v(-18.11, -251) * mm, "end": v(-15.23, -256) * mm});
            skLineSegment(sketch, "E31.5.16.7", {"start": v(-23.89, -251) * mm, "end": v(-18.11, -251) * mm});
            skPoint(sketch, "E31.5.16.8", {"position": v(-21, -251) * mm});
            skLineSegment(sketch, "E31.5.16.9", {"start": v(-18.11, -261) * mm, "end": v(-23.89, -261) * mm});
            skLineSegment(sketch, "E31.5.16.10", {"start": v(-23.89, -261) * mm, "end": v(-26.77, -256) * mm});
            skLineSegment(sketch, "E31.5.16.11", {"start": v(-26.77, -256) * mm, "end": v(-23.89, -251) * mm});
            skLineSegment(sketch, "E31.6.0.0", {"start": v(-28.72, -65) * mm, "end": v(-25.83, -70) * mm});
            skLineSegment(sketch, "E31.6.0.1", {"start": v(-34.5, -75) * mm, "end": v(-37.38, -70) * mm});
            skLineSegment(sketch, "E31.6.0.2", {"start": v(-37.38, -70) * mm, "end": v(-34.5, -65) * mm});
            skLineSegment(sketch, "E31.6.0.3", {"start": v(-36.23, -64) * mm, "end": v(-39.11, -69) * mm});
            skLineSegment(sketch, "E31.6.0.4", {"start": v(-25.83, -70) * mm, "end": v(-28.72, -75) * mm});
            skPoint(sketch, "E31.6.0.5", {"position": v(-31.6, -65) * mm});
            skLineSegment(sketch, "E31.6.0.6", {"start": v(-39.11, -59) * mm, "end": v(-36.23, -64) * mm});
            skLineSegment(sketch, "E31.6.0.7", {"start": v(-44.89, -59) * mm, "end": v(-39.11, -59) * mm});
            skPoint(sketch, "E31.6.0.8", {"position": v(-42, -59) * mm});
            skLineSegment(sketch, "E31.6.0.9", {"start": v(-39.11, -69) * mm, "end": v(-44.89, -69) * mm});
            skLineSegment(sketch, "E31.6.0.10", {"start": v(-44.89, -69) * mm, "end": v(-47.77, -64) * mm});
            skLineSegment(sketch, "E31.6.0.11", {"start": v(-47.77, -64) * mm, "end": v(-44.89, -59) * mm});
            skLineSegment(sketch, "E31.6.0.12", {"start": v(-34.5, -65) * mm, "end": v(-28.72, -65) * mm});
            skLineSegment(sketch, "E31.6.0.13", {"start": v(-28.72, -75) * mm, "end": v(-34.5, -75) * mm});
            skLineSegment(sketch, "E31.6.1.0", {"start": v(-28.72, -77) * mm, "end": v(-25.83, -82) * mm});
            skLineSegment(sketch, "E31.6.1.1", {"start": v(-34.5, -87) * mm, "end": v(-37.38, -82) * mm});
            skLineSegment(sketch, "E31.6.1.2", {"start": v(-37.38, -82) * mm, "end": v(-34.5, -77) * mm});
            skLineSegment(sketch, "E31.6.1.3", {"start": v(-36.23, -76) * mm, "end": v(-39.11, -81) * mm});
            skLineSegment(sketch, "E31.6.1.4", {"start": v(-25.83, -82) * mm, "end": v(-28.72, -87) * mm});
            skPoint(sketch, "E31.6.1.5", {"position": v(-31.6, -77) * mm});
            skLineSegment(sketch, "E31.6.1.6", {"start": v(-39.11, -71) * mm, "end": v(-36.23, -76) * mm});
            skLineSegment(sketch, "E31.6.1.7", {"start": v(-44.89, -71) * mm, "end": v(-39.11, -71) * mm});
            skPoint(sketch, "E31.6.1.8", {"position": v(-42, -71) * mm});
            skLineSegment(sketch, "E31.6.1.9", {"start": v(-39.11, -81) * mm, "end": v(-44.89, -81) * mm});
            skLineSegment(sketch, "E31.6.1.10", {"start": v(-44.89, -81) * mm, "end": v(-47.77, -76) * mm});
            skLineSegment(sketch, "E31.6.1.11", {"start": v(-47.77, -76) * mm, "end": v(-44.89, -71) * mm});
            skLineSegment(sketch, "E31.6.1.12", {"start": v(-34.5, -77) * mm, "end": v(-28.72, -77) * mm});
            skLineSegment(sketch, "E31.6.1.13", {"start": v(-28.72, -87) * mm, "end": v(-34.5, -87) * mm});
            skLineSegment(sketch, "E31.6.2.0", {"start": v(-28.72, -89) * mm, "end": v(-25.83, -94) * mm});
            skLineSegment(sketch, "E31.6.2.1", {"start": v(-34.5, -99) * mm, "end": v(-37.38, -94) * mm});
            skLineSegment(sketch, "E31.6.2.2", {"start": v(-37.38, -94) * mm, "end": v(-34.5, -89) * mm});
            skLineSegment(sketch, "E31.6.2.3", {"start": v(-36.23, -88) * mm, "end": v(-39.11, -93) * mm});
            skLineSegment(sketch, "E31.6.2.4", {"start": v(-25.83, -94) * mm, "end": v(-28.72, -99) * mm});
            skPoint(sketch, "E31.6.2.5", {"position": v(-31.6, -89) * mm});
            skLineSegment(sketch, "E31.6.2.6", {"start": v(-39.11, -83) * mm, "end": v(-36.23, -88) * mm});
            skLineSegment(sketch, "E31.6.2.7", {"start": v(-44.89, -83) * mm, "end": v(-39.11, -83) * mm});
            skPoint(sketch, "E31.6.2.8", {"position": v(-42, -83) * mm});
            skLineSegment(sketch, "E31.6.2.9", {"start": v(-39.11, -93) * mm, "end": v(-44.89, -93) * mm});
            skLineSegment(sketch, "E31.6.2.10", {"start": v(-44.89, -93) * mm, "end": v(-47.77, -88) * mm});
            skLineSegment(sketch, "E31.6.2.11", {"start": v(-47.77, -88) * mm, "end": v(-44.89, -83) * mm});
            skLineSegment(sketch, "E31.6.2.12", {"start": v(-34.5, -89) * mm, "end": v(-28.72, -89) * mm});
            skLineSegment(sketch, "E31.6.2.13", {"start": v(-28.72, -99) * mm, "end": v(-34.5, -99) * mm});
            skLineSegment(sketch, "E31.6.3.0", {"start": v(-28.72, -101) * mm, "end": v(-25.83, -106) * mm});
            skLineSegment(sketch, "E31.6.3.1", {"start": v(-34.5, -111) * mm, "end": v(-37.38, -106) * mm});
            skLineSegment(sketch, "E31.6.3.2", {"start": v(-37.38, -106) * mm, "end": v(-34.5, -101) * mm});
            skLineSegment(sketch, "E31.6.3.3", {"start": v(-36.23, -100) * mm, "end": v(-39.11, -105) * mm});
            skLineSegment(sketch, "E31.6.3.4", {"start": v(-25.83, -106) * mm, "end": v(-28.72, -111) * mm});
            skPoint(sketch, "E31.6.3.5", {"position": v(-31.6, -101) * mm});
            skLineSegment(sketch, "E31.6.3.6", {"start": v(-39.11, -95) * mm, "end": v(-36.23, -100) * mm});
            skLineSegment(sketch, "E31.6.3.7", {"start": v(-44.89, -95) * mm, "end": v(-39.11, -95) * mm});
            skPoint(sketch, "E31.6.3.8", {"position": v(-42, -95) * mm});
            skLineSegment(sketch, "E31.6.3.9", {"start": v(-39.11, -105) * mm, "end": v(-44.89, -105) * mm});
            skLineSegment(sketch, "E31.6.3.10", {"start": v(-44.89, -105) * mm, "end": v(-47.77, -100) * mm});
            skLineSegment(sketch, "E31.6.3.11", {"start": v(-47.77, -100) * mm, "end": v(-44.89, -95) * mm});
            skLineSegment(sketch, "E31.6.3.12", {"start": v(-34.5, -101) * mm, "end": v(-28.72, -101) * mm});
            skLineSegment(sketch, "E31.6.3.13", {"start": v(-28.72, -111) * mm, "end": v(-34.5, -111) * mm});
            skLineSegment(sketch, "E31.6.4.0", {"start": v(-28.72, -113) * mm, "end": v(-25.83, -118) * mm});
            skLineSegment(sketch, "E31.6.4.1", {"start": v(-34.5, -123) * mm, "end": v(-37.38, -118) * mm});
            skLineSegment(sketch, "E31.6.4.2", {"start": v(-37.38, -118) * mm, "end": v(-34.5, -113) * mm});
            skLineSegment(sketch, "E31.6.4.3", {"start": v(-36.23, -112) * mm, "end": v(-39.11, -117) * mm});
            skLineSegment(sketch, "E31.6.4.4", {"start": v(-25.83, -118) * mm, "end": v(-28.72, -123) * mm});
            skPoint(sketch, "E31.6.4.5", {"position": v(-31.6, -113) * mm});
            skLineSegment(sketch, "E31.6.4.6", {"start": v(-39.11, -107) * mm, "end": v(-36.23, -112) * mm});
            skLineSegment(sketch, "E31.6.4.7", {"start": v(-44.89, -107) * mm, "end": v(-39.11, -107) * mm});
            skPoint(sketch, "E31.6.4.8", {"position": v(-42, -107) * mm});
            skLineSegment(sketch, "E31.6.4.9", {"start": v(-39.11, -117) * mm, "end": v(-44.89, -117) * mm});
            skLineSegment(sketch, "E31.6.4.10", {"start": v(-44.89, -117) * mm, "end": v(-47.77, -112) * mm});
            skLineSegment(sketch, "E31.6.4.11", {"start": v(-47.77, -112) * mm, "end": v(-44.89, -107) * mm});
            skLineSegment(sketch, "E31.6.4.12", {"start": v(-34.5, -113) * mm, "end": v(-28.72, -113) * mm});
            skLineSegment(sketch, "E31.6.4.13", {"start": v(-28.72, -123) * mm, "end": v(-34.5, -123) * mm});
            skLineSegment(sketch, "E31.6.5.0", {"start": v(-28.72, -125) * mm, "end": v(-25.83, -130) * mm});
            skLineSegment(sketch, "E31.6.5.1", {"start": v(-34.5, -135) * mm, "end": v(-37.38, -130) * mm});
            skLineSegment(sketch, "E31.6.5.2", {"start": v(-37.38, -130) * mm, "end": v(-34.5, -125) * mm});
            skLineSegment(sketch, "E31.6.5.3", {"start": v(-36.23, -124) * mm, "end": v(-39.11, -129) * mm});
            skLineSegment(sketch, "E31.6.5.4", {"start": v(-25.83, -130) * mm, "end": v(-28.72, -135) * mm});
            skPoint(sketch, "E31.6.5.5", {"position": v(-31.6, -125) * mm});
            skLineSegment(sketch, "E31.6.5.6", {"start": v(-39.11, -119) * mm, "end": v(-36.23, -124) * mm});
            skLineSegment(sketch, "E31.6.5.7", {"start": v(-44.89, -119) * mm, "end": v(-39.11, -119) * mm});
            skPoint(sketch, "E31.6.5.8", {"position": v(-42, -119) * mm});
            skLineSegment(sketch, "E31.6.5.9", {"start": v(-39.11, -129) * mm, "end": v(-44.89, -129) * mm});
            skLineSegment(sketch, "E31.6.5.10", {"start": v(-44.89, -129) * mm, "end": v(-47.77, -124) * mm});
            skLineSegment(sketch, "E31.6.5.11", {"start": v(-47.77, -124) * mm, "end": v(-44.89, -119) * mm});
            skLineSegment(sketch, "E31.6.5.12", {"start": v(-34.5, -125) * mm, "end": v(-28.72, -125) * mm});
            skLineSegment(sketch, "E31.6.5.13", {"start": v(-28.72, -135) * mm, "end": v(-34.5, -135) * mm});
            skLineSegment(sketch, "E31.6.6.0", {"start": v(-28.72, -137) * mm, "end": v(-25.83, -142) * mm});
            skLineSegment(sketch, "E31.6.6.1", {"start": v(-34.5, -147) * mm, "end": v(-37.38, -142) * mm});
            skLineSegment(sketch, "E31.6.6.2", {"start": v(-37.38, -142) * mm, "end": v(-34.5, -137) * mm});
            skLineSegment(sketch, "E31.6.6.3", {"start": v(-36.23, -136) * mm, "end": v(-39.11, -141) * mm});
            skLineSegment(sketch, "E31.6.6.4", {"start": v(-25.83, -142) * mm, "end": v(-28.72, -147) * mm});
            skPoint(sketch, "E31.6.6.5", {"position": v(-31.6, -137) * mm});
            skLineSegment(sketch, "E31.6.6.6", {"start": v(-39.11, -131) * mm, "end": v(-36.23, -136) * mm});
            skLineSegment(sketch, "E31.6.6.7", {"start": v(-44.89, -131) * mm, "end": v(-39.11, -131) * mm});
            skPoint(sketch, "E31.6.6.8", {"position": v(-42, -131) * mm});
            skLineSegment(sketch, "E31.6.6.9", {"start": v(-39.11, -141) * mm, "end": v(-44.89, -141) * mm});
            skLineSegment(sketch, "E31.6.6.10", {"start": v(-44.89, -141) * mm, "end": v(-47.77, -136) * mm});
            skLineSegment(sketch, "E31.6.6.11", {"start": v(-47.77, -136) * mm, "end": v(-44.89, -131) * mm});
            skLineSegment(sketch, "E31.6.6.12", {"start": v(-34.5, -137) * mm, "end": v(-28.72, -137) * mm});
            skLineSegment(sketch, "E31.6.6.13", {"start": v(-28.72, -147) * mm, "end": v(-34.5, -147) * mm});
            skLineSegment(sketch, "E31.6.7.0", {"start": v(-28.72, -149) * mm, "end": v(-25.83, -154) * mm});
            skLineSegment(sketch, "E31.6.7.1", {"start": v(-34.5, -159) * mm, "end": v(-37.38, -154) * mm});
            skLineSegment(sketch, "E31.6.7.2", {"start": v(-37.38, -154) * mm, "end": v(-34.5, -149) * mm});
            skLineSegment(sketch, "E31.6.7.3", {"start": v(-36.23, -148) * mm, "end": v(-39.11, -153) * mm});
            skLineSegment(sketch, "E31.6.7.4", {"start": v(-25.83, -154) * mm, "end": v(-28.72, -159) * mm});
            skPoint(sketch, "E31.6.7.5", {"position": v(-31.6, -149) * mm});
            skLineSegment(sketch, "E31.6.7.6", {"start": v(-39.11, -143) * mm, "end": v(-36.23, -148) * mm});
            skLineSegment(sketch, "E31.6.7.7", {"start": v(-44.89, -143) * mm, "end": v(-39.11, -143) * mm});
            skPoint(sketch, "E31.6.7.8", {"position": v(-42, -143) * mm});
            skLineSegment(sketch, "E31.6.7.9", {"start": v(-39.11, -153) * mm, "end": v(-44.89, -153) * mm});
            skLineSegment(sketch, "E31.6.7.10", {"start": v(-44.89, -153) * mm, "end": v(-47.77, -148) * mm});
            skLineSegment(sketch, "E31.6.7.11", {"start": v(-47.77, -148) * mm, "end": v(-44.89, -143) * mm});
            skLineSegment(sketch, "E31.6.7.12", {"start": v(-34.5, -149) * mm, "end": v(-28.72, -149) * mm});
            skLineSegment(sketch, "E31.6.7.13", {"start": v(-28.72, -159) * mm, "end": v(-34.5, -159) * mm});
            skLineSegment(sketch, "E31.6.8.0", {"start": v(-28.72, -161) * mm, "end": v(-25.83, -166) * mm});
            skLineSegment(sketch, "E31.6.8.1", {"start": v(-34.5, -171) * mm, "end": v(-37.38, -166) * mm});
            skLineSegment(sketch, "E31.6.8.2", {"start": v(-37.38, -166) * mm, "end": v(-34.5, -161) * mm});
            skLineSegment(sketch, "E31.6.8.3", {"start": v(-36.23, -160) * mm, "end": v(-39.11, -165) * mm});
            skLineSegment(sketch, "E31.6.8.4", {"start": v(-25.83, -166) * mm, "end": v(-28.72, -171) * mm});
            skPoint(sketch, "E31.6.8.5", {"position": v(-31.6, -161) * mm});
            skLineSegment(sketch, "E31.6.8.6", {"start": v(-39.11, -155) * mm, "end": v(-36.23, -160) * mm});
            skLineSegment(sketch, "E31.6.8.7", {"start": v(-44.89, -155) * mm, "end": v(-39.11, -155) * mm});
            skPoint(sketch, "E31.6.8.8", {"position": v(-42, -155) * mm});
            skLineSegment(sketch, "E31.6.8.9", {"start": v(-39.11, -165) * mm, "end": v(-44.89, -165) * mm});
            skLineSegment(sketch, "E31.6.8.10", {"start": v(-44.89, -165) * mm, "end": v(-47.77, -160) * mm});
            skLineSegment(sketch, "E31.6.8.11", {"start": v(-47.77, -160) * mm, "end": v(-44.89, -155) * mm});
            skLineSegment(sketch, "E31.6.8.12", {"start": v(-34.5, -161) * mm, "end": v(-28.72, -161) * mm});
            skLineSegment(sketch, "E31.6.8.13", {"start": v(-28.72, -171) * mm, "end": v(-34.5, -171) * mm});
            skLineSegment(sketch, "E31.6.9.0", {"start": v(-28.72, -173) * mm, "end": v(-25.83, -178) * mm});
            skLineSegment(sketch, "E31.6.9.1", {"start": v(-34.5, -183) * mm, "end": v(-37.38, -178) * mm});
            skLineSegment(sketch, "E31.6.9.2", {"start": v(-37.38, -178) * mm, "end": v(-34.5, -173) * mm});
            skLineSegment(sketch, "E31.6.9.3", {"start": v(-36.23, -172) * mm, "end": v(-39.11, -177) * mm});
            skLineSegment(sketch, "E31.6.9.4", {"start": v(-25.83, -178) * mm, "end": v(-28.72, -183) * mm});
            skPoint(sketch, "E31.6.9.5", {"position": v(-31.6, -173) * mm});
            skLineSegment(sketch, "E31.6.9.6", {"start": v(-39.11, -167) * mm, "end": v(-36.23, -172) * mm});
            skLineSegment(sketch, "E31.6.9.7", {"start": v(-44.89, -167) * mm, "end": v(-39.11, -167) * mm});
            skPoint(sketch, "E31.6.9.8", {"position": v(-42, -167) * mm});
            skLineSegment(sketch, "E31.6.9.9", {"start": v(-39.11, -177) * mm, "end": v(-44.89, -177) * mm});
            skLineSegment(sketch, "E31.6.9.10", {"start": v(-44.89, -177) * mm, "end": v(-47.77, -172) * mm});
            skLineSegment(sketch, "E31.6.9.11", {"start": v(-47.77, -172) * mm, "end": v(-44.89, -167) * mm});
            skLineSegment(sketch, "E31.6.9.12", {"start": v(-34.5, -173) * mm, "end": v(-28.72, -173) * mm});
            skLineSegment(sketch, "E31.6.9.13", {"start": v(-28.72, -183) * mm, "end": v(-34.5, -183) * mm});
            skLineSegment(sketch, "E31.6.10.0", {"start": v(-28.72, -185) * mm, "end": v(-25.83, -190) * mm});
            skLineSegment(sketch, "E31.6.10.1", {"start": v(-34.5, -195) * mm, "end": v(-37.38, -190) * mm});
            skLineSegment(sketch, "E31.6.10.2", {"start": v(-37.38, -190) * mm, "end": v(-34.5, -185) * mm});
            skLineSegment(sketch, "E31.6.10.3", {"start": v(-36.23, -184) * mm, "end": v(-39.11, -189) * mm});
            skLineSegment(sketch, "E31.6.10.4", {"start": v(-25.83, -190) * mm, "end": v(-28.72, -195) * mm});
            skPoint(sketch, "E31.6.10.5", {"position": v(-31.6, -185) * mm});
            skLineSegment(sketch, "E31.6.10.6", {"start": v(-39.11, -179) * mm, "end": v(-36.23, -184) * mm});
            skLineSegment(sketch, "E31.6.10.7", {"start": v(-44.89, -179) * mm, "end": v(-39.11, -179) * mm});
            skPoint(sketch, "E31.6.10.8", {"position": v(-42, -179) * mm});
            skLineSegment(sketch, "E31.6.10.9", {"start": v(-39.11, -189) * mm, "end": v(-44.89, -189) * mm});
            skLineSegment(sketch, "E31.6.10.10", {"start": v(-44.89, -189) * mm, "end": v(-47.77, -184) * mm});
            skLineSegment(sketch, "E31.6.10.11", {"start": v(-47.77, -184) * mm, "end": v(-44.89, -179) * mm});
            skLineSegment(sketch, "E31.6.10.12", {"start": v(-34.5, -185) * mm, "end": v(-28.72, -185) * mm});
            skLineSegment(sketch, "E31.6.10.13", {"start": v(-28.72, -195) * mm, "end": v(-34.5, -195) * mm});
            skLineSegment(sketch, "E31.6.11.0", {"start": v(-28.72, -197) * mm, "end": v(-25.83, -202) * mm});
            skLineSegment(sketch, "E31.6.11.1", {"start": v(-34.5, -207) * mm, "end": v(-37.38, -202) * mm});
            skLineSegment(sketch, "E31.6.11.2", {"start": v(-37.38, -202) * mm, "end": v(-34.5, -197) * mm});
            skLineSegment(sketch, "E31.6.11.3", {"start": v(-36.23, -196) * mm, "end": v(-39.11, -201) * mm});
            skLineSegment(sketch, "E31.6.11.4", {"start": v(-25.83, -202) * mm, "end": v(-28.72, -207) * mm});
            skPoint(sketch, "E31.6.11.5", {"position": v(-31.6, -197) * mm});
            skLineSegment(sketch, "E31.6.11.6", {"start": v(-39.11, -191) * mm, "end": v(-36.23, -196) * mm});
            skLineSegment(sketch, "E31.6.11.7", {"start": v(-44.89, -191) * mm, "end": v(-39.11, -191) * mm});
            skPoint(sketch, "E31.6.11.8", {"position": v(-42, -191) * mm});
            skLineSegment(sketch, "E31.6.11.9", {"start": v(-39.11, -201) * mm, "end": v(-44.89, -201) * mm});
            skLineSegment(sketch, "E31.6.11.10", {"start": v(-44.89, -201) * mm, "end": v(-47.77, -196) * mm});
            skLineSegment(sketch, "E31.6.11.11", {"start": v(-47.77, -196) * mm, "end": v(-44.89, -191) * mm});
            skLineSegment(sketch, "E31.6.11.12", {"start": v(-34.5, -197) * mm, "end": v(-28.72, -197) * mm});
            skLineSegment(sketch, "E31.6.11.13", {"start": v(-28.72, -207) * mm, "end": v(-34.5, -207) * mm});
            skLineSegment(sketch, "E31.6.12.0", {"start": v(-28.72, -209) * mm, "end": v(-25.83, -214) * mm});
            skLineSegment(sketch, "E31.6.12.1", {"start": v(-34.5, -219) * mm, "end": v(-37.38, -214) * mm});
            skLineSegment(sketch, "E31.6.12.2", {"start": v(-37.38, -214) * mm, "end": v(-34.5, -209) * mm});
            skLineSegment(sketch, "E31.6.12.3", {"start": v(-36.23, -208) * mm, "end": v(-39.11, -213) * mm});
            skLineSegment(sketch, "E31.6.12.4", {"start": v(-25.83, -214) * mm, "end": v(-28.72, -219) * mm});
            skPoint(sketch, "E31.6.12.5", {"position": v(-31.6, -209) * mm});
            skLineSegment(sketch, "E31.6.12.6", {"start": v(-39.11, -203) * mm, "end": v(-36.23, -208) * mm});
            skLineSegment(sketch, "E31.6.12.7", {"start": v(-44.89, -203) * mm, "end": v(-39.11, -203) * mm});
            skPoint(sketch, "E31.6.12.8", {"position": v(-42, -203) * mm});
            skLineSegment(sketch, "E31.6.12.9", {"start": v(-39.11, -213) * mm, "end": v(-44.89, -213) * mm});
            skLineSegment(sketch, "E31.6.12.10", {"start": v(-44.89, -213) * mm, "end": v(-47.77, -208) * mm});
            skLineSegment(sketch, "E31.6.12.11", {"start": v(-47.77, -208) * mm, "end": v(-44.89, -203) * mm});
            skLineSegment(sketch, "E31.6.12.12", {"start": v(-34.5, -209) * mm, "end": v(-28.72, -209) * mm});
            skLineSegment(sketch, "E31.6.12.13", {"start": v(-28.72, -219) * mm, "end": v(-34.5, -219) * mm});
            skLineSegment(sketch, "E31.6.13.0", {"start": v(-28.72, -221) * mm, "end": v(-25.83, -226) * mm});
            skLineSegment(sketch, "E31.6.13.1", {"start": v(-34.5, -231) * mm, "end": v(-37.38, -226) * mm});
            skLineSegment(sketch, "E31.6.13.2", {"start": v(-37.38, -226) * mm, "end": v(-34.5, -221) * mm});
            skLineSegment(sketch, "E31.6.13.3", {"start": v(-36.23, -220) * mm, "end": v(-39.11, -225) * mm});
            skLineSegment(sketch, "E31.6.13.4", {"start": v(-25.83, -226) * mm, "end": v(-28.72, -231) * mm});
            skPoint(sketch, "E31.6.13.5", {"position": v(-31.6, -221) * mm});
            skLineSegment(sketch, "E31.6.13.6", {"start": v(-39.11, -215) * mm, "end": v(-36.23, -220) * mm});
            skLineSegment(sketch, "E31.6.13.7", {"start": v(-44.89, -215) * mm, "end": v(-39.11, -215) * mm});
            skPoint(sketch, "E31.6.13.8", {"position": v(-42, -215) * mm});
            skLineSegment(sketch, "E31.6.13.9", {"start": v(-39.11, -225) * mm, "end": v(-44.89, -225) * mm});
            skLineSegment(sketch, "E31.6.13.10", {"start": v(-44.89, -225) * mm, "end": v(-47.77, -220) * mm});
            skLineSegment(sketch, "E31.6.13.11", {"start": v(-47.77, -220) * mm, "end": v(-44.89, -215) * mm});
            skLineSegment(sketch, "E31.6.13.12", {"start": v(-34.5, -221) * mm, "end": v(-28.72, -221) * mm});
            skLineSegment(sketch, "E31.6.13.13", {"start": v(-28.72, -231) * mm, "end": v(-34.5, -231) * mm});
            skLineSegment(sketch, "E31.6.14.0", {"start": v(-28.72, -233) * mm, "end": v(-25.83, -238) * mm});
            skLineSegment(sketch, "E31.6.14.1", {"start": v(-34.5, -243) * mm, "end": v(-37.38, -238) * mm});
            skLineSegment(sketch, "E31.6.14.2", {"start": v(-37.38, -238) * mm, "end": v(-34.5, -233) * mm});
            skLineSegment(sketch, "E31.6.14.3", {"start": v(-36.23, -232) * mm, "end": v(-39.11, -237) * mm});
            skLineSegment(sketch, "E31.6.14.4", {"start": v(-25.83, -238) * mm, "end": v(-28.72, -243) * mm});
            skPoint(sketch, "E31.6.14.5", {"position": v(-31.6, -233) * mm});
            skLineSegment(sketch, "E31.6.14.6", {"start": v(-39.11, -227) * mm, "end": v(-36.23, -232) * mm});
            skLineSegment(sketch, "E31.6.14.7", {"start": v(-44.89, -227) * mm, "end": v(-39.11, -227) * mm});
            skPoint(sketch, "E31.6.14.8", {"position": v(-42, -227) * mm});
            skLineSegment(sketch, "E31.6.14.9", {"start": v(-39.11, -237) * mm, "end": v(-44.89, -237) * mm});
            skLineSegment(sketch, "E31.6.14.10", {"start": v(-44.89, -237) * mm, "end": v(-47.77, -232) * mm});
            skLineSegment(sketch, "E31.6.14.11", {"start": v(-47.77, -232) * mm, "end": v(-44.89, -227) * mm});
            skLineSegment(sketch, "E31.6.14.12", {"start": v(-34.5, -233) * mm, "end": v(-28.72, -233) * mm});
            skLineSegment(sketch, "E31.6.14.13", {"start": v(-28.72, -243) * mm, "end": v(-34.5, -243) * mm});
            skLineSegment(sketch, "E31.6.15.0", {"start": v(-28.72, -245) * mm, "end": v(-25.83, -250) * mm});
            skLineSegment(sketch, "E31.6.15.1", {"start": v(-34.5, -255) * mm, "end": v(-37.38, -250) * mm});
            skLineSegment(sketch, "E31.6.15.2", {"start": v(-37.38, -250) * mm, "end": v(-34.5, -245) * mm});
            skLineSegment(sketch, "E31.6.15.3", {"start": v(-36.23, -244) * mm, "end": v(-39.11, -249) * mm});
            skLineSegment(sketch, "E31.6.15.4", {"start": v(-25.83, -250) * mm, "end": v(-28.72, -255) * mm});
            skPoint(sketch, "E31.6.15.5", {"position": v(-31.6, -245) * mm});
            skLineSegment(sketch, "E31.6.15.6", {"start": v(-39.11, -239) * mm, "end": v(-36.23, -244) * mm});
            skLineSegment(sketch, "E31.6.15.7", {"start": v(-44.89, -239) * mm, "end": v(-39.11, -239) * mm});
            skPoint(sketch, "E31.6.15.8", {"position": v(-42, -239) * mm});
            skLineSegment(sketch, "E31.6.15.9", {"start": v(-39.11, -249) * mm, "end": v(-44.89, -249) * mm});
            skLineSegment(sketch, "E31.6.15.10", {"start": v(-44.89, -249) * mm, "end": v(-47.77, -244) * mm});
            skLineSegment(sketch, "E31.6.15.11", {"start": v(-47.77, -244) * mm, "end": v(-44.89, -239) * mm});
            skLineSegment(sketch, "E31.6.15.12", {"start": v(-34.5, -245) * mm, "end": v(-28.72, -245) * mm});
            skLineSegment(sketch, "E31.6.15.13", {"start": v(-28.72, -255) * mm, "end": v(-34.5, -255) * mm});
            skLineSegment(sketch, "E31.6.16.3", {"start": v(-36.23, -256) * mm, "end": v(-39.11, -261) * mm});
            skLineSegment(sketch, "E31.6.16.6", {"start": v(-39.11, -251) * mm, "end": v(-36.23, -256) * mm});
            skLineSegment(sketch, "E31.6.16.7", {"start": v(-44.89, -251) * mm, "end": v(-39.11, -251) * mm});
            skPoint(sketch, "E31.6.16.8", {"position": v(-42, -251) * mm});
            skLineSegment(sketch, "E31.6.16.9", {"start": v(-39.11, -261) * mm, "end": v(-44.89, -261) * mm});
            skLineSegment(sketch, "E31.6.16.10", {"start": v(-44.89, -261) * mm, "end": v(-47.77, -256) * mm});
            skLineSegment(sketch, "E31.6.16.11", {"start": v(-47.77, -256) * mm, "end": v(-44.89, -251) * mm});
            skLineSegment(sketch, "E31.7.0.0", {"start": v(-49.72, -65) * mm, "end": v(-46.83, -70) * mm});
            skLineSegment(sketch, "E31.7.0.1", {"start": v(-55.5, -75) * mm, "end": v(-58.38, -70) * mm});
            skLineSegment(sketch, "E31.7.0.2", {"start": v(-58.38, -70) * mm, "end": v(-55.5, -65) * mm});
            skLineSegment(sketch, "E31.7.0.3", {"start": v(-57.23, -64) * mm, "end": v(-60.11, -69) * mm});
            skLineSegment(sketch, "E31.7.0.4", {"start": v(-46.83, -70) * mm, "end": v(-49.72, -75) * mm});
            skPoint(sketch, "E31.7.0.5", {"position": v(-52.6, -65) * mm});
            skLineSegment(sketch, "E31.7.0.6", {"start": v(-60.11, -59) * mm, "end": v(-57.23, -64) * mm});
            skLineSegment(sketch, "E31.7.0.7", {"start": v(-65.89, -59) * mm, "end": v(-60.11, -59) * mm});
            skPoint(sketch, "E31.7.0.8", {"position": v(-63, -59) * mm});
            skLineSegment(sketch, "E31.7.0.9", {"start": v(-60.11, -69) * mm, "end": v(-65.89, -69) * mm});
            skLineSegment(sketch, "E31.7.0.10", {"start": v(-65.89, -69) * mm, "end": v(-68.77, -64) * mm});
            skLineSegment(sketch, "E31.7.0.11", {"start": v(-68.77, -64) * mm, "end": v(-65.89, -59) * mm});
            skLineSegment(sketch, "E31.7.0.12", {"start": v(-55.5, -65) * mm, "end": v(-49.72, -65) * mm});
            skLineSegment(sketch, "E31.7.0.13", {"start": v(-49.72, -75) * mm, "end": v(-55.5, -75) * mm});
            skLineSegment(sketch, "E31.7.1.0", {"start": v(-49.72, -77) * mm, "end": v(-46.83, -82) * mm});
            skLineSegment(sketch, "E31.7.1.1", {"start": v(-55.5, -87) * mm, "end": v(-58.38, -82) * mm});
            skLineSegment(sketch, "E31.7.1.2", {"start": v(-58.38, -82) * mm, "end": v(-55.5, -77) * mm});
            skLineSegment(sketch, "E31.7.1.3", {"start": v(-57.23, -76) * mm, "end": v(-60.11, -81) * mm});
            skLineSegment(sketch, "E31.7.1.4", {"start": v(-46.83, -82) * mm, "end": v(-49.72, -87) * mm});
            skPoint(sketch, "E31.7.1.5", {"position": v(-52.6, -77) * mm});
            skLineSegment(sketch, "E31.7.1.6", {"start": v(-60.11, -71) * mm, "end": v(-57.23, -76) * mm});
            skLineSegment(sketch, "E31.7.1.7", {"start": v(-65.89, -71) * mm, "end": v(-60.11, -71) * mm});
            skPoint(sketch, "E31.7.1.8", {"position": v(-63, -71) * mm});
            skLineSegment(sketch, "E31.7.1.9", {"start": v(-60.11, -81) * mm, "end": v(-65.89, -81) * mm});
            skLineSegment(sketch, "E31.7.1.10", {"start": v(-65.89, -81) * mm, "end": v(-68.77, -76) * mm});
            skLineSegment(sketch, "E31.7.1.11", {"start": v(-68.77, -76) * mm, "end": v(-65.89, -71) * mm});
            skLineSegment(sketch, "E31.7.1.12", {"start": v(-55.5, -77) * mm, "end": v(-49.72, -77) * mm});
            skLineSegment(sketch, "E31.7.1.13", {"start": v(-49.72, -87) * mm, "end": v(-55.5, -87) * mm});
            skLineSegment(sketch, "E31.7.2.0", {"start": v(-49.72, -89) * mm, "end": v(-46.83, -94) * mm});
            skLineSegment(sketch, "E31.7.2.1", {"start": v(-55.5, -99) * mm, "end": v(-58.38, -94) * mm});
            skLineSegment(sketch, "E31.7.2.2", {"start": v(-58.38, -94) * mm, "end": v(-55.5, -89) * mm});
            skLineSegment(sketch, "E31.7.2.3", {"start": v(-57.23, -88) * mm, "end": v(-60.11, -93) * mm});
            skLineSegment(sketch, "E31.7.2.4", {"start": v(-46.83, -94) * mm, "end": v(-49.72, -99) * mm});
            skPoint(sketch, "E31.7.2.5", {"position": v(-52.6, -89) * mm});
            skLineSegment(sketch, "E31.7.2.6", {"start": v(-60.11, -83) * mm, "end": v(-57.23, -88) * mm});
            skLineSegment(sketch, "E31.7.2.7", {"start": v(-65.89, -83) * mm, "end": v(-60.11, -83) * mm});
            skPoint(sketch, "E31.7.2.8", {"position": v(-63, -83) * mm});
            skLineSegment(sketch, "E31.7.2.9", {"start": v(-60.11, -93) * mm, "end": v(-65.89, -93) * mm});
            skLineSegment(sketch, "E31.7.2.10", {"start": v(-65.89, -93) * mm, "end": v(-68.77, -88) * mm});
            skLineSegment(sketch, "E31.7.2.11", {"start": v(-68.77, -88) * mm, "end": v(-65.89, -83) * mm});
            skLineSegment(sketch, "E31.7.2.12", {"start": v(-55.5, -89) * mm, "end": v(-49.72, -89) * mm});
            skLineSegment(sketch, "E31.7.2.13", {"start": v(-49.72, -99) * mm, "end": v(-55.5, -99) * mm});
            skLineSegment(sketch, "E31.7.3.0", {"start": v(-49.72, -101) * mm, "end": v(-46.83, -106) * mm});
            skLineSegment(sketch, "E31.7.3.1", {"start": v(-55.5, -111) * mm, "end": v(-58.38, -106) * mm});
            skLineSegment(sketch, "E31.7.3.2", {"start": v(-58.38, -106) * mm, "end": v(-55.5, -101) * mm});
            skLineSegment(sketch, "E31.7.3.3", {"start": v(-57.23, -100) * mm, "end": v(-60.11, -105) * mm});
            skLineSegment(sketch, "E31.7.3.4", {"start": v(-46.83, -106) * mm, "end": v(-49.72, -111) * mm});
            skPoint(sketch, "E31.7.3.5", {"position": v(-52.6, -101) * mm});
            skLineSegment(sketch, "E31.7.3.6", {"start": v(-60.11, -95) * mm, "end": v(-57.23, -100) * mm});
            skLineSegment(sketch, "E31.7.3.7", {"start": v(-65.89, -95) * mm, "end": v(-60.11, -95) * mm});
            skPoint(sketch, "E31.7.3.8", {"position": v(-63, -95) * mm});
            skLineSegment(sketch, "E31.7.3.9", {"start": v(-60.11, -105) * mm, "end": v(-65.89, -105) * mm});
            skLineSegment(sketch, "E31.7.3.10", {"start": v(-65.89, -105) * mm, "end": v(-68.77, -100) * mm});
            skLineSegment(sketch, "E31.7.3.11", {"start": v(-68.77, -100) * mm, "end": v(-65.89, -95) * mm});
            skLineSegment(sketch, "E31.7.3.12", {"start": v(-55.5, -101) * mm, "end": v(-49.72, -101) * mm});
            skLineSegment(sketch, "E31.7.3.13", {"start": v(-49.72, -111) * mm, "end": v(-55.5, -111) * mm});
            skLineSegment(sketch, "E31.7.4.0", {"start": v(-49.72, -113) * mm, "end": v(-46.83, -118) * mm});
            skLineSegment(sketch, "E31.7.4.1", {"start": v(-55.5, -123) * mm, "end": v(-58.38, -118) * mm});
            skLineSegment(sketch, "E31.7.4.2", {"start": v(-58.38, -118) * mm, "end": v(-55.5, -113) * mm});
            skLineSegment(sketch, "E31.7.4.3", {"start": v(-57.23, -112) * mm, "end": v(-60.11, -117) * mm});
            skLineSegment(sketch, "E31.7.4.4", {"start": v(-46.83, -118) * mm, "end": v(-49.72, -123) * mm});
            skPoint(sketch, "E31.7.4.5", {"position": v(-52.6, -113) * mm});
            skLineSegment(sketch, "E31.7.4.6", {"start": v(-60.11, -107) * mm, "end": v(-57.23, -112) * mm});
            skLineSegment(sketch, "E31.7.4.7", {"start": v(-65.89, -107) * mm, "end": v(-60.11, -107) * mm});
            skPoint(sketch, "E31.7.4.8", {"position": v(-63, -107) * mm});
            skLineSegment(sketch, "E31.7.4.9", {"start": v(-60.11, -117) * mm, "end": v(-65.89, -117) * mm});
            skLineSegment(sketch, "E31.7.4.10", {"start": v(-65.89, -117) * mm, "end": v(-68.77, -112) * mm});
            skLineSegment(sketch, "E31.7.4.11", {"start": v(-68.77, -112) * mm, "end": v(-65.89, -107) * mm});
            skLineSegment(sketch, "E31.7.4.12", {"start": v(-55.5, -113) * mm, "end": v(-49.72, -113) * mm});
            skLineSegment(sketch, "E31.7.4.13", {"start": v(-49.72, -123) * mm, "end": v(-55.5, -123) * mm});
            skLineSegment(sketch, "E31.7.5.0", {"start": v(-49.72, -125) * mm, "end": v(-46.83, -130) * mm});
            skLineSegment(sketch, "E31.7.5.1", {"start": v(-55.5, -135) * mm, "end": v(-58.38, -130) * mm});
            skLineSegment(sketch, "E31.7.5.2", {"start": v(-58.38, -130) * mm, "end": v(-55.5, -125) * mm});
            skLineSegment(sketch, "E31.7.5.3", {"start": v(-57.23, -124) * mm, "end": v(-60.11, -129) * mm});
            skLineSegment(sketch, "E31.7.5.4", {"start": v(-46.83, -130) * mm, "end": v(-49.72, -135) * mm});
            skPoint(sketch, "E31.7.5.5", {"position": v(-52.6, -125) * mm});
            skLineSegment(sketch, "E31.7.5.6", {"start": v(-60.11, -119) * mm, "end": v(-57.23, -124) * mm});
            skLineSegment(sketch, "E31.7.5.7", {"start": v(-65.89, -119) * mm, "end": v(-60.11, -119) * mm});
            skPoint(sketch, "E31.7.5.8", {"position": v(-63, -119) * mm});
            skLineSegment(sketch, "E31.7.5.9", {"start": v(-60.11, -129) * mm, "end": v(-65.89, -129) * mm});
            skLineSegment(sketch, "E31.7.5.10", {"start": v(-65.89, -129) * mm, "end": v(-68.77, -124) * mm});
            skLineSegment(sketch, "E31.7.5.11", {"start": v(-68.77, -124) * mm, "end": v(-65.89, -119) * mm});
            skLineSegment(sketch, "E31.7.5.12", {"start": v(-55.5, -125) * mm, "end": v(-49.72, -125) * mm});
            skLineSegment(sketch, "E31.7.5.13", {"start": v(-49.72, -135) * mm, "end": v(-55.5, -135) * mm});
            skLineSegment(sketch, "E31.7.6.0", {"start": v(-49.72, -137) * mm, "end": v(-46.83, -142) * mm});
            skLineSegment(sketch, "E31.7.6.1", {"start": v(-55.5, -147) * mm, "end": v(-58.38, -142) * mm});
            skLineSegment(sketch, "E31.7.6.2", {"start": v(-58.38, -142) * mm, "end": v(-55.5, -137) * mm});
            skLineSegment(sketch, "E31.7.6.3", {"start": v(-57.23, -136) * mm, "end": v(-60.11, -141) * mm});
            skLineSegment(sketch, "E31.7.6.4", {"start": v(-46.83, -142) * mm, "end": v(-49.72, -147) * mm});
            skPoint(sketch, "E31.7.6.5", {"position": v(-52.6, -137) * mm});
            skLineSegment(sketch, "E31.7.6.6", {"start": v(-60.11, -131) * mm, "end": v(-57.23, -136) * mm});
            skLineSegment(sketch, "E31.7.6.7", {"start": v(-65.89, -131) * mm, "end": v(-60.11, -131) * mm});
            skPoint(sketch, "E31.7.6.8", {"position": v(-63, -131) * mm});
            skLineSegment(sketch, "E31.7.6.9", {"start": v(-60.11, -141) * mm, "end": v(-65.89, -141) * mm});
            skLineSegment(sketch, "E31.7.6.10", {"start": v(-65.89, -141) * mm, "end": v(-68.77, -136) * mm});
            skLineSegment(sketch, "E31.7.6.11", {"start": v(-68.77, -136) * mm, "end": v(-65.89, -131) * mm});
            skLineSegment(sketch, "E31.7.6.12", {"start": v(-55.5, -137) * mm, "end": v(-49.72, -137) * mm});
            skLineSegment(sketch, "E31.7.6.13", {"start": v(-49.72, -147) * mm, "end": v(-55.5, -147) * mm});
            skLineSegment(sketch, "E31.7.7.0", {"start": v(-49.72, -149) * mm, "end": v(-46.83, -154) * mm});
            skLineSegment(sketch, "E31.7.7.1", {"start": v(-55.5, -159) * mm, "end": v(-58.38, -154) * mm});
            skLineSegment(sketch, "E31.7.7.2", {"start": v(-58.38, -154) * mm, "end": v(-55.5, -149) * mm});
            skLineSegment(sketch, "E31.7.7.3", {"start": v(-57.23, -148) * mm, "end": v(-60.11, -153) * mm});
            skLineSegment(sketch, "E31.7.7.4", {"start": v(-46.83, -154) * mm, "end": v(-49.72, -159) * mm});
            skPoint(sketch, "E31.7.7.5", {"position": v(-52.6, -149) * mm});
            skLineSegment(sketch, "E31.7.7.6", {"start": v(-60.11, -143) * mm, "end": v(-57.23, -148) * mm});
            skLineSegment(sketch, "E31.7.7.7", {"start": v(-65.89, -143) * mm, "end": v(-60.11, -143) * mm});
            skPoint(sketch, "E31.7.7.8", {"position": v(-63, -143) * mm});
            skLineSegment(sketch, "E31.7.7.9", {"start": v(-60.11, -153) * mm, "end": v(-65.89, -153) * mm});
            skLineSegment(sketch, "E31.7.7.10", {"start": v(-65.89, -153) * mm, "end": v(-68.77, -148) * mm});
            skLineSegment(sketch, "E31.7.7.11", {"start": v(-68.77, -148) * mm, "end": v(-65.89, -143) * mm});
            skLineSegment(sketch, "E31.7.7.12", {"start": v(-55.5, -149) * mm, "end": v(-49.72, -149) * mm});
            skLineSegment(sketch, "E31.7.7.13", {"start": v(-49.72, -159) * mm, "end": v(-55.5, -159) * mm});
            skLineSegment(sketch, "E31.7.8.0", {"start": v(-49.72, -161) * mm, "end": v(-46.83, -166) * mm});
            skLineSegment(sketch, "E31.7.8.1", {"start": v(-55.5, -171) * mm, "end": v(-58.38, -166) * mm});
            skLineSegment(sketch, "E31.7.8.2", {"start": v(-58.38, -166) * mm, "end": v(-55.5, -161) * mm});
            skLineSegment(sketch, "E31.7.8.3", {"start": v(-57.23, -160) * mm, "end": v(-60.11, -165) * mm});
            skLineSegment(sketch, "E31.7.8.4", {"start": v(-46.83, -166) * mm, "end": v(-49.72, -171) * mm});
            skPoint(sketch, "E31.7.8.5", {"position": v(-52.6, -161) * mm});
            skLineSegment(sketch, "E31.7.8.6", {"start": v(-60.11, -155) * mm, "end": v(-57.23, -160) * mm});
            skLineSegment(sketch, "E31.7.8.7", {"start": v(-65.89, -155) * mm, "end": v(-60.11, -155) * mm});
            skPoint(sketch, "E31.7.8.8", {"position": v(-63, -155) * mm});
            skLineSegment(sketch, "E31.7.8.9", {"start": v(-60.11, -165) * mm, "end": v(-65.89, -165) * mm});
            skLineSegment(sketch, "E31.7.8.10", {"start": v(-65.89, -165) * mm, "end": v(-68.77, -160) * mm});
            skLineSegment(sketch, "E31.7.8.11", {"start": v(-68.77, -160) * mm, "end": v(-65.89, -155) * mm});
            skLineSegment(sketch, "E31.7.8.12", {"start": v(-55.5, -161) * mm, "end": v(-49.72, -161) * mm});
            skLineSegment(sketch, "E31.7.8.13", {"start": v(-49.72, -171) * mm, "end": v(-55.5, -171) * mm});
            skLineSegment(sketch, "E31.7.9.0", {"start": v(-49.72, -173) * mm, "end": v(-46.83, -178) * mm});
            skLineSegment(sketch, "E31.7.9.1", {"start": v(-55.5, -183) * mm, "end": v(-58.38, -178) * mm});
            skLineSegment(sketch, "E31.7.9.2", {"start": v(-58.38, -178) * mm, "end": v(-55.5, -173) * mm});
            skLineSegment(sketch, "E31.7.9.3", {"start": v(-57.23, -172) * mm, "end": v(-60.11, -177) * mm});
            skLineSegment(sketch, "E31.7.9.4", {"start": v(-46.83, -178) * mm, "end": v(-49.72, -183) * mm});
            skPoint(sketch, "E31.7.9.5", {"position": v(-52.6, -173) * mm});
            skLineSegment(sketch, "E31.7.9.6", {"start": v(-60.11, -167) * mm, "end": v(-57.23, -172) * mm});
            skLineSegment(sketch, "E31.7.9.7", {"start": v(-65.89, -167) * mm, "end": v(-60.11, -167) * mm});
            skPoint(sketch, "E31.7.9.8", {"position": v(-63, -167) * mm});
            skLineSegment(sketch, "E31.7.9.9", {"start": v(-60.11, -177) * mm, "end": v(-65.89, -177) * mm});
            skLineSegment(sketch, "E31.7.9.10", {"start": v(-65.89, -177) * mm, "end": v(-68.77, -172) * mm});
            skLineSegment(sketch, "E31.7.9.11", {"start": v(-68.77, -172) * mm, "end": v(-65.89, -167) * mm});
            skLineSegment(sketch, "E31.7.9.12", {"start": v(-55.5, -173) * mm, "end": v(-49.72, -173) * mm});
            skLineSegment(sketch, "E31.7.9.13", {"start": v(-49.72, -183) * mm, "end": v(-55.5, -183) * mm});
            skLineSegment(sketch, "E31.7.10.0", {"start": v(-49.72, -185) * mm, "end": v(-46.83, -190) * mm});
            skLineSegment(sketch, "E31.7.10.1", {"start": v(-55.5, -195) * mm, "end": v(-58.38, -190) * mm});
            skLineSegment(sketch, "E31.7.10.2", {"start": v(-58.38, -190) * mm, "end": v(-55.5, -185) * mm});
            skLineSegment(sketch, "E31.7.10.3", {"start": v(-57.23, -184) * mm, "end": v(-60.11, -189) * mm});
            skLineSegment(sketch, "E31.7.10.4", {"start": v(-46.83, -190) * mm, "end": v(-49.72, -195) * mm});
            skPoint(sketch, "E31.7.10.5", {"position": v(-52.6, -185) * mm});
            skLineSegment(sketch, "E31.7.10.6", {"start": v(-60.11, -179) * mm, "end": v(-57.23, -184) * mm});
            skLineSegment(sketch, "E31.7.10.7", {"start": v(-65.89, -179) * mm, "end": v(-60.11, -179) * mm});
            skPoint(sketch, "E31.7.10.8", {"position": v(-63, -179) * mm});
            skLineSegment(sketch, "E31.7.10.9", {"start": v(-60.11, -189) * mm, "end": v(-65.89, -189) * mm});
            skLineSegment(sketch, "E31.7.10.10", {"start": v(-65.89, -189) * mm, "end": v(-68.77, -184) * mm});
            skLineSegment(sketch, "E31.7.10.11", {"start": v(-68.77, -184) * mm, "end": v(-65.89, -179) * mm});
            skLineSegment(sketch, "E31.7.10.12", {"start": v(-55.5, -185) * mm, "end": v(-49.72, -185) * mm});
            skLineSegment(sketch, "E31.7.10.13", {"start": v(-49.72, -195) * mm, "end": v(-55.5, -195) * mm});
            skLineSegment(sketch, "E31.7.11.0", {"start": v(-49.72, -197) * mm, "end": v(-46.83, -202) * mm});
            skLineSegment(sketch, "E31.7.11.1", {"start": v(-55.5, -207) * mm, "end": v(-58.38, -202) * mm});
            skLineSegment(sketch, "E31.7.11.2", {"start": v(-58.38, -202) * mm, "end": v(-55.5, -197) * mm});
            skLineSegment(sketch, "E31.7.11.3", {"start": v(-57.23, -196) * mm, "end": v(-60.11, -201) * mm});
            skLineSegment(sketch, "E31.7.11.4", {"start": v(-46.83, -202) * mm, "end": v(-49.72, -207) * mm});
            skPoint(sketch, "E31.7.11.5", {"position": v(-52.6, -197) * mm});
            skLineSegment(sketch, "E31.7.11.6", {"start": v(-60.11, -191) * mm, "end": v(-57.23, -196) * mm});
            skLineSegment(sketch, "E31.7.11.7", {"start": v(-65.89, -191) * mm, "end": v(-60.11, -191) * mm});
            skPoint(sketch, "E31.7.11.8", {"position": v(-63, -191) * mm});
            skLineSegment(sketch, "E31.7.11.9", {"start": v(-60.11, -201) * mm, "end": v(-65.89, -201) * mm});
            skLineSegment(sketch, "E31.7.11.10", {"start": v(-65.89, -201) * mm, "end": v(-68.77, -196) * mm});
            skLineSegment(sketch, "E31.7.11.11", {"start": v(-68.77, -196) * mm, "end": v(-65.89, -191) * mm});
            skLineSegment(sketch, "E31.7.11.12", {"start": v(-55.5, -197) * mm, "end": v(-49.72, -197) * mm});
            skLineSegment(sketch, "E31.7.11.13", {"start": v(-49.72, -207) * mm, "end": v(-55.5, -207) * mm});
            skLineSegment(sketch, "E31.7.12.0", {"start": v(-49.72, -209) * mm, "end": v(-46.83, -214) * mm});
            skLineSegment(sketch, "E31.7.12.1", {"start": v(-55.5, -219) * mm, "end": v(-58.38, -214) * mm});
            skLineSegment(sketch, "E31.7.12.2", {"start": v(-58.38, -214) * mm, "end": v(-55.5, -209) * mm});
            skLineSegment(sketch, "E31.7.12.3", {"start": v(-57.23, -208) * mm, "end": v(-60.11, -213) * mm});
            skLineSegment(sketch, "E31.7.12.4", {"start": v(-46.83, -214) * mm, "end": v(-49.72, -219) * mm});
            skPoint(sketch, "E31.7.12.5", {"position": v(-52.6, -209) * mm});
            skLineSegment(sketch, "E31.7.12.6", {"start": v(-60.11, -203) * mm, "end": v(-57.23, -208) * mm});
            skLineSegment(sketch, "E31.7.12.7", {"start": v(-65.89, -203) * mm, "end": v(-60.11, -203) * mm});
            skPoint(sketch, "E31.7.12.8", {"position": v(-63, -203) * mm});
            skLineSegment(sketch, "E31.7.12.9", {"start": v(-60.11, -213) * mm, "end": v(-65.89, -213) * mm});
            skLineSegment(sketch, "E31.7.12.10", {"start": v(-65.89, -213) * mm, "end": v(-68.77, -208) * mm});
            skLineSegment(sketch, "E31.7.12.11", {"start": v(-68.77, -208) * mm, "end": v(-65.89, -203) * mm});
            skLineSegment(sketch, "E31.7.12.12", {"start": v(-55.5, -209) * mm, "end": v(-49.72, -209) * mm});
            skLineSegment(sketch, "E31.7.12.13", {"start": v(-49.72, -219) * mm, "end": v(-55.5, -219) * mm});
            skLineSegment(sketch, "E31.7.13.0", {"start": v(-49.72, -221) * mm, "end": v(-46.83, -226) * mm});
            skLineSegment(sketch, "E31.7.13.1", {"start": v(-55.5, -231) * mm, "end": v(-58.38, -226) * mm});
            skLineSegment(sketch, "E31.7.13.2", {"start": v(-58.38, -226) * mm, "end": v(-55.5, -221) * mm});
            skLineSegment(sketch, "E31.7.13.3", {"start": v(-57.23, -220) * mm, "end": v(-60.11, -225) * mm});
            skLineSegment(sketch, "E31.7.13.4", {"start": v(-46.83, -226) * mm, "end": v(-49.72, -231) * mm});
            skPoint(sketch, "E31.7.13.5", {"position": v(-52.6, -221) * mm});
            skLineSegment(sketch, "E31.7.13.6", {"start": v(-60.11, -215) * mm, "end": v(-57.23, -220) * mm});
            skLineSegment(sketch, "E31.7.13.7", {"start": v(-65.89, -215) * mm, "end": v(-60.11, -215) * mm});
            skPoint(sketch, "E31.7.13.8", {"position": v(-63, -215) * mm});
            skLineSegment(sketch, "E31.7.13.9", {"start": v(-60.11, -225) * mm, "end": v(-65.89, -225) * mm});
            skLineSegment(sketch, "E31.7.13.10", {"start": v(-65.89, -225) * mm, "end": v(-68.77, -220) * mm});
            skLineSegment(sketch, "E31.7.13.11", {"start": v(-68.77, -220) * mm, "end": v(-65.89, -215) * mm});
            skLineSegment(sketch, "E31.7.13.12", {"start": v(-55.5, -221) * mm, "end": v(-49.72, -221) * mm});
            skLineSegment(sketch, "E31.7.13.13", {"start": v(-49.72, -231) * mm, "end": v(-55.5, -231) * mm});
            skLineSegment(sketch, "E31.7.14.0", {"start": v(-49.72, -233) * mm, "end": v(-46.83, -238) * mm});
            skLineSegment(sketch, "E31.7.14.1", {"start": v(-55.5, -243) * mm, "end": v(-58.38, -238) * mm});
            skLineSegment(sketch, "E31.7.14.2", {"start": v(-58.38, -238) * mm, "end": v(-55.5, -233) * mm});
            skLineSegment(sketch, "E31.7.14.3", {"start": v(-57.23, -232) * mm, "end": v(-60.11, -237) * mm});
            skLineSegment(sketch, "E31.7.14.4", {"start": v(-46.83, -238) * mm, "end": v(-49.72, -243) * mm});
            skPoint(sketch, "E31.7.14.5", {"position": v(-52.6, -233) * mm});
            skLineSegment(sketch, "E31.7.14.6", {"start": v(-60.11, -227) * mm, "end": v(-57.23, -232) * mm});
            skLineSegment(sketch, "E31.7.14.7", {"start": v(-65.89, -227) * mm, "end": v(-60.11, -227) * mm});
            skPoint(sketch, "E31.7.14.8", {"position": v(-63, -227) * mm});
            skLineSegment(sketch, "E31.7.14.9", {"start": v(-60.11, -237) * mm, "end": v(-65.89, -237) * mm});
            skLineSegment(sketch, "E31.7.14.10", {"start": v(-65.89, -237) * mm, "end": v(-68.77, -232) * mm});
            skLineSegment(sketch, "E31.7.14.11", {"start": v(-68.77, -232) * mm, "end": v(-65.89, -227) * mm});
            skLineSegment(sketch, "E31.7.14.12", {"start": v(-55.5, -233) * mm, "end": v(-49.72, -233) * mm});
            skLineSegment(sketch, "E31.7.14.13", {"start": v(-49.72, -243) * mm, "end": v(-55.5, -243) * mm});
            skLineSegment(sketch, "E31.7.15.0", {"start": v(-49.72, -245) * mm, "end": v(-46.83, -250) * mm});
            skLineSegment(sketch, "E31.7.15.1", {"start": v(-55.5, -255) * mm, "end": v(-58.38, -250) * mm});
            skLineSegment(sketch, "E31.7.15.2", {"start": v(-58.38, -250) * mm, "end": v(-55.5, -245) * mm});
            skLineSegment(sketch, "E31.7.15.3", {"start": v(-57.23, -244) * mm, "end": v(-60.11, -249) * mm});
            skLineSegment(sketch, "E31.7.15.4", {"start": v(-46.83, -250) * mm, "end": v(-49.72, -255) * mm});
            skPoint(sketch, "E31.7.15.5", {"position": v(-52.6, -245) * mm});
            skLineSegment(sketch, "E31.7.15.6", {"start": v(-60.11, -239) * mm, "end": v(-57.23, -244) * mm});
            skLineSegment(sketch, "E31.7.15.7", {"start": v(-65.89, -239) * mm, "end": v(-60.11, -239) * mm});
            skPoint(sketch, "E31.7.15.8", {"position": v(-63, -239) * mm});
            skLineSegment(sketch, "E31.7.15.9", {"start": v(-60.11, -249) * mm, "end": v(-65.89, -249) * mm});
            skLineSegment(sketch, "E31.7.15.10", {"start": v(-65.89, -249) * mm, "end": v(-68.77, -244) * mm});
            skLineSegment(sketch, "E31.7.15.11", {"start": v(-68.77, -244) * mm, "end": v(-65.89, -239) * mm});
            skLineSegment(sketch, "E31.7.15.12", {"start": v(-55.5, -245) * mm, "end": v(-49.72, -245) * mm});
            skLineSegment(sketch, "E31.7.15.13", {"start": v(-49.72, -255) * mm, "end": v(-55.5, -255) * mm});
            skLineSegment(sketch, "E31.7.16.3", {"start": v(-57.23, -256) * mm, "end": v(-60.11, -261) * mm});
            skLineSegment(sketch, "E31.7.16.6", {"start": v(-60.11, -251) * mm, "end": v(-57.23, -256) * mm});
            skLineSegment(sketch, "E31.7.16.7", {"start": v(-65.89, -251) * mm, "end": v(-60.11, -251) * mm});
            skPoint(sketch, "E31.7.16.8", {"position": v(-63, -251) * mm});
            skLineSegment(sketch, "E31.7.16.9", {"start": v(-60.11, -261) * mm, "end": v(-65.89, -261) * mm});
            skLineSegment(sketch, "E31.7.16.10", {"start": v(-65.89, -261) * mm, "end": v(-68.77, -256) * mm});
            skLineSegment(sketch, "E31.7.16.11", {"start": v(-68.77, -256) * mm, "end": v(-65.89, -251) * mm});
            skLineSegment(sketch, "E31.8.0.0", {"start": v(-70.72, -65) * mm, "end": v(-67.83, -70) * mm});
            skLineSegment(sketch, "E31.8.0.1", {"start": v(-76.5, -75) * mm, "end": v(-79.38, -70) * mm});
            skLineSegment(sketch, "E31.8.0.2", {"start": v(-79.38, -70) * mm, "end": v(-76.5, -65) * mm});
            skLineSegment(sketch, "E31.8.0.3", {"start": v(-78.23, -64) * mm, "end": v(-81.11, -69) * mm});
            skLineSegment(sketch, "E31.8.0.4", {"start": v(-67.83, -70) * mm, "end": v(-70.72, -75) * mm});
            skPoint(sketch, "E31.8.0.5", {"position": v(-73.6, -65) * mm});
            skLineSegment(sketch, "E31.8.0.6", {"start": v(-81.11, -59) * mm, "end": v(-78.23, -64) * mm});
            skLineSegment(sketch, "E31.8.0.7", {"start": v(-86.89, -59) * mm, "end": v(-81.11, -59) * mm});
            skPoint(sketch, "E31.8.0.8", {"position": v(-84, -59) * mm});
            skLineSegment(sketch, "E31.8.0.9", {"start": v(-81.11, -69) * mm, "end": v(-86.89, -69) * mm});
            skLineSegment(sketch, "E31.8.0.10", {"start": v(-86.89, -69) * mm, "end": v(-89.77, -64) * mm});
            skLineSegment(sketch, "E31.8.0.11", {"start": v(-89.77, -64) * mm, "end": v(-86.89, -59) * mm});
            skLineSegment(sketch, "E31.8.0.12", {"start": v(-76.5, -65) * mm, "end": v(-70.72, -65) * mm});
            skLineSegment(sketch, "E31.8.0.13", {"start": v(-70.72, -75) * mm, "end": v(-76.5, -75) * mm});
            skLineSegment(sketch, "E31.8.1.0", {"start": v(-70.72, -77) * mm, "end": v(-67.83, -82) * mm});
            skLineSegment(sketch, "E31.8.1.1", {"start": v(-76.5, -87) * mm, "end": v(-79.38, -82) * mm});
            skLineSegment(sketch, "E31.8.1.2", {"start": v(-79.38, -82) * mm, "end": v(-76.5, -77) * mm});
            skLineSegment(sketch, "E31.8.1.3", {"start": v(-78.23, -76) * mm, "end": v(-81.11, -81) * mm});
            skLineSegment(sketch, "E31.8.1.4", {"start": v(-67.83, -82) * mm, "end": v(-70.72, -87) * mm});
            skPoint(sketch, "E31.8.1.5", {"position": v(-73.6, -77) * mm});
            skLineSegment(sketch, "E31.8.1.6", {"start": v(-81.11, -71) * mm, "end": v(-78.23, -76) * mm});
            skLineSegment(sketch, "E31.8.1.7", {"start": v(-86.89, -71) * mm, "end": v(-81.11, -71) * mm});
            skPoint(sketch, "E31.8.1.8", {"position": v(-84, -71) * mm});
            skLineSegment(sketch, "E31.8.1.9", {"start": v(-81.11, -81) * mm, "end": v(-86.89, -81) * mm});
            skLineSegment(sketch, "E31.8.1.10", {"start": v(-86.89, -81) * mm, "end": v(-89.77, -76) * mm});
            skLineSegment(sketch, "E31.8.1.11", {"start": v(-89.77, -76) * mm, "end": v(-86.89, -71) * mm});
            skLineSegment(sketch, "E31.8.1.12", {"start": v(-76.5, -77) * mm, "end": v(-70.72, -77) * mm});
            skLineSegment(sketch, "E31.8.1.13", {"start": v(-70.72, -87) * mm, "end": v(-76.5, -87) * mm});
            skLineSegment(sketch, "E31.8.2.0", {"start": v(-70.72, -89) * mm, "end": v(-67.83, -94) * mm});
            skLineSegment(sketch, "E31.8.2.1", {"start": v(-76.5, -99) * mm, "end": v(-79.38, -94) * mm});
            skLineSegment(sketch, "E31.8.2.2", {"start": v(-79.38, -94) * mm, "end": v(-76.5, -89) * mm});
            skLineSegment(sketch, "E31.8.2.3", {"start": v(-78.23, -88) * mm, "end": v(-81.11, -93) * mm});
            skLineSegment(sketch, "E31.8.2.4", {"start": v(-67.83, -94) * mm, "end": v(-70.72, -99) * mm});
            skPoint(sketch, "E31.8.2.5", {"position": v(-73.6, -89) * mm});
            skLineSegment(sketch, "E31.8.2.6", {"start": v(-81.11, -83) * mm, "end": v(-78.23, -88) * mm});
            skLineSegment(sketch, "E31.8.2.7", {"start": v(-86.89, -83) * mm, "end": v(-81.11, -83) * mm});
            skPoint(sketch, "E31.8.2.8", {"position": v(-84, -83) * mm});
            skLineSegment(sketch, "E31.8.2.9", {"start": v(-81.11, -93) * mm, "end": v(-86.89, -93) * mm});
            skLineSegment(sketch, "E31.8.2.10", {"start": v(-86.89, -93) * mm, "end": v(-89.77, -88) * mm});
            skLineSegment(sketch, "E31.8.2.11", {"start": v(-89.77, -88) * mm, "end": v(-86.89, -83) * mm});
            skLineSegment(sketch, "E31.8.2.12", {"start": v(-76.5, -89) * mm, "end": v(-70.72, -89) * mm});
            skLineSegment(sketch, "E31.8.2.13", {"start": v(-70.72, -99) * mm, "end": v(-76.5, -99) * mm});
            skLineSegment(sketch, "E31.8.3.0", {"start": v(-70.72, -101) * mm, "end": v(-67.83, -106) * mm});
            skLineSegment(sketch, "E31.8.3.1", {"start": v(-76.5, -111) * mm, "end": v(-79.38, -106) * mm});
            skLineSegment(sketch, "E31.8.3.2", {"start": v(-79.38, -106) * mm, "end": v(-76.5, -101) * mm});
            skLineSegment(sketch, "E31.8.3.3", {"start": v(-78.23, -100) * mm, "end": v(-81.11, -105) * mm});
            skLineSegment(sketch, "E31.8.3.4", {"start": v(-67.83, -106) * mm, "end": v(-70.72, -111) * mm});
            skPoint(sketch, "E31.8.3.5", {"position": v(-73.6, -101) * mm});
            skLineSegment(sketch, "E31.8.3.6", {"start": v(-81.11, -95) * mm, "end": v(-78.23, -100) * mm});
            skLineSegment(sketch, "E31.8.3.7", {"start": v(-86.89, -95) * mm, "end": v(-81.11, -95) * mm});
            skPoint(sketch, "E31.8.3.8", {"position": v(-84, -95) * mm});
            skLineSegment(sketch, "E31.8.3.9", {"start": v(-81.11, -105) * mm, "end": v(-86.89, -105) * mm});
            skLineSegment(sketch, "E31.8.3.10", {"start": v(-86.89, -105) * mm, "end": v(-89.77, -100) * mm});
            skLineSegment(sketch, "E31.8.3.11", {"start": v(-89.77, -100) * mm, "end": v(-86.89, -95) * mm});
            skLineSegment(sketch, "E31.8.3.12", {"start": v(-76.5, -101) * mm, "end": v(-70.72, -101) * mm});
            skLineSegment(sketch, "E31.8.3.13", {"start": v(-70.72, -111) * mm, "end": v(-76.5, -111) * mm});
            skLineSegment(sketch, "E31.8.4.0", {"start": v(-70.72, -113) * mm, "end": v(-67.83, -118) * mm});
            skLineSegment(sketch, "E31.8.4.1", {"start": v(-76.5, -123) * mm, "end": v(-79.38, -118) * mm});
            skLineSegment(sketch, "E31.8.4.2", {"start": v(-79.38, -118) * mm, "end": v(-76.5, -113) * mm});
            skLineSegment(sketch, "E31.8.4.3", {"start": v(-78.23, -112) * mm, "end": v(-81.11, -117) * mm});
            skLineSegment(sketch, "E31.8.4.4", {"start": v(-67.83, -118) * mm, "end": v(-70.72, -123) * mm});
            skPoint(sketch, "E31.8.4.5", {"position": v(-73.6, -113) * mm});
            skLineSegment(sketch, "E31.8.4.6", {"start": v(-81.11, -107) * mm, "end": v(-78.23, -112) * mm});
            skLineSegment(sketch, "E31.8.4.7", {"start": v(-86.89, -107) * mm, "end": v(-81.11, -107) * mm});
            skPoint(sketch, "E31.8.4.8", {"position": v(-84, -107) * mm});
            skLineSegment(sketch, "E31.8.4.9", {"start": v(-81.11, -117) * mm, "end": v(-86.89, -117) * mm});
            skLineSegment(sketch, "E31.8.4.10", {"start": v(-86.89, -117) * mm, "end": v(-89.77, -112) * mm});
            skLineSegment(sketch, "E31.8.4.11", {"start": v(-89.77, -112) * mm, "end": v(-86.89, -107) * mm});
            skLineSegment(sketch, "E31.8.4.12", {"start": v(-76.5, -113) * mm, "end": v(-70.72, -113) * mm});
            skLineSegment(sketch, "E31.8.4.13", {"start": v(-70.72, -123) * mm, "end": v(-76.5, -123) * mm});
            skLineSegment(sketch, "E31.8.5.0", {"start": v(-70.72, -125) * mm, "end": v(-67.83, -130) * mm});
            skLineSegment(sketch, "E31.8.5.1", {"start": v(-76.5, -135) * mm, "end": v(-79.38, -130) * mm});
            skLineSegment(sketch, "E31.8.5.2", {"start": v(-79.38, -130) * mm, "end": v(-76.5, -125) * mm});
            skLineSegment(sketch, "E31.8.5.3", {"start": v(-78.23, -124) * mm, "end": v(-81.11, -129) * mm});
            skLineSegment(sketch, "E31.8.5.4", {"start": v(-67.83, -130) * mm, "end": v(-70.72, -135) * mm});
            skPoint(sketch, "E31.8.5.5", {"position": v(-73.6, -125) * mm});
            skLineSegment(sketch, "E31.8.5.6", {"start": v(-81.11, -119) * mm, "end": v(-78.23, -124) * mm});
            skLineSegment(sketch, "E31.8.5.7", {"start": v(-86.89, -119) * mm, "end": v(-81.11, -119) * mm});
            skPoint(sketch, "E31.8.5.8", {"position": v(-84, -119) * mm});
            skLineSegment(sketch, "E31.8.5.9", {"start": v(-81.11, -129) * mm, "end": v(-86.89, -129) * mm});
            skLineSegment(sketch, "E31.8.5.10", {"start": v(-86.89, -129) * mm, "end": v(-89.77, -124) * mm});
            skLineSegment(sketch, "E31.8.5.11", {"start": v(-89.77, -124) * mm, "end": v(-86.89, -119) * mm});
            skLineSegment(sketch, "E31.8.5.12", {"start": v(-76.5, -125) * mm, "end": v(-70.72, -125) * mm});
            skLineSegment(sketch, "E31.8.5.13", {"start": v(-70.72, -135) * mm, "end": v(-76.5, -135) * mm});
            skLineSegment(sketch, "E31.8.6.0", {"start": v(-70.72, -137) * mm, "end": v(-67.83, -142) * mm});
            skLineSegment(sketch, "E31.8.6.1", {"start": v(-76.5, -147) * mm, "end": v(-79.38, -142) * mm});
            skLineSegment(sketch, "E31.8.6.2", {"start": v(-79.38, -142) * mm, "end": v(-76.5, -137) * mm});
            skLineSegment(sketch, "E31.8.6.3", {"start": v(-78.23, -136) * mm, "end": v(-81.11, -141) * mm});
            skLineSegment(sketch, "E31.8.6.4", {"start": v(-67.83, -142) * mm, "end": v(-70.72, -147) * mm});
            skPoint(sketch, "E31.8.6.5", {"position": v(-73.6, -137) * mm});
            skLineSegment(sketch, "E31.8.6.6", {"start": v(-81.11, -131) * mm, "end": v(-78.23, -136) * mm});
            skLineSegment(sketch, "E31.8.6.7", {"start": v(-86.89, -131) * mm, "end": v(-81.11, -131) * mm});
            skPoint(sketch, "E31.8.6.8", {"position": v(-84, -131) * mm});
            skLineSegment(sketch, "E31.8.6.9", {"start": v(-81.11, -141) * mm, "end": v(-86.89, -141) * mm});
            skLineSegment(sketch, "E31.8.6.10", {"start": v(-86.89, -141) * mm, "end": v(-89.77, -136) * mm});
            skLineSegment(sketch, "E31.8.6.11", {"start": v(-89.77, -136) * mm, "end": v(-86.89, -131) * mm});
            skLineSegment(sketch, "E31.8.6.12", {"start": v(-76.5, -137) * mm, "end": v(-70.72, -137) * mm});
            skLineSegment(sketch, "E31.8.6.13", {"start": v(-70.72, -147) * mm, "end": v(-76.5, -147) * mm});
            skLineSegment(sketch, "E31.8.7.0", {"start": v(-70.72, -149) * mm, "end": v(-67.83, -154) * mm});
            skLineSegment(sketch, "E31.8.7.1", {"start": v(-76.5, -159) * mm, "end": v(-79.38, -154) * mm});
            skLineSegment(sketch, "E31.8.7.2", {"start": v(-79.38, -154) * mm, "end": v(-76.5, -149) * mm});
            skLineSegment(sketch, "E31.8.7.3", {"start": v(-78.23, -148) * mm, "end": v(-81.11, -153) * mm});
            skLineSegment(sketch, "E31.8.7.4", {"start": v(-67.83, -154) * mm, "end": v(-70.72, -159) * mm});
            skPoint(sketch, "E31.8.7.5", {"position": v(-73.6, -149) * mm});
            skLineSegment(sketch, "E31.8.7.6", {"start": v(-81.11, -143) * mm, "end": v(-78.23, -148) * mm});
            skLineSegment(sketch, "E31.8.7.7", {"start": v(-86.89, -143) * mm, "end": v(-81.11, -143) * mm});
            skPoint(sketch, "E31.8.7.8", {"position": v(-84, -143) * mm});
            skLineSegment(sketch, "E31.8.7.9", {"start": v(-81.11, -153) * mm, "end": v(-86.89, -153) * mm});
            skLineSegment(sketch, "E31.8.7.10", {"start": v(-86.89, -153) * mm, "end": v(-89.77, -148) * mm});
            skLineSegment(sketch, "E31.8.7.11", {"start": v(-89.77, -148) * mm, "end": v(-86.89, -143) * mm});
            skLineSegment(sketch, "E31.8.7.12", {"start": v(-76.5, -149) * mm, "end": v(-70.72, -149) * mm});
            skLineSegment(sketch, "E31.8.7.13", {"start": v(-70.72, -159) * mm, "end": v(-76.5, -159) * mm});
            skLineSegment(sketch, "E31.8.8.0", {"start": v(-70.72, -161) * mm, "end": v(-67.83, -166) * mm});
            skLineSegment(sketch, "E31.8.8.1", {"start": v(-76.5, -171) * mm, "end": v(-79.38, -166) * mm});
            skLineSegment(sketch, "E31.8.8.2", {"start": v(-79.38, -166) * mm, "end": v(-76.5, -161) * mm});
            skLineSegment(sketch, "E31.8.8.3", {"start": v(-78.23, -160) * mm, "end": v(-81.11, -165) * mm});
            skLineSegment(sketch, "E31.8.8.4", {"start": v(-67.83, -166) * mm, "end": v(-70.72, -171) * mm});
            skPoint(sketch, "E31.8.8.5", {"position": v(-73.6, -161) * mm});
            skLineSegment(sketch, "E31.8.8.6", {"start": v(-81.11, -155) * mm, "end": v(-78.23, -160) * mm});
            skLineSegment(sketch, "E31.8.8.7", {"start": v(-86.89, -155) * mm, "end": v(-81.11, -155) * mm});
            skPoint(sketch, "E31.8.8.8", {"position": v(-84, -155) * mm});
            skLineSegment(sketch, "E31.8.8.9", {"start": v(-81.11, -165) * mm, "end": v(-86.89, -165) * mm});
            skLineSegment(sketch, "E31.8.8.10", {"start": v(-86.89, -165) * mm, "end": v(-89.77, -160) * mm});
            skLineSegment(sketch, "E31.8.8.11", {"start": v(-89.77, -160) * mm, "end": v(-86.89, -155) * mm});
            skLineSegment(sketch, "E31.8.8.12", {"start": v(-76.5, -161) * mm, "end": v(-70.72, -161) * mm});
            skLineSegment(sketch, "E31.8.8.13", {"start": v(-70.72, -171) * mm, "end": v(-76.5, -171) * mm});
            skLineSegment(sketch, "E31.8.9.0", {"start": v(-70.72, -173) * mm, "end": v(-67.83, -178) * mm});
            skLineSegment(sketch, "E31.8.9.1", {"start": v(-76.5, -183) * mm, "end": v(-79.38, -178) * mm});
            skLineSegment(sketch, "E31.8.9.2", {"start": v(-79.38, -178) * mm, "end": v(-76.5, -173) * mm});
            skLineSegment(sketch, "E31.8.9.3", {"start": v(-78.23, -172) * mm, "end": v(-81.11, -177) * mm});
            skLineSegment(sketch, "E31.8.9.4", {"start": v(-67.83, -178) * mm, "end": v(-70.72, -183) * mm});
            skPoint(sketch, "E31.8.9.5", {"position": v(-73.6, -173) * mm});
            skLineSegment(sketch, "E31.8.9.6", {"start": v(-81.11, -167) * mm, "end": v(-78.23, -172) * mm});
            skLineSegment(sketch, "E31.8.9.7", {"start": v(-86.89, -167) * mm, "end": v(-81.11, -167) * mm});
            skPoint(sketch, "E31.8.9.8", {"position": v(-84, -167) * mm});
            skLineSegment(sketch, "E31.8.9.9", {"start": v(-81.11, -177) * mm, "end": v(-86.89, -177) * mm});
            skLineSegment(sketch, "E31.8.9.10", {"start": v(-86.89, -177) * mm, "end": v(-89.77, -172) * mm});
            skLineSegment(sketch, "E31.8.9.11", {"start": v(-89.77, -172) * mm, "end": v(-86.89, -167) * mm});
            skLineSegment(sketch, "E31.8.9.12", {"start": v(-76.5, -173) * mm, "end": v(-70.72, -173) * mm});
            skLineSegment(sketch, "E31.8.9.13", {"start": v(-70.72, -183) * mm, "end": v(-76.5, -183) * mm});
            skLineSegment(sketch, "E31.8.10.0", {"start": v(-70.72, -185) * mm, "end": v(-67.83, -190) * mm});
            skLineSegment(sketch, "E31.8.10.1", {"start": v(-76.5, -195) * mm, "end": v(-79.38, -190) * mm});
            skLineSegment(sketch, "E31.8.10.2", {"start": v(-79.38, -190) * mm, "end": v(-76.5, -185) * mm});
            skLineSegment(sketch, "E31.8.10.3", {"start": v(-78.23, -184) * mm, "end": v(-81.11, -189) * mm});
            skLineSegment(sketch, "E31.8.10.4", {"start": v(-67.83, -190) * mm, "end": v(-70.72, -195) * mm});
            skPoint(sketch, "E31.8.10.5", {"position": v(-73.6, -185) * mm});
            skLineSegment(sketch, "E31.8.10.6", {"start": v(-81.11, -179) * mm, "end": v(-78.23, -184) * mm});
            skLineSegment(sketch, "E31.8.10.7", {"start": v(-86.89, -179) * mm, "end": v(-81.11, -179) * mm});
            skPoint(sketch, "E31.8.10.8", {"position": v(-84, -179) * mm});
            skLineSegment(sketch, "E31.8.10.9", {"start": v(-81.11, -189) * mm, "end": v(-86.89, -189) * mm});
            skLineSegment(sketch, "E31.8.10.10", {"start": v(-86.89, -189) * mm, "end": v(-89.77, -184) * mm});
            skLineSegment(sketch, "E31.8.10.11", {"start": v(-89.77, -184) * mm, "end": v(-86.89, -179) * mm});
            skLineSegment(sketch, "E31.8.10.12", {"start": v(-76.5, -185) * mm, "end": v(-70.72, -185) * mm});
            skLineSegment(sketch, "E31.8.10.13", {"start": v(-70.72, -195) * mm, "end": v(-76.5, -195) * mm});
            skLineSegment(sketch, "E31.8.11.0", {"start": v(-70.72, -197) * mm, "end": v(-67.83, -202) * mm});
            skLineSegment(sketch, "E31.8.11.1", {"start": v(-76.5, -207) * mm, "end": v(-79.38, -202) * mm});
            skLineSegment(sketch, "E31.8.11.2", {"start": v(-79.38, -202) * mm, "end": v(-76.5, -197) * mm});
            skLineSegment(sketch, "E31.8.11.3", {"start": v(-78.23, -196) * mm, "end": v(-81.11, -201) * mm});
            skLineSegment(sketch, "E31.8.11.4", {"start": v(-67.83, -202) * mm, "end": v(-70.72, -207) * mm});
            skPoint(sketch, "E31.8.11.5", {"position": v(-73.6, -197) * mm});
            skLineSegment(sketch, "E31.8.11.6", {"start": v(-81.11, -191) * mm, "end": v(-78.23, -196) * mm});
            skLineSegment(sketch, "E31.8.11.7", {"start": v(-86.89, -191) * mm, "end": v(-81.11, -191) * mm});
            skPoint(sketch, "E31.8.11.8", {"position": v(-84, -191) * mm});
            skLineSegment(sketch, "E31.8.11.9", {"start": v(-81.11, -201) * mm, "end": v(-86.89, -201) * mm});
            skLineSegment(sketch, "E31.8.11.10", {"start": v(-86.89, -201) * mm, "end": v(-89.77, -196) * mm});
            skLineSegment(sketch, "E31.8.11.11", {"start": v(-89.77, -196) * mm, "end": v(-86.89, -191) * mm});
            skLineSegment(sketch, "E31.8.11.12", {"start": v(-76.5, -197) * mm, "end": v(-70.72, -197) * mm});
            skLineSegment(sketch, "E31.8.11.13", {"start": v(-70.72, -207) * mm, "end": v(-76.5, -207) * mm});
            skLineSegment(sketch, "E31.8.12.0", {"start": v(-70.72, -209) * mm, "end": v(-67.83, -214) * mm});
            skLineSegment(sketch, "E31.8.12.1", {"start": v(-76.5, -219) * mm, "end": v(-79.38, -214) * mm});
            skLineSegment(sketch, "E31.8.12.2", {"start": v(-79.38, -214) * mm, "end": v(-76.5, -209) * mm});
            skLineSegment(sketch, "E31.8.12.3", {"start": v(-78.23, -208) * mm, "end": v(-81.11, -213) * mm});
            skLineSegment(sketch, "E31.8.12.4", {"start": v(-67.83, -214) * mm, "end": v(-70.72, -219) * mm});
            skPoint(sketch, "E31.8.12.5", {"position": v(-73.6, -209) * mm});
            skLineSegment(sketch, "E31.8.12.6", {"start": v(-81.11, -203) * mm, "end": v(-78.23, -208) * mm});
            skLineSegment(sketch, "E31.8.12.7", {"start": v(-86.89, -203) * mm, "end": v(-81.11, -203) * mm});
            skPoint(sketch, "E31.8.12.8", {"position": v(-84, -203) * mm});
            skLineSegment(sketch, "E31.8.12.9", {"start": v(-81.11, -213) * mm, "end": v(-86.89, -213) * mm});
            skLineSegment(sketch, "E31.8.12.10", {"start": v(-86.89, -213) * mm, "end": v(-89.77, -208) * mm});
            skLineSegment(sketch, "E31.8.12.11", {"start": v(-89.77, -208) * mm, "end": v(-86.89, -203) * mm});
            skLineSegment(sketch, "E31.8.12.12", {"start": v(-76.5, -209) * mm, "end": v(-70.72, -209) * mm});
            skLineSegment(sketch, "E31.8.12.13", {"start": v(-70.72, -219) * mm, "end": v(-76.5, -219) * mm});
            skLineSegment(sketch, "E31.8.13.0", {"start": v(-70.72, -221) * mm, "end": v(-67.83, -226) * mm});
            skLineSegment(sketch, "E31.8.13.1", {"start": v(-76.5, -231) * mm, "end": v(-79.38, -226) * mm});
            skLineSegment(sketch, "E31.8.13.2", {"start": v(-79.38, -226) * mm, "end": v(-76.5, -221) * mm});
            skLineSegment(sketch, "E31.8.13.3", {"start": v(-78.23, -220) * mm, "end": v(-81.11, -225) * mm});
            skLineSegment(sketch, "E31.8.13.4", {"start": v(-67.83, -226) * mm, "end": v(-70.72, -231) * mm});
            skPoint(sketch, "E31.8.13.5", {"position": v(-73.6, -221) * mm});
            skLineSegment(sketch, "E31.8.13.6", {"start": v(-81.11, -215) * mm, "end": v(-78.23, -220) * mm});
            skLineSegment(sketch, "E31.8.13.7", {"start": v(-86.89, -215) * mm, "end": v(-81.11, -215) * mm});
            skPoint(sketch, "E31.8.13.8", {"position": v(-84, -215) * mm});
            skLineSegment(sketch, "E31.8.13.9", {"start": v(-81.11, -225) * mm, "end": v(-86.89, -225) * mm});
            skLineSegment(sketch, "E31.8.13.10", {"start": v(-86.89, -225) * mm, "end": v(-89.77, -220) * mm});
            skLineSegment(sketch, "E31.8.13.11", {"start": v(-89.77, -220) * mm, "end": v(-86.89, -215) * mm});
            skLineSegment(sketch, "E31.8.13.12", {"start": v(-76.5, -221) * mm, "end": v(-70.72, -221) * mm});
            skLineSegment(sketch, "E31.8.13.13", {"start": v(-70.72, -231) * mm, "end": v(-76.5, -231) * mm});
            skLineSegment(sketch, "E31.8.14.0", {"start": v(-70.72, -233) * mm, "end": v(-67.83, -238) * mm});
            skLineSegment(sketch, "E31.8.14.1", {"start": v(-76.5, -243) * mm, "end": v(-79.38, -238) * mm});
            skLineSegment(sketch, "E31.8.14.2", {"start": v(-79.38, -238) * mm, "end": v(-76.5, -233) * mm});
            skLineSegment(sketch, "E31.8.14.3", {"start": v(-78.23, -232) * mm, "end": v(-81.11, -237) * mm});
            skLineSegment(sketch, "E31.8.14.4", {"start": v(-67.83, -238) * mm, "end": v(-70.72, -243) * mm});
            skPoint(sketch, "E31.8.14.5", {"position": v(-73.6, -233) * mm});
            skLineSegment(sketch, "E31.8.14.6", {"start": v(-81.11, -227) * mm, "end": v(-78.23, -232) * mm});
            skLineSegment(sketch, "E31.8.14.7", {"start": v(-86.89, -227) * mm, "end": v(-81.11, -227) * mm});
            skPoint(sketch, "E31.8.14.8", {"position": v(-84, -227) * mm});
            skLineSegment(sketch, "E31.8.14.9", {"start": v(-81.11, -237) * mm, "end": v(-86.89, -237) * mm});
            skLineSegment(sketch, "E31.8.14.10", {"start": v(-86.89, -237) * mm, "end": v(-89.77, -232) * mm});
            skLineSegment(sketch, "E31.8.14.11", {"start": v(-89.77, -232) * mm, "end": v(-86.89, -227) * mm});
            skLineSegment(sketch, "E31.8.14.12", {"start": v(-76.5, -233) * mm, "end": v(-70.72, -233) * mm});
            skLineSegment(sketch, "E31.8.14.13", {"start": v(-70.72, -243) * mm, "end": v(-76.5, -243) * mm});
            skLineSegment(sketch, "E31.8.15.0", {"start": v(-70.72, -245) * mm, "end": v(-67.83, -250) * mm});
            skLineSegment(sketch, "E31.8.15.1", {"start": v(-76.5, -255) * mm, "end": v(-79.38, -250) * mm});
            skLineSegment(sketch, "E31.8.15.2", {"start": v(-79.38, -250) * mm, "end": v(-76.5, -245) * mm});
            skLineSegment(sketch, "E31.8.15.3", {"start": v(-78.23, -244) * mm, "end": v(-81.11, -249) * mm});
            skLineSegment(sketch, "E31.8.15.4", {"start": v(-67.83, -250) * mm, "end": v(-70.72, -255) * mm});
            skPoint(sketch, "E31.8.15.5", {"position": v(-73.6, -245) * mm});
            skLineSegment(sketch, "E31.8.15.6", {"start": v(-81.11, -239) * mm, "end": v(-78.23, -244) * mm});
            skLineSegment(sketch, "E31.8.15.7", {"start": v(-86.89, -239) * mm, "end": v(-81.11, -239) * mm});
            skPoint(sketch, "E31.8.15.8", {"position": v(-84, -239) * mm});
            skLineSegment(sketch, "E31.8.15.9", {"start": v(-81.11, -249) * mm, "end": v(-86.89, -249) * mm});
            skLineSegment(sketch, "E31.8.15.10", {"start": v(-86.89, -249) * mm, "end": v(-89.77, -244) * mm});
            skLineSegment(sketch, "E31.8.15.11", {"start": v(-89.77, -244) * mm, "end": v(-86.89, -239) * mm});
            skLineSegment(sketch, "E31.8.15.12", {"start": v(-76.5, -245) * mm, "end": v(-70.72, -245) * mm});
            skLineSegment(sketch, "E31.8.15.13", {"start": v(-70.72, -255) * mm, "end": v(-76.5, -255) * mm});
            skLineSegment(sketch, "E31.8.16.3", {"start": v(-78.23, -256) * mm, "end": v(-81.11, -261) * mm});
            skLineSegment(sketch, "E31.8.16.6", {"start": v(-81.11, -251) * mm, "end": v(-78.23, -256) * mm});
            skLineSegment(sketch, "E31.8.16.7", {"start": v(-86.89, -251) * mm, "end": v(-81.11, -251) * mm});
            skPoint(sketch, "E31.8.16.8", {"position": v(-84, -251) * mm});
            skLineSegment(sketch, "E31.8.16.9", {"start": v(-81.11, -261) * mm, "end": v(-86.89, -261) * mm});
            skLineSegment(sketch, "E31.8.16.10", {"start": v(-86.89, -261) * mm, "end": v(-89.77, -256) * mm});
            skLineSegment(sketch, "E31.8.16.11", {"start": v(-89.77, -256) * mm, "end": v(-86.89, -251) * mm});
            skLineSegment(sketch, "E31.9.0.0", {"start": v(-91.72, -65) * mm, "end": v(-88.83, -70) * mm});
            skLineSegment(sketch, "E31.9.0.1", {"start": v(-97.5, -75) * mm, "end": v(-100.38, -70) * mm});
            skLineSegment(sketch, "E31.9.0.2", {"start": v(-100.38, -70) * mm, "end": v(-97.5, -65) * mm});
            skLineSegment(sketch, "E31.9.0.4", {"start": v(-88.83, -70) * mm, "end": v(-91.72, -75) * mm});
            skPoint(sketch, "E31.9.0.5", {"position": v(-94.6, -65) * mm});
            skLineSegment(sketch, "E31.9.0.12", {"start": v(-97.5, -65) * mm, "end": v(-91.72, -65) * mm});
            skLineSegment(sketch, "E31.9.0.13", {"start": v(-91.72, -75) * mm, "end": v(-97.5, -75) * mm});
            skLineSegment(sketch, "E31.9.1.0", {"start": v(-91.72, -77) * mm, "end": v(-88.83, -82) * mm});
            skLineSegment(sketch, "E31.9.1.1", {"start": v(-97.5, -87) * mm, "end": v(-100.38, -82) * mm});
            skLineSegment(sketch, "E31.9.1.2", {"start": v(-100.38, -82) * mm, "end": v(-97.5, -77) * mm});
            skLineSegment(sketch, "E31.9.1.4", {"start": v(-88.83, -82) * mm, "end": v(-91.72, -87) * mm});
            skPoint(sketch, "E31.9.1.5", {"position": v(-94.6, -77) * mm});
            skLineSegment(sketch, "E31.9.1.12", {"start": v(-97.5, -77) * mm, "end": v(-91.72, -77) * mm});
            skLineSegment(sketch, "E31.9.1.13", {"start": v(-91.72, -87) * mm, "end": v(-97.5, -87) * mm});
            skLineSegment(sketch, "E31.9.2.0", {"start": v(-91.72, -89) * mm, "end": v(-88.83, -94) * mm});
            skLineSegment(sketch, "E31.9.2.1", {"start": v(-97.5, -99) * mm, "end": v(-100.38, -94) * mm});
            skLineSegment(sketch, "E31.9.2.2", {"start": v(-100.38, -94) * mm, "end": v(-97.5, -89) * mm});
            skLineSegment(sketch, "E31.9.2.4", {"start": v(-88.83, -94) * mm, "end": v(-91.72, -99) * mm});
            skPoint(sketch, "E31.9.2.5", {"position": v(-94.6, -89) * mm});
            skLineSegment(sketch, "E31.9.2.12", {"start": v(-97.5, -89) * mm, "end": v(-91.72, -89) * mm});
            skLineSegment(sketch, "E31.9.2.13", {"start": v(-91.72, -99) * mm, "end": v(-97.5, -99) * mm});
            skLineSegment(sketch, "E31.9.3.0", {"start": v(-91.72, -101) * mm, "end": v(-88.83, -106) * mm});
            skLineSegment(sketch, "E31.9.3.1", {"start": v(-97.5, -111) * mm, "end": v(-100.38, -106) * mm});
            skLineSegment(sketch, "E31.9.3.2", {"start": v(-100.38, -106) * mm, "end": v(-97.5, -101) * mm});
            skLineSegment(sketch, "E31.9.3.4", {"start": v(-88.83, -106) * mm, "end": v(-91.72, -111) * mm});
            skPoint(sketch, "E31.9.3.5", {"position": v(-94.6, -101) * mm});
            skLineSegment(sketch, "E31.9.3.12", {"start": v(-97.5, -101) * mm, "end": v(-91.72, -101) * mm});
            skLineSegment(sketch, "E31.9.3.13", {"start": v(-91.72, -111) * mm, "end": v(-97.5, -111) * mm});
            skLineSegment(sketch, "E31.9.4.0", {"start": v(-91.72, -113) * mm, "end": v(-88.83, -118) * mm});
            skLineSegment(sketch, "E31.9.4.1", {"start": v(-97.5, -123) * mm, "end": v(-100.38, -118) * mm});
            skLineSegment(sketch, "E31.9.4.2", {"start": v(-100.38, -118) * mm, "end": v(-97.5, -113) * mm});
            skLineSegment(sketch, "E31.9.4.4", {"start": v(-88.83, -118) * mm, "end": v(-91.72, -123) * mm});
            skPoint(sketch, "E31.9.4.5", {"position": v(-94.6, -113) * mm});
            skLineSegment(sketch, "E31.9.4.12", {"start": v(-97.5, -113) * mm, "end": v(-91.72, -113) * mm});
            skLineSegment(sketch, "E31.9.4.13", {"start": v(-91.72, -123) * mm, "end": v(-97.5, -123) * mm});
            skLineSegment(sketch, "E31.9.5.0", {"start": v(-91.72, -125) * mm, "end": v(-88.83, -130) * mm});
            skLineSegment(sketch, "E31.9.5.1", {"start": v(-97.5, -135) * mm, "end": v(-100.38, -130) * mm});
            skLineSegment(sketch, "E31.9.5.2", {"start": v(-100.38, -130) * mm, "end": v(-97.5, -125) * mm});
            skLineSegment(sketch, "E31.9.5.4", {"start": v(-88.83, -130) * mm, "end": v(-91.72, -135) * mm});
            skPoint(sketch, "E31.9.5.5", {"position": v(-94.6, -125) * mm});
            skLineSegment(sketch, "E31.9.5.12", {"start": v(-97.5, -125) * mm, "end": v(-91.72, -125) * mm});
            skLineSegment(sketch, "E31.9.5.13", {"start": v(-91.72, -135) * mm, "end": v(-97.5, -135) * mm});
            skLineSegment(sketch, "E31.9.6.0", {"start": v(-91.72, -137) * mm, "end": v(-88.83, -142) * mm});
            skLineSegment(sketch, "E31.9.6.1", {"start": v(-97.5, -147) * mm, "end": v(-100.38, -142) * mm});
            skLineSegment(sketch, "E31.9.6.2", {"start": v(-100.38, -142) * mm, "end": v(-97.5, -137) * mm});
            skLineSegment(sketch, "E31.9.6.4", {"start": v(-88.83, -142) * mm, "end": v(-91.72, -147) * mm});
            skPoint(sketch, "E31.9.6.5", {"position": v(-94.6, -137) * mm});
            skLineSegment(sketch, "E31.9.6.12", {"start": v(-97.5, -137) * mm, "end": v(-91.72, -137) * mm});
            skLineSegment(sketch, "E31.9.6.13", {"start": v(-91.72, -147) * mm, "end": v(-97.5, -147) * mm});
            skLineSegment(sketch, "E31.9.7.0", {"start": v(-91.72, -149) * mm, "end": v(-88.83, -154) * mm});
            skLineSegment(sketch, "E31.9.7.1", {"start": v(-97.5, -159) * mm, "end": v(-100.38, -154) * mm});
            skLineSegment(sketch, "E31.9.7.2", {"start": v(-100.38, -154) * mm, "end": v(-97.5, -149) * mm});
            skLineSegment(sketch, "E31.9.7.4", {"start": v(-88.83, -154) * mm, "end": v(-91.72, -159) * mm});
            skPoint(sketch, "E31.9.7.5", {"position": v(-94.6, -149) * mm});
            skLineSegment(sketch, "E31.9.7.12", {"start": v(-97.5, -149) * mm, "end": v(-91.72, -149) * mm});
            skLineSegment(sketch, "E31.9.7.13", {"start": v(-91.72, -159) * mm, "end": v(-97.5, -159) * mm});
            skLineSegment(sketch, "E31.9.8.0", {"start": v(-91.72, -161) * mm, "end": v(-88.83, -166) * mm});
            skLineSegment(sketch, "E31.9.8.1", {"start": v(-97.5, -171) * mm, "end": v(-100.38, -166) * mm});
            skLineSegment(sketch, "E31.9.8.2", {"start": v(-100.38, -166) * mm, "end": v(-97.5, -161) * mm});
            skLineSegment(sketch, "E31.9.8.4", {"start": v(-88.83, -166) * mm, "end": v(-91.72, -171) * mm});
            skPoint(sketch, "E31.9.8.5", {"position": v(-94.6, -161) * mm});
            skLineSegment(sketch, "E31.9.8.12", {"start": v(-97.5, -161) * mm, "end": v(-91.72, -161) * mm});
            skLineSegment(sketch, "E31.9.8.13", {"start": v(-91.72, -171) * mm, "end": v(-97.5, -171) * mm});
            skLineSegment(sketch, "E31.9.9.0", {"start": v(-91.72, -173) * mm, "end": v(-88.83, -178) * mm});
            skLineSegment(sketch, "E31.9.9.1", {"start": v(-97.5, -183) * mm, "end": v(-100.38, -178) * mm});
            skLineSegment(sketch, "E31.9.9.2", {"start": v(-100.38, -178) * mm, "end": v(-97.5, -173) * mm});
            skLineSegment(sketch, "E31.9.9.4", {"start": v(-88.83, -178) * mm, "end": v(-91.72, -183) * mm});
            skPoint(sketch, "E31.9.9.5", {"position": v(-94.6, -173) * mm});
            skLineSegment(sketch, "E31.9.9.12", {"start": v(-97.5, -173) * mm, "end": v(-91.72, -173) * mm});
            skLineSegment(sketch, "E31.9.9.13", {"start": v(-91.72, -183) * mm, "end": v(-97.5, -183) * mm});
            skLineSegment(sketch, "E31.9.10.0", {"start": v(-91.72, -185) * mm, "end": v(-88.83, -190) * mm});
            skLineSegment(sketch, "E31.9.10.1", {"start": v(-97.5, -195) * mm, "end": v(-100.38, -190) * mm});
            skLineSegment(sketch, "E31.9.10.2", {"start": v(-100.38, -190) * mm, "end": v(-97.5, -185) * mm});
            skLineSegment(sketch, "E31.9.10.4", {"start": v(-88.83, -190) * mm, "end": v(-91.72, -195) * mm});
            skPoint(sketch, "E31.9.10.5", {"position": v(-94.6, -185) * mm});
            skLineSegment(sketch, "E31.9.10.12", {"start": v(-97.5, -185) * mm, "end": v(-91.72, -185) * mm});
            skLineSegment(sketch, "E31.9.10.13", {"start": v(-91.72, -195) * mm, "end": v(-97.5, -195) * mm});
            skLineSegment(sketch, "E31.9.11.0", {"start": v(-91.72, -197) * mm, "end": v(-88.83, -202) * mm});
            skLineSegment(sketch, "E31.9.11.1", {"start": v(-97.5, -207) * mm, "end": v(-100.38, -202) * mm});
            skLineSegment(sketch, "E31.9.11.2", {"start": v(-100.38, -202) * mm, "end": v(-97.5, -197) * mm});
            skLineSegment(sketch, "E31.9.11.4", {"start": v(-88.83, -202) * mm, "end": v(-91.72, -207) * mm});
            skPoint(sketch, "E31.9.11.5", {"position": v(-94.6, -197) * mm});
            skLineSegment(sketch, "E31.9.11.12", {"start": v(-97.5, -197) * mm, "end": v(-91.72, -197) * mm});
            skLineSegment(sketch, "E31.9.11.13", {"start": v(-91.72, -207) * mm, "end": v(-97.5, -207) * mm});
            skLineSegment(sketch, "E31.9.12.0", {"start": v(-91.72, -209) * mm, "end": v(-88.83, -214) * mm});
            skLineSegment(sketch, "E31.9.12.1", {"start": v(-97.5, -219) * mm, "end": v(-100.38, -214) * mm});
            skLineSegment(sketch, "E31.9.12.2", {"start": v(-100.38, -214) * mm, "end": v(-97.5, -209) * mm});
            skLineSegment(sketch, "E31.9.12.4", {"start": v(-88.83, -214) * mm, "end": v(-91.72, -219) * mm});
            skPoint(sketch, "E31.9.12.5", {"position": v(-94.6, -209) * mm});
            skLineSegment(sketch, "E31.9.12.12", {"start": v(-97.5, -209) * mm, "end": v(-91.72, -209) * mm});
            skLineSegment(sketch, "E31.9.12.13", {"start": v(-91.72, -219) * mm, "end": v(-97.5, -219) * mm});
            skLineSegment(sketch, "E31.9.13.0", {"start": v(-91.72, -221) * mm, "end": v(-88.83, -226) * mm});
            skLineSegment(sketch, "E31.9.13.1", {"start": v(-97.5, -231) * mm, "end": v(-100.38, -226) * mm});
            skLineSegment(sketch, "E31.9.13.2", {"start": v(-100.38, -226) * mm, "end": v(-97.5, -221) * mm});
            skLineSegment(sketch, "E31.9.13.4", {"start": v(-88.83, -226) * mm, "end": v(-91.72, -231) * mm});
            skPoint(sketch, "E31.9.13.5", {"position": v(-94.6, -221) * mm});
            skLineSegment(sketch, "E31.9.13.12", {"start": v(-97.5, -221) * mm, "end": v(-91.72, -221) * mm});
            skLineSegment(sketch, "E31.9.13.13", {"start": v(-91.72, -231) * mm, "end": v(-97.5, -231) * mm});
            skLineSegment(sketch, "E31.9.14.0", {"start": v(-91.72, -233) * mm, "end": v(-88.83, -238) * mm});
            skLineSegment(sketch, "E31.9.14.1", {"start": v(-97.5, -243) * mm, "end": v(-100.38, -238) * mm});
            skLineSegment(sketch, "E31.9.14.2", {"start": v(-100.38, -238) * mm, "end": v(-97.5, -233) * mm});
            skLineSegment(sketch, "E31.9.14.4", {"start": v(-88.83, -238) * mm, "end": v(-91.72, -243) * mm});
            skPoint(sketch, "E31.9.14.5", {"position": v(-94.6, -233) * mm});
            skLineSegment(sketch, "E31.9.14.12", {"start": v(-97.5, -233) * mm, "end": v(-91.72, -233) * mm});
            skLineSegment(sketch, "E31.9.14.13", {"start": v(-91.72, -243) * mm, "end": v(-97.5, -243) * mm});
            skLineSegment(sketch, "E31.9.15.0", {"start": v(-91.72, -245) * mm, "end": v(-88.83, -250) * mm});
            skLineSegment(sketch, "E31.9.15.1", {"start": v(-97.5, -255) * mm, "end": v(-100.38, -250) * mm});
            skLineSegment(sketch, "E31.9.15.2", {"start": v(-100.38, -250) * mm, "end": v(-97.5, -245) * mm});
            skLineSegment(sketch, "E31.9.15.4", {"start": v(-88.83, -250) * mm, "end": v(-91.72, -255) * mm});
            skPoint(sketch, "E31.9.15.5", {"position": v(-94.6, -245) * mm});
            skLineSegment(sketch, "E31.9.15.12", {"start": v(-97.5, -245) * mm, "end": v(-91.72, -245) * mm});
            skLineSegment(sketch, "E31.9.15.13", {"start": v(-91.72, -255) * mm, "end": v(-97.5, -255) * mm});
            skLineSegment(sketch, "E31.direction1", {"start": v(81.11, -69) * mm, "end": v(60.11, -69) * mm, "construction": true});
            skLineSegment(sketch, "E31.direction2", {"start": v(81.11, -69) * mm, "end": v(81.11, -81) * mm, "construction": true});
            skSolve(sketch);
        }
        {
            var Q0;
            Q0=makeQuery(id+"F5.imprint","IMPRINT",FACE,{"disambiguationData":[TD([[makeQuery(id+"F5.imprint","IMPRINT",EDGE,{"derivedFrom":sQuery(id+"F5.wireOp",EDGE,"E31.8.0.3")}),-1.0]])]});
            var Q1;
            Q1=makeQuery(id+"F5.imprint","IMPRINT",FACE,{"disambiguationData":[TD([[makeQuery(id+"F5.imprint","IMPRINT",EDGE,{"derivedFrom":sQuery(id+"F5.wireOp",EDGE,"E31.9.0.0")}),-1.0]])]});
            var Q2;
            Q2=makeQuery(id+"F5.imprint","IMPRINT",FACE,{"disambiguationData":[TD([[makeQuery(id+"F5.imprint","IMPRINT",EDGE,{"derivedFrom":sQuery(id+"F5.wireOp",EDGE,"E31.8.1.3")}),-1.0]])]});
            var Q3;
            Q3=makeQuery(id+"F5.imprint","IMPRINT",FACE,{"disambiguationData":[TD([[makeQuery(id+"F5.imprint","IMPRINT",EDGE,{"derivedFrom":sQuery(id+"F5.wireOp",EDGE,"E31.9.1.0")}),-1.0]])]});
            var Q4;
            Q4=makeQuery(id+"F5.imprint","IMPRINT",FACE,{"disambiguationData":[TD([[makeQuery(id+"F5.imprint","IMPRINT",EDGE,{"derivedFrom":sQuery(id+"F5.wireOp",EDGE,"E31.8.0.0")}),-1.0]])]});
            var Q5;
            Q5=makeQuery(id+"F5.imprint","IMPRINT",FACE,{"disambiguationData":[TD([[makeQuery(id+"F5.imprint","IMPRINT",EDGE,{"derivedFrom":sQuery(id+"F5.wireOp",EDGE,"E31.1.2.3")}),-1.0]])]});
            var Q6;
            Q6=makeQuery(id+"F5.imprint","IMPRINT",FACE,{"disambiguationData":[TD([[makeQuery(id+"F5.imprint","IMPRINT",EDGE,{"derivedFrom":sQuery(id+"F5.wireOp",EDGE,"E31.0.11.0")}),-1.0]])]});
            var Q7;
            Q7=makeQuery(id+"F5.imprint","IMPRINT",FACE,{"disambiguationData":[TD([[makeQuery(id+"F5.imprint","IMPRINT",EDGE,{"derivedFrom":sQuery(id+"F5.wireOp",EDGE,"E31.3.1.3")}),-1.0]])]});
            var Q8;
            Q8=makeQuery(id+"F5.imprint","IMPRINT",FACE,{"disambiguationData":[TD([[makeQuery(id+"F5.imprint","IMPRINT",EDGE,{"derivedFrom":sQuery(id+"F5.wireOp",EDGE,"E31.8.2.0")}),-1.0]])]});
            var Q9;
            Q9=makeQuery(id+"F5.imprint","IMPRINT",FACE,{"disambiguationData":[TD([[makeQuery(id+"F5.imprint","IMPRINT",EDGE,{"derivedFrom":sQuery(id+"F5.wireOp",EDGE,"E31.7.10.3")}),-1.0]])]});
            var Q10;
            Q10=makeQuery(id+"F5.imprint","IMPRINT",FACE,{"disambiguationData":[TD([[makeQuery(id+"F5.imprint","IMPRINT",EDGE,{"derivedFrom":sQuery(id+"F5.wireOp",EDGE,"E31.8.10.0")}),-1.0]])]});
            var Q11;
            Q11=makeQuery(id+"F5.imprint","IMPRINT",FACE,{"disambiguationData":[TD([[makeQuery(id+"F5.imprint","IMPRINT",EDGE,{"derivedFrom":sQuery(id+"F5.wireOp",EDGE,"E31.5.11.3")}),-1.0]])]});
            var Q12;
            Q12=makeQuery(id+"F5.imprint","IMPRINT",FACE,{"disambiguationData":[TD([[makeQuery(id+"F5.imprint","IMPRINT",EDGE,{"derivedFrom":sQuery(id+"F5.wireOp",EDGE,"E31.9.3.0")}),-1.0]])]});
            var Q13;
            Q13=makeQuery(id+"F5.imprint","IMPRINT",FACE,{"disambiguationData":[TD([[makeQuery(id+"F5.imprint","IMPRINT",EDGE,{"derivedFrom":sQuery(id+"F5.wireOp",EDGE,"E31.6.3.0")}),-1.0]])]});
            var Q14;
            Q14=makeQuery(id+"F5.imprint","IMPRINT",FACE,{"disambiguationData":[TD([[makeQuery(id+"F5.imprint","IMPRINT",EDGE,{"derivedFrom":sQuery(id+"F5.wireOp",EDGE,"E31.6.11.0")}),-1.0]])]});
            var Q15;
            Q15=makeQuery(id+"F5.imprint","IMPRINT",FACE,{"disambiguationData":[TD([[makeQuery(id+"F5.imprint","IMPRINT",EDGE,{"derivedFrom":sQuery(id+"F5.wireOp",EDGE,"E31.3.12.3")}),-1.0]])]});
            var Q16;
            Q16=makeQuery(id+"F5.imprint","IMPRINT",FACE,{"disambiguationData":[TD([[makeQuery(id+"F5.imprint","IMPRINT",EDGE,{"derivedFrom":sQuery(id+"F5.wireOp",EDGE,"E31.7.2.3")}),-1.0]])]});
            var Q17;
            Q17=makeQuery(id+"F5.imprint","IMPRINT",FACE,{"disambiguationData":[TD([[makeQuery(id+"F5.imprint","IMPRINT",EDGE,{"derivedFrom":sQuery(id+"F5.wireOp",EDGE,"E31.4.4.0")}),-1.0]])]});
            var Q18;
            Q18=makeQuery(id+"F5.imprint","IMPRINT",FACE,{"disambiguationData":[TD([[makeQuery(id+"F5.imprint","IMPRINT",EDGE,{"derivedFrom":sQuery(id+"F5.wireOp",EDGE,"E31.4.12.0")}),-1.0]])]});
            var Q19;
            Q19=makeQuery(id+"F5.imprint","IMPRINT",FACE,{"disambiguationData":[TD([[makeQuery(id+"F5.imprint","IMPRINT",EDGE,{"derivedFrom":sQuery(id+"F5.wireOp",EDGE,"E31.5.3.3")}),-1.0]])]});
            var Q20;
            Q20=makeQuery(id+"F5.imprint","IMPRINT",FACE,{"disambiguationData":[TD([[makeQuery(id+"F5.imprint","IMPRINT",EDGE,{"derivedFrom":sQuery(id+"F5.wireOp",EDGE,"E31.1.13.3")}),-1.0]])]});
            var Q21;
            Q21=makeQuery(id+"F5.imprint","IMPRINT",FACE,{"disambiguationData":[TD([[makeQuery(id+"F5.imprint","IMPRINT",EDGE,{"derivedFrom":sQuery(id+"F5.wireOp",EDGE,"E31.2.13.0")}),-1.0]])]});
            var Q22;
            Q22=makeQuery(id+"F5.imprint","IMPRINT",FACE,{"disambiguationData":[TD([[makeQuery(id+"F5.imprint","IMPRINT",EDGE,{"derivedFrom":sQuery(id+"F5.wireOp",EDGE,"E31.2.5.0")}),-1.0]])]});
            var Q23;
            Q23=makeQuery(id+"F5.imprint","IMPRINT",FACE,{"disambiguationData":[TD([[makeQuery(id+"F5.imprint","IMPRINT",EDGE,{"derivedFrom":sQuery(id+"F5.wireOp",EDGE,"E31.3.4.3")}),-1.0]])]});
            var Q24;
            Q24=makeQuery(id+"F5.imprint","IMPRINT",FACE,{"disambiguationData":[TD([[makeQuery(id+"F5.imprint","IMPRINT",EDGE,{"derivedFrom":sQuery(id+"F5.wireOp",EDGE,"E31.1.5.3")}),-1.0]])]});
            var Q25;
            Q25=makeQuery(id+"F5.imprint","IMPRINT",FACE,{"disambiguationData":[TD([[makeQuery(id+"F5.imprint","IMPRINT",EDGE,{"derivedFrom":sQuery(id+"F5.wireOp",EDGE,"E31.0.14.0")}),-1.0]])]});
            var Q26;
            Q26=makeQuery(id+"F5.imprint","IMPRINT",FACE,{"disambiguationData":[TD([[makeQuery(id+"F5.imprint","IMPRINT",EDGE,{"derivedFrom":sQuery(id+"F5.wireOp",EDGE,"E31.6.2.3")}),-1.0]])]});
            var Q27;
            Q27=makeQuery(id+"F5.imprint","IMPRINT",FACE,{"disambiguationData":[TD([[makeQuery(id+"F5.imprint","IMPRINT",EDGE,{"derivedFrom":sQuery(id+"F5.wireOp",EDGE,"E31.5.11.0")}),-1.0]])]});
            var Q28;
            Q28=makeQuery(id+"F5.imprint","IMPRINT",FACE,{"disambiguationData":[TD([[makeQuery(id+"F5.imprint","IMPRINT",EDGE,{"derivedFrom":sQuery(id+"F5.wireOp",EDGE,"E31.6.10.3")}),-1.0]])]});
            var Q29;
            Q29=makeQuery(id+"F5.imprint","IMPRINT",FACE,{"disambiguationData":[TD([[makeQuery(id+"F5.imprint","IMPRINT",EDGE,{"derivedFrom":sQuery(id+"F5.wireOp",EDGE,"E31.7.2.0")}),-1.0]])]});
            var Q30;
            Q30=makeQuery(id+"F5.imprint","IMPRINT",FACE,{"disambiguationData":[TD([[makeQuery(id+"F5.imprint","IMPRINT",EDGE,{"derivedFrom":sQuery(id+"F5.wireOp",EDGE,"E31.3.12.0")}),-1.0]])]});
            var Q31;
            Q31=makeQuery(id+"F5.imprint","IMPRINT",FACE,{"disambiguationData":[TD([[makeQuery(id+"F5.imprint","IMPRINT",EDGE,{"derivedFrom":sQuery(id+"F5.wireOp",EDGE,"E31.4.3.3")}),-1.0]])]});
            var Q32;
            Q32=makeQuery(id+"F5.imprint","IMPRINT",FACE,{"disambiguationData":[TD([[makeQuery(id+"F5.imprint","IMPRINT",EDGE,{"derivedFrom":sQuery(id+"F5.wireOp",EDGE,"E31.5.3.0")}),-1.0]])]});
            var Q33;
            Q33=makeQuery(id+"F5.imprint","IMPRINT",FACE,{"disambiguationData":[TD([[makeQuery(id+"F5.imprint","IMPRINT",EDGE,{"derivedFrom":sQuery(id+"F5.wireOp",EDGE,"E31.4.11.3")}),-1.0]])]});
            var Q34;
            Q34=makeQuery(id+"F5.imprint","IMPRINT",FACE,{"disambiguationData":[TD([[makeQuery(id+"F5.imprint","IMPRINT",EDGE,{"derivedFrom":sQuery(id+"F5.wireOp",EDGE,"E31.1.13.0")}),-1.0]])]});
            var Q35;
            Q35=makeQuery(id+"F5.imprint","IMPRINT",FACE,{"disambiguationData":[TD([[makeQuery(id+"F5.imprint","IMPRINT",EDGE,{"derivedFrom":sQuery(id+"F5.wireOp",EDGE,"E31.2.4.3")}),-1.0]])]});
            var Q36;
            Q36=makeQuery(id+"F5.imprint","IMPRINT",FACE,{"disambiguationData":[TD([[makeQuery(id+"F5.imprint","IMPRINT",EDGE,{"derivedFrom":sQuery(id+"F5.wireOp",EDGE,"E31.2.12.3")}),-1.0]])]});
            var Q37;
            Q37=makeQuery(id+"F5.imprint","IMPRINT",FACE,{"disambiguationData":[TD([[makeQuery(id+"F5.imprint","IMPRINT",EDGE,{"derivedFrom":sQuery(id+"F5.wireOp",EDGE,"E31.3.4.0")}),-1.0]])]});
            var Q38;
            Q38=makeQuery(id+"F5.imprint","IMPRINT",FACE,{"disambiguationData":[TD([[makeQuery(id+"F5.imprint","IMPRINT",EDGE,{"derivedFrom":sQuery(id+"F5.wireOp",EDGE,"E31.0.13.3")}),-1.0]])]});
            var Q39;
            Q39=makeQuery(id+"F5.imprint","IMPRINT",FACE,{"disambiguationData":[TD([[makeQuery(id+"F5.imprint","IMPRINT",EDGE,{"derivedFrom":sQuery(id+"F5.wireOp",EDGE,"E31.1.5.0")}),-1.0]])]});
            var Q40;
            Q40=makeQuery(id+"F5.imprint","IMPRINT",FACE,{"disambiguationData":[TD([[makeQuery(id+"F5.imprint","IMPRINT",EDGE,{"derivedFrom":sQuery(id+"F5.wireOp",EDGE,"E31.7.10.0")}),-1.0]])]});
            var Q41;
            Q41=makeQuery(id+"F5.imprint","IMPRINT",FACE,{"disambiguationData":[TD([[makeQuery(id+"F5.imprint","IMPRINT",EDGE,{"derivedFrom":sQuery(id+"F5.wireOp",EDGE,"E31.8.9.3")}),-1.0]])]});
            var Q42;
            Q42=makeQuery(id+"F5.imprint","IMPRINT",FACE,{"disambiguationData":[TD([[makeQuery(id+"F5.imprint","IMPRINT",EDGE,{"derivedFrom":sQuery(id+"F5.wireOp",EDGE,"E31.9.2.0")}),-1.0]])]});
            var Q43;
            Q43=makeQuery(id+"F5.imprint","IMPRINT",FACE,{"disambiguationData":[TD([[makeQuery(id+"F5.imprint","IMPRINT",EDGE,{"derivedFrom":sQuery(id+"F5.wireOp",EDGE,"E31.3.11.3")}),-1.0]])]});
            var Q44;
            Q44=makeQuery(id+"F5.imprint","IMPRINT",FACE,{"disambiguationData":[TD([[makeQuery(id+"F5.imprint","IMPRINT",EDGE,{"derivedFrom":sQuery(id+"F5.wireOp",EDGE,"E31.4.3.0")}),-1.0]])]});
            var Q45;
            Q45=makeQuery(id+"F5.imprint","IMPRINT",FACE,{"disambiguationData":[TD([[makeQuery(id+"F5.imprint","IMPRINT",EDGE,{"derivedFrom":sQuery(id+"F5.wireOp",EDGE,"E31.4.11.0")}),-1.0]])]});
            var Q46;
            Q46=makeQuery(id+"F5.imprint","IMPRINT",FACE,{"disambiguationData":[TD([[makeQuery(id+"F5.imprint","IMPRINT",EDGE,{"derivedFrom":sQuery(id+"F5.wireOp",EDGE,"E31.5.2.3")}),-1.0]])]});
            var Q47;
            Q47=makeQuery(id+"F5.imprint","IMPRINT",FACE,{"disambiguationData":[TD([[makeQuery(id+"F5.imprint","IMPRINT",EDGE,{"derivedFrom":sQuery(id+"F5.wireOp",EDGE,"E31.1.12.3")}),-1.0]])]});
            var Q48;
            Q48=makeQuery(id+"F5.imprint","IMPRINT",FACE,{"disambiguationData":[TD([[makeQuery(id+"F5.imprint","IMPRINT",EDGE,{"derivedFrom":sQuery(id+"F5.wireOp",EDGE,"E31.2.12.0")}),-1.0]])]});
            var Q49;
            Q49=makeQuery(id+"F5.imprint","IMPRINT",FACE,{"disambiguationData":[TD([[makeQuery(id+"F5.imprint","IMPRINT",EDGE,{"derivedFrom":sQuery(id+"F5.wireOp",EDGE,"E31.2.4.0")}),-1.0]])]});
            var Q50;
            Q50=makeQuery(id+"F5.imprint","IMPRINT",FACE,{"disambiguationData":[TD([[makeQuery(id+"F5.imprint","IMPRINT",EDGE,{"derivedFrom":sQuery(id+"F5.wireOp",EDGE,"E31.3.3.3")}),-1.0]])]});
            var Q51;
            Q51=makeQuery(id+"F5.imprint","IMPRINT",FACE,{"disambiguationData":[TD([[makeQuery(id+"F5.imprint","IMPRINT",EDGE,{"derivedFrom":sQuery(id+"F5.wireOp",EDGE,"E31.0.13.0")}),-1.0]])]});
            var Q52;
            Q52=makeQuery(id+"F5.imprint","IMPRINT",FACE,{"disambiguationData":[TD([[makeQuery(id+"F5.imprint","IMPRINT",EDGE,{"derivedFrom":sQuery(id+"F5.wireOp",EDGE,"E31.1.4.3")}),-1.0]])]});
            var Q53;
            Q53=makeQuery(id+"F5.imprint","IMPRINT",FACE,{"disambiguationData":[TD([[makeQuery(id+"F5.imprint","IMPRINT",EDGE,{"derivedFrom":sQuery(id+"F5.wireOp",EDGE,"E31.7.9.3")}),-1.0]])]});
            var Q54;
            Q54=makeQuery(id+"F5.imprint","IMPRINT",FACE,{"disambiguationData":[TD([[makeQuery(id+"F5.imprint","IMPRINT",EDGE,{"derivedFrom":sQuery(id+"F5.wireOp",EDGE,"E31.8.1.0")}),-1.0]])]});
            var Q55;
            Q55=makeQuery(id+"F5.imprint","IMPRINT",FACE,{"disambiguationData":[TD([[makeQuery(id+"F5.imprint","IMPRINT",EDGE,{"derivedFrom":sQuery(id+"F5.wireOp",EDGE,"E31.8.9.0")}),-1.0]])]});
            var Q56;
            Q56=makeQuery(id+"F5.imprint","IMPRINT",FACE,{"disambiguationData":[TD([[makeQuery(id+"F5.imprint","IMPRINT",EDGE,{"derivedFrom":sQuery(id+"F5.wireOp",EDGE,"E31.5.10.3")}),-1.0]])]});
            var Q57;
            Q57=makeQuery(id+"F5.imprint","IMPRINT",FACE,{"disambiguationData":[TD([[makeQuery(id+"F5.imprint","IMPRINT",EDGE,{"derivedFrom":sQuery(id+"F5.wireOp",EDGE,"E31.6.2.0")}),-1.0]])]});
            var Q58;
            Q58=makeQuery(id+"F5.imprint","IMPRINT",FACE,{"disambiguationData":[TD([[makeQuery(id+"F5.imprint","IMPRINT",EDGE,{"derivedFrom":sQuery(id+"F5.wireOp",EDGE,"E31.7.1.3")}),-1.0]])]});
            var Q59;
            Q59=makeQuery(id+"F5.imprint","IMPRINT",FACE,{"disambiguationData":[TD([[makeQuery(id+"F5.imprint","IMPRINT",EDGE,{"derivedFrom":sQuery(id+"F5.wireOp",EDGE,"E31.6.10.0")}),-1.0]])]});
            var Q60;
            Q60=makeQuery(id+"F5.imprint","IMPRINT",FACE,{"disambiguationData":[TD([[makeQuery(id+"F5.imprint","IMPRINT",EDGE,{"derivedFrom":sQuery(id+"F5.wireOp",EDGE,"E31.1.12.0")}),-1.0]])]});
            var Q61;
            Q61=makeQuery(id+"F5.imprint","IMPRINT",FACE,{"disambiguationData":[TD([[makeQuery(id+"F5.imprint","IMPRINT",EDGE,{"derivedFrom":sQuery(id+"F5.wireOp",EDGE,"E31.2.3.3")}),-1.0]])]});
            var Q62;
            Q62=makeQuery(id+"F5.imprint","IMPRINT",FACE,{"disambiguationData":[TD([[makeQuery(id+"F5.imprint","IMPRINT",EDGE,{"derivedFrom":sQuery(id+"F5.wireOp",EDGE,"E31.2.11.3")}),-1.0]])]});
            var Q63;
            Q63=makeQuery(id+"F5.imprint","IMPRINT",FACE,{"disambiguationData":[TD([[makeQuery(id+"F5.imprint","IMPRINT",EDGE,{"derivedFrom":sQuery(id+"F5.wireOp",EDGE,"E31.3.3.0")}),-1.0]])]});
            var Q64;
            Q64=makeQuery(id+"F5.imprint","IMPRINT",FACE,{"disambiguationData":[TD([[makeQuery(id+"F5.imprint","IMPRINT",EDGE,{"derivedFrom":sQuery(id+"F5.wireOp",EDGE,"E31.0.12.3")}),-1.0]])]});
            var Q65;
            Q65=makeQuery(id+"F5.imprint","IMPRINT",FACE,{"disambiguationData":[TD([[makeQuery(id+"F5.imprint","IMPRINT",EDGE,{"derivedFrom":sQuery(id+"F5.wireOp",EDGE,"E31.1.4.0")}),-1.0]])]});
            var Q66;
            Q66=makeQuery(id+"F5.imprint","IMPRINT",FACE,{"disambiguationData":[TD([[makeQuery(id+"F5.imprint","IMPRINT",EDGE,{"derivedFrom":sQuery(id+"F5.wireOp",EDGE,"E31.7.9.0")}),-1.0]])]});
            var Q67;
            Q67=makeQuery(id+"F5.imprint","IMPRINT",FACE,{"disambiguationData":[TD([[makeQuery(id+"F5.imprint","IMPRINT",EDGE,{"derivedFrom":sQuery(id+"F5.wireOp",EDGE,"E31.8.8.3")}),-1.0]])]});
            var Q68;
            Q68=makeQuery(id+"F5.imprint","IMPRINT",FACE,{"disambiguationData":[TD([[makeQuery(id+"F5.imprint","IMPRINT",EDGE,{"derivedFrom":sQuery(id+"F5.wireOp",EDGE,"E31.5.10.0")}),-1.0]])]});
            var Q69;
            Q69=makeQuery(id+"F5.imprint","IMPRINT",FACE,{"disambiguationData":[TD([[makeQuery(id+"F5.imprint","IMPRINT",EDGE,{"derivedFrom":sQuery(id+"F5.wireOp",EDGE,"E31.6.1.3")}),-1.0]])]});
            var Q70;
            Q70=makeQuery(id+"F5.imprint","IMPRINT",FACE,{"disambiguationData":[TD([[makeQuery(id+"F5.imprint","IMPRINT",EDGE,{"derivedFrom":sQuery(id+"F5.wireOp",EDGE,"E31.6.9.3")}),-1.0]])]});
            var Q71;
            Q71=makeQuery(id+"F5.imprint","IMPRINT",FACE,{"disambiguationData":[TD([[makeQuery(id+"F5.imprint","IMPRINT",EDGE,{"derivedFrom":sQuery(id+"F5.wireOp",EDGE,"E31.7.1.0")}),-1.0]])]});
            var Q72;
            Q72=makeQuery(id+"F5.imprint","IMPRINT",FACE,{"disambiguationData":[TD([[makeQuery(id+"F5.imprint","IMPRINT",EDGE,{"derivedFrom":sQuery(id+"F5.wireOp",EDGE,"E31.3.11.0")}),-1.0]])]});
            var Q73;
            Q73=makeQuery(id+"F5.imprint","IMPRINT",FACE,{"disambiguationData":[TD([[makeQuery(id+"F5.imprint","IMPRINT",EDGE,{"derivedFrom":sQuery(id+"F5.wireOp",EDGE,"E31.4.2.3")}),-1.0]])]});
            var Q74;
            Q74=makeQuery(id+"F5.imprint","IMPRINT",FACE,{"disambiguationData":[TD([[makeQuery(id+"F5.imprint","IMPRINT",EDGE,{"derivedFrom":sQuery(id+"F5.wireOp",EDGE,"E31.4.10.3")}),-1.0]])]});
            var Q75;
            Q75=makeQuery(id+"F5.imprint","IMPRINT",FACE,{"disambiguationData":[TD([[makeQuery(id+"F5.imprint","IMPRINT",EDGE,{"derivedFrom":sQuery(id+"F5.wireOp",EDGE,"E31.5.2.0")}),-1.0]])]});
            var Q76;
            Q76=makeQuery(id+"F5.imprint","IMPRINT",FACE,{"disambiguationData":[TD([[makeQuery(id+"F5.imprint","IMPRINT",EDGE,{"derivedFrom":sQuery(id+"F5.wireOp",EDGE,"E31.1.3.3")}),-1.0]])]});
            var Q77;
            Q77=makeQuery(id+"F5.imprint","IMPRINT",FACE,{"disambiguationData":[TD([[makeQuery(id+"F5.imprint","IMPRINT",EDGE,{"derivedFrom":sQuery(id+"F5.wireOp",EDGE,"E31.0.12.0")}),-1.0]])]});
            var Q78;
            Q78=makeQuery(id+"F5.imprint","IMPRINT",FACE,{"disambiguationData":[TD([[makeQuery(id+"F5.imprint","IMPRINT",EDGE,{"derivedFrom":sQuery(id+"F5.wireOp",EDGE,"E31.9.15.0")}),-1.0]])]});
            var Q79;
            Q79=makeQuery(id+"F5.imprint","IMPRINT",FACE,{"disambiguationData":[TD([[makeQuery(id+"F5.imprint","IMPRINT",EDGE,{"derivedFrom":sQuery(id+"F5.wireOp",EDGE,"E31.7.8.3")}),-1.0]])]});
            var Q80;
            Q80=makeQuery(id+"F5.imprint","IMPRINT",FACE,{"disambiguationData":[TD([[makeQuery(id+"F5.imprint","IMPRINT",EDGE,{"derivedFrom":sQuery(id+"F5.wireOp",EDGE,"E31.8.8.0")}),-1.0]])]});
            var Q81;
            Q81=makeQuery(id+"F5.imprint","IMPRINT",FACE,{"disambiguationData":[TD([[makeQuery(id+"F5.imprint","IMPRINT",EDGE,{"derivedFrom":sQuery(id+"F5.wireOp",EDGE,"E31.8.16.3")}),-1.0]])]});
            var Q82;
            Q82=makeQuery(id+"F5.imprint","IMPRINT",FACE,{"disambiguationData":[TD([[makeQuery(id+"F5.imprint","IMPRINT",EDGE,{"derivedFrom":sQuery(id+"F5.wireOp",EDGE,"E31.6.1.0")}),-1.0]])]});
            var Q83;
            Q83=makeQuery(id+"F5.imprint","IMPRINT",FACE,{"disambiguationData":[TD([[makeQuery(id+"F5.imprint","IMPRINT",EDGE,{"derivedFrom":sQuery(id+"F5.wireOp",EDGE,"E31.5.9.3")}),-1.0]])]});
            var Q84;
            Q84=makeQuery(id+"F5.imprint","IMPRINT",FACE,{"disambiguationData":[TD([[makeQuery(id+"F5.imprint","IMPRINT",EDGE,{"derivedFrom":sQuery(id+"F5.wireOp",EDGE,"E31.6.9.0")}),-1.0]])]});
            var Q85;
            Q85=makeQuery(id+"F5.imprint","IMPRINT",FACE,{"disambiguationData":[TD([[makeQuery(id+"F5.imprint","IMPRINT",EDGE,{"derivedFrom":sQuery(id+"F5.wireOp",EDGE,"E31.7.0.3")}),-1.0]])]});
            var Q86;
            Q86=makeQuery(id+"F5.imprint","IMPRINT",FACE,{"disambiguationData":[TD([[makeQuery(id+"F5.imprint","IMPRINT",EDGE,{"derivedFrom":sQuery(id+"F5.wireOp",EDGE,"E31.3.10.3")}),-1.0]])]});
            var Q87;
            Q87=makeQuery(id+"F5.imprint","IMPRINT",FACE,{"disambiguationData":[TD([[makeQuery(id+"F5.imprint","IMPRINT",EDGE,{"derivedFrom":sQuery(id+"F5.wireOp",EDGE,"E31.4.2.0")}),-1.0]])]});
            var Q88;
            Q88=makeQuery(id+"F5.imprint","IMPRINT",FACE,{"disambiguationData":[TD([[makeQuery(id+"F5.imprint","IMPRINT",EDGE,{"derivedFrom":sQuery(id+"F5.wireOp",EDGE,"E31.4.10.0")}),-1.0]])]});
            var Q89;
            Q89=makeQuery(id+"F5.imprint","IMPRINT",FACE,{"disambiguationData":[TD([[makeQuery(id+"F5.imprint","IMPRINT",EDGE,{"derivedFrom":sQuery(id+"F5.wireOp",EDGE,"E31.5.1.3")}),-1.0]])]});
            var Q90;
            Q90=makeQuery(id+"F5.imprint","IMPRINT",FACE,{"disambiguationData":[TD([[makeQuery(id+"F5.imprint","IMPRINT",EDGE,{"derivedFrom":sQuery(id+"F5.wireOp",EDGE,"E31.1.11.3")}),-1.0]])]});
            var Q91;
            Q91=makeQuery(id+"F5.imprint","IMPRINT",FACE,{"disambiguationData":[TD([[makeQuery(id+"F5.imprint","IMPRINT",EDGE,{"derivedFrom":sQuery(id+"F5.wireOp",EDGE,"E31.2.11.0")}),-1.0]])]});
            var Q92;
            Q92=makeQuery(id+"F5.imprint","IMPRINT",FACE,{"disambiguationData":[TD([[makeQuery(id+"F5.imprint","IMPRINT",EDGE,{"derivedFrom":sQuery(id+"F5.wireOp",EDGE,"E31.2.3.0")}),-1.0]])]});
            var Q93;
            Q93=makeQuery(id+"F5.imprint","IMPRINT",FACE,{"disambiguationData":[TD([[makeQuery(id+"F5.imprint","IMPRINT",EDGE,{"derivedFrom":sQuery(id+"F5.wireOp",EDGE,"E31.9.14.0")}),-1.0]])]});
            var Q94;
            Q94=makeQuery(id+"F5.imprint","IMPRINT",FACE,{"disambiguationData":[TD([[makeQuery(id+"F5.imprint","IMPRINT",EDGE,{"derivedFrom":sQuery(id+"F5.wireOp",EDGE,"E31.3.2.3")}),-1.0]])]});
            var Q95;
            Q95=makeQuery(id+"F5.imprint","IMPRINT",FACE,{"disambiguationData":[TD([[makeQuery(id+"F5.imprint","IMPRINT",EDGE,{"derivedFrom":sQuery(id+"F5.wireOp",EDGE,"E31.7.8.0")}),-1.0]])]});
            var Q96;
            Q96=makeQuery(id+"F5.imprint","IMPRINT",FACE,{"disambiguationData":[TD([[makeQuery(id+"F5.imprint","IMPRINT",EDGE,{"derivedFrom":sQuery(id+"F5.wireOp",EDGE,"E31.7.16.3")}),-1.0]])]});
            var Q97;
            Q97=makeQuery(id+"F5.imprint","IMPRINT",FACE,{"disambiguationData":[TD([[makeQuery(id+"F5.imprint","IMPRINT",EDGE,{"derivedFrom":sQuery(id+"F5.wireOp",EDGE,"E31.8.7.3")}),-1.0]])]});
            var Q98;
            Q98=makeQuery(id+"F5.imprint","IMPRINT",FACE,{"disambiguationData":[TD([[makeQuery(id+"F5.imprint","IMPRINT",EDGE,{"derivedFrom":sQuery(id+"F5.wireOp",EDGE,"E31.1.10.3")}),-1.0]])]});
            var Q99;
            Q99=makeQuery(id+"F5.imprint","IMPRINT",FACE,{"disambiguationData":[TD([[makeQuery(id+"F5.imprint","IMPRINT",EDGE,{"derivedFrom":sQuery(id+"F5.wireOp",EDGE,"E31.2.10.0")}),-1.0]])]});
            var Q100;
            Q100=makeQuery(id+"F5.imprint","IMPRINT",FACE,{"disambiguationData":[TD([[makeQuery(id+"F5.imprint","IMPRINT",EDGE,{"derivedFrom":sQuery(id+"F5.wireOp",EDGE,"E31.2.2.0")}),-1.0]])]});
            var Q101;
            Q101=makeQuery(id+"F5.imprint","IMPRINT",FACE,{"disambiguationData":[TD([[makeQuery(id+"F5.imprint","IMPRINT",EDGE,{"derivedFrom":sQuery(id+"F5.wireOp",EDGE,"E31.5.0.3")}),-1.0]])]});
            var Q102;
            Q102=makeQuery(id+"F5.imprint","IMPRINT",FACE,{"disambiguationData":[TD([[makeQuery(id+"F5.imprint","IMPRINT",EDGE,{"derivedFrom":sQuery(id+"F5.wireOp",EDGE,"E31.4.1.0")}),-1.0]])]});
            var Q103;
            Q103=makeQuery(id+"F5.imprint","IMPRINT",FACE,{"disambiguationData":[TD([[makeQuery(id+"F5.imprint","IMPRINT",EDGE,{"derivedFrom":sQuery(id+"F5.wireOp",EDGE,"E31.4.9.0")}),-1.0]])]});
            var Q104;
            Q104=makeQuery(id+"F5.imprint","IMPRINT",FACE,{"disambiguationData":[TD([[makeQuery(id+"F5.imprint","IMPRINT",EDGE,{"derivedFrom":sQuery(id+"F5.wireOp",EDGE,"E31.3.9.3")}),-1.0]])]});
            var Q105;
            Q105=makeQuery(id+"F5.imprint","IMPRINT",FACE,{"disambiguationData":[TD([[makeQuery(id+"F5.imprint","IMPRINT",EDGE,{"derivedFrom":sQuery(id+"F5.wireOp",EDGE,"E31.6.16.3")}),-1.0]])]});
            var Q106;
            Q106=makeQuery(id+"F5.imprint","IMPRINT",FACE,{"disambiguationData":[TD([[makeQuery(id+"F5.imprint","IMPRINT",EDGE,{"derivedFrom":sQuery(id+"F5.wireOp",EDGE,"E31.6.8.0")}),-1.0]])]});
            var Q107;
            Q107=makeQuery(id+"F5.imprint","IMPRINT",FACE,{"disambiguationData":[TD([[makeQuery(id+"F5.imprint","IMPRINT",EDGE,{"derivedFrom":sQuery(id+"F5.wireOp",EDGE,"E31.6.0.0")}),-1.0]])]});
            var Q108;
            Q108=makeQuery(id+"F5.imprint","IMPRINT",FACE,{"disambiguationData":[TD([[makeQuery(id+"F5.imprint","IMPRINT",EDGE,{"derivedFrom":sQuery(id+"F5.wireOp",EDGE,"E31.5.8.3")}),-1.0]])]});
            var Q109;
            Q109=makeQuery(id+"F5.imprint","IMPRINT",FACE,{"disambiguationData":[TD([[makeQuery(id+"F5.imprint","IMPRINT",EDGE,{"derivedFrom":sQuery(id+"F5.wireOp",EDGE,"E31.8.15.0")}),-1.0]])]});
            var Q110;
            Q110=makeQuery(id+"F5.imprint","IMPRINT",FACE,{"disambiguationData":[TD([[makeQuery(id+"F5.imprint","IMPRINT",EDGE,{"derivedFrom":sQuery(id+"F5.wireOp",EDGE,"E31.8.7.0")}),-1.0]])]});
            var Q111;
            Q111=makeQuery(id+"F5.imprint","IMPRINT",FACE,{"disambiguationData":[TD([[makeQuery(id+"F5.imprint","IMPRINT",EDGE,{"derivedFrom":sQuery(id+"F5.wireOp",EDGE,"E31.7.15.3")}),-1.0]])]});
            var Q112;
            Q112=makeQuery(id+"F5.imprint","IMPRINT",FACE,{"disambiguationData":[TD([[makeQuery(id+"F5.imprint","IMPRINT",EDGE,{"derivedFrom":sQuery(id+"F5.wireOp",EDGE,"E31.7.7.3")}),-1.0]])]});
            var Q113;
            Q113=makeQuery(id+"F5.imprint","IMPRINT",FACE,{"disambiguationData":[TD([[makeQuery(id+"F5.imprint","IMPRINT",EDGE,{"derivedFrom":sQuery(id+"F5.wireOp",EDGE,"E31.9.13.0")}),-1.0]])]});
            var Q114;
            Q114=makeQuery(id+"F5.imprint","IMPRINT",FACE,{"disambiguationData":[TD([[makeQuery(id+"F5.imprint","IMPRINT",EDGE,{"derivedFrom":sQuery(id+"F5.wireOp",EDGE,"E31.1.3.0")}),-1.0]])]});
            var Q115;
            Q115=makeQuery(id+"F5.imprint","IMPRINT",FACE,{"disambiguationData":[TD([[makeQuery(id+"F5.imprint","IMPRINT",EDGE,{"derivedFrom":sQuery(id+"F5.wireOp",EDGE,"E31.0.11.3")}),-1.0]])]});
            var Q116;
            Q116=makeQuery(id+"F5.imprint","IMPRINT",FACE,{"disambiguationData":[TD([[makeQuery(id+"F5.imprint","IMPRINT",EDGE,{"derivedFrom":sQuery(id+"F5.wireOp",EDGE,"E31.2.2.3")}),-1.0]])]});
            var Q117;
            Q117=makeQuery(id+"F5.imprint","IMPRINT",FACE,{"disambiguationData":[TD([[makeQuery(id+"F5.imprint","IMPRINT",EDGE,{"derivedFrom":sQuery(id+"F5.wireOp",EDGE,"E31.3.2.0")}),-1.0]])]});
            var Q118;
            Q118=makeQuery(id+"F5.imprint","IMPRINT",FACE,{"disambiguationData":[TD([[makeQuery(id+"F5.imprint","IMPRINT",EDGE,{"derivedFrom":sQuery(id+"F5.wireOp",EDGE,"E31.2.10.3")}),-1.0]])]});
            var Q119;
            Q119=makeQuery(id+"F5.imprint","IMPRINT",FACE,{"disambiguationData":[TD([[makeQuery(id+"F5.imprint","IMPRINT",EDGE,{"derivedFrom":sQuery(id+"F5.wireOp",EDGE,"E31.1.11.0")}),-1.0]])]});
            var Q120;
            Q120=makeQuery(id+"F5.imprint","IMPRINT",FACE,{"disambiguationData":[TD([[makeQuery(id+"F5.imprint","IMPRINT",EDGE,{"derivedFrom":sQuery(id+"F5.wireOp",EDGE,"E31.5.1.0")}),-1.0]])]});
            var Q121;
            Q121=makeQuery(id+"F5.imprint","IMPRINT",FACE,{"disambiguationData":[TD([[makeQuery(id+"F5.imprint","IMPRINT",EDGE,{"derivedFrom":sQuery(id+"F5.wireOp",EDGE,"E31.4.1.3")}),-1.0]])]});
            var Q122;
            Q122=makeQuery(id+"F5.imprint","IMPRINT",FACE,{"disambiguationData":[TD([[makeQuery(id+"F5.imprint","IMPRINT",EDGE,{"derivedFrom":sQuery(id+"F5.wireOp",EDGE,"E31.4.9.3")}),-1.0]])]});
            var Q123;
            Q123=makeQuery(id+"F5.imprint","IMPRINT",FACE,{"disambiguationData":[TD([[makeQuery(id+"F5.imprint","IMPRINT",EDGE,{"derivedFrom":sQuery(id+"F5.wireOp",EDGE,"E31.3.10.0")}),-1.0]])]});
            var Q124;
            Q124=makeQuery(id+"F5.imprint","IMPRINT",FACE,{"disambiguationData":[TD([[makeQuery(id+"F5.imprint","IMPRINT",EDGE,{"derivedFrom":sQuery(id+"F5.wireOp",EDGE,"E31.6.0.3")}),-1.0]])]});
            var Q125;
            Q125=makeQuery(id+"F5.imprint","IMPRINT",FACE,{"disambiguationData":[TD([[makeQuery(id+"F5.imprint","IMPRINT",EDGE,{"derivedFrom":sQuery(id+"F5.wireOp",EDGE,"E31.5.9.0")}),-1.0]])]});
            var Q126;
            Q126=makeQuery(id+"F5.imprint","IMPRINT",FACE,{"disambiguationData":[TD([[makeQuery(id+"F5.imprint","IMPRINT",EDGE,{"derivedFrom":sQuery(id+"F5.wireOp",EDGE,"E31.7.0.0")}),-1.0]])]});
            var Q127;
            Q127=makeQuery(id+"F5.imprint","IMPRINT",FACE,{"disambiguationData":[TD([[makeQuery(id+"F5.imprint","IMPRINT",EDGE,{"derivedFrom":sQuery(id+"F5.wireOp",EDGE,"E31.6.8.3")}),-1.0]])]});
            var Q128;
            Q128=makeQuery(id+"F5.imprint","IMPRINT",FACE,{"disambiguationData":[TD([[makeQuery(id+"F5.imprint","IMPRINT",EDGE,{"derivedFrom":sQuery(id+"F5.wireOp",EDGE,"E31.8.15.3")}),-1.0]])]});
            var Q129;
            Q129=makeQuery(id+"F5.imprint","IMPRINT",FACE,{"disambiguationData":[TD([[makeQuery(id+"F5.imprint","IMPRINT",EDGE,{"derivedFrom":sQuery(id+"F5.wireOp",EDGE,"E31.8.6.3")}),-1.0]])]});
            var Q130;
            Q130=makeQuery(id+"F5.imprint","IMPRINT",FACE,{"disambiguationData":[TD([[makeQuery(id+"F5.imprint","IMPRINT",EDGE,{"derivedFrom":sQuery(id+"F5.wireOp",EDGE,"E31.8.14.3")}),-1.0]])]});
            var Q131;
            Q131=makeQuery(id+"F5.imprint","IMPRINT",FACE,{"disambiguationData":[TD([[makeQuery(id+"F5.imprint","IMPRINT",EDGE,{"derivedFrom":sQuery(id+"F5.wireOp",EDGE,"E31.9.12.0")}),-1.0]])]});
            var Q132;
            Q132=makeQuery(id+"F5.imprint","IMPRINT",FACE,{"disambiguationData":[TD([[makeQuery(id+"F5.imprint","IMPRINT",EDGE,{"derivedFrom":sQuery(id+"F5.wireOp",EDGE,"E31.6.7.3")}),-1.0]])]});
            var Q133;
            Q133=makeQuery(id+"F5.imprint","IMPRINT",FACE,{"disambiguationData":[TD([[makeQuery(id+"F5.imprint","IMPRINT",EDGE,{"derivedFrom":sQuery(id+"F5.wireOp",EDGE,"E31.6.15.3")}),-1.0]])]});
            var Q134;
            Q134=makeQuery(id+"F5.imprint","IMPRINT",FACE,{"disambiguationData":[TD([[makeQuery(id+"F5.imprint","IMPRINT",EDGE,{"derivedFrom":sQuery(id+"F5.wireOp",EDGE,"E31.7.7.0")}),-1.0]])]});
            var Q135;
            Q135=makeQuery(id+"F5.imprint","IMPRINT",FACE,{"disambiguationData":[TD([[makeQuery(id+"F5.imprint","IMPRINT",EDGE,{"derivedFrom":sQuery(id+"F5.wireOp",EDGE,"E31.7.15.0")}),-1.0]])]});
            var Q136;
            Q136=makeQuery(id+"F5.imprint","IMPRINT",FACE,{"disambiguationData":[TD([[makeQuery(id+"F5.imprint","IMPRINT",EDGE,{"derivedFrom":sQuery(id+"F5.wireOp",EDGE,"E31.5.0.0")}),-1.0]])]});
            var Q137;
            Q137=makeQuery(id+"F5.imprint","IMPRINT",FACE,{"disambiguationData":[TD([[makeQuery(id+"F5.imprint","IMPRINT",EDGE,{"derivedFrom":sQuery(id+"F5.wireOp",EDGE,"E31.5.8.0")}),-1.0]])]});
            var Q138;
            Q138=makeQuery(id+"F5.imprint","IMPRINT",FACE,{"disambiguationData":[TD([[makeQuery(id+"F5.imprint","IMPRINT",EDGE,{"derivedFrom":sQuery(id+"F5.wireOp",EDGE,"E31.5.16.3")}),-1.0]])]});
            var Q139;
            Q139=makeQuery(id+"F5.imprint","IMPRINT",FACE,{"disambiguationData":[TD([[makeQuery(id+"F5.imprint","IMPRINT",EDGE,{"derivedFrom":sQuery(id+"F5.wireOp",EDGE,"E31.2.9.3")}),-1.0]])]});
            var Q140;
            Q140=makeQuery(id+"F5.imprint","IMPRINT",FACE,{"disambiguationData":[TD([[makeQuery(id+"F5.imprint","IMPRINT",EDGE,{"derivedFrom":sQuery(id+"F5.wireOp",EDGE,"E31.3.1.0")}),-1.0]])]});
            var Q141;
            Q141=makeQuery(id+"F5.imprint","IMPRINT",FACE,{"disambiguationData":[TD([[makeQuery(id+"F5.imprint","IMPRINT",EDGE,{"derivedFrom":sQuery(id+"F5.wireOp",EDGE,"E31.4.0.3")}),-1.0]])]});
            var Q142;
            Q142=makeQuery(id+"F5.imprint","IMPRINT",FACE,{"disambiguationData":[TD([[makeQuery(id+"F5.imprint","IMPRINT",EDGE,{"derivedFrom":sQuery(id+"F5.wireOp",EDGE,"E31.3.9.0")}),-1.0]])]});
            var Q143;
            Q143=makeQuery(id+"F5.imprint","IMPRINT",FACE,{"disambiguationData":[TD([[makeQuery(id+"F5.imprint","IMPRINT",EDGE,{"derivedFrom":sQuery(id+"F5.wireOp",EDGE,"E31.0.10.3")}),-1.0]])]});
            var Q144;
            Q144=makeQuery(id+"F5.imprint","IMPRINT",FACE,{"disambiguationData":[TD([[makeQuery(id+"F5.imprint","IMPRINT",EDGE,{"derivedFrom":sQuery(id+"F5.wireOp",EDGE,"E31.1.2.0")}),-1.0]])]});
            var Q145;
            Q145=makeQuery(id+"F5.imprint","IMPRINT",FACE,{"disambiguationData":[TD([[makeQuery(id+"F5.imprint","IMPRINT",EDGE,{"derivedFrom":sQuery(id+"F5.wireOp",EDGE,"E31.1.10.0")}),-1.0]])]});
            var Q146;
            Q146=makeQuery(id+"F5.imprint","IMPRINT",FACE,{"disambiguationData":[TD([[makeQuery(id+"F5.imprint","IMPRINT",EDGE,{"derivedFrom":sQuery(id+"F5.wireOp",EDGE,"E31.2.1.3")}),-1.0]])]});
            var Q147;
            Q147=makeQuery(id+"F5.imprint","IMPRINT",FACE,{"disambiguationData":[TD([[makeQuery(id+"F5.imprint","IMPRINT",EDGE,{"derivedFrom":sQuery(id+"F5.wireOp",EDGE,"E31.8.6.0")}),-1.0]])]});
            var Q148;
            Q148=makeQuery(id+"F5.imprint","IMPRINT",FACE,{"disambiguationData":[TD([[makeQuery(id+"F5.imprint","IMPRINT",EDGE,{"derivedFrom":sQuery(id+"F5.wireOp",EDGE,"E31.8.14.0")}),-1.0]])]});
            var Q149;
            Q149=makeQuery(id+"F5.imprint","IMPRINT",FACE,{"disambiguationData":[TD([[makeQuery(id+"F5.imprint","IMPRINT",EDGE,{"derivedFrom":sQuery(id+"F5.wireOp",EDGE,"E31.9.11.0")}),-1.0]])]});
            var Q150;
            Q150=makeQuery(id+"F5.imprint","IMPRINT",FACE,{"disambiguationData":[TD([[makeQuery(id+"F5.imprint","IMPRINT",EDGE,{"derivedFrom":sQuery(id+"F5.wireOp",EDGE,"E31.6.7.0")}),-1.0]])]});
            var Q151;
            Q151=makeQuery(id+"F5.imprint","IMPRINT",FACE,{"disambiguationData":[TD([[makeQuery(id+"F5.imprint","IMPRINT",EDGE,{"derivedFrom":sQuery(id+"F5.wireOp",EDGE,"E31.6.15.0")}),-1.0]])]});
            var Q152;
            Q152=makeQuery(id+"F5.imprint","IMPRINT",FACE,{"disambiguationData":[TD([[makeQuery(id+"F5.imprint","IMPRINT",EDGE,{"derivedFrom":sQuery(id+"F5.wireOp",EDGE,"E31.7.6.3")}),-1.0]])]});
            var Q153;
            Q153=makeQuery(id+"F5.imprint","IMPRINT",FACE,{"disambiguationData":[TD([[makeQuery(id+"F5.imprint","IMPRINT",EDGE,{"derivedFrom":sQuery(id+"F5.wireOp",EDGE,"E31.7.14.3")}),-1.0]])]});
            var Q154;
            Q154=makeQuery(id+"F5.imprint","IMPRINT",FACE,{"disambiguationData":[TD([[makeQuery(id+"F5.imprint","IMPRINT",EDGE,{"derivedFrom":sQuery(id+"F5.wireOp",EDGE,"E31.4.8.0")}),-1.0]])]});
            var Q155;
            Q155=makeQuery(id+"F5.imprint","IMPRINT",FACE,{"disambiguationData":[TD([[makeQuery(id+"F5.imprint","IMPRINT",EDGE,{"derivedFrom":sQuery(id+"F5.wireOp",EDGE,"E31.4.16.3")}),-1.0]])]});
            var Q156;
            Q156=makeQuery(id+"F5.imprint","IMPRINT",FACE,{"disambiguationData":[TD([[makeQuery(id+"F5.imprint","IMPRINT",EDGE,{"derivedFrom":sQuery(id+"F5.wireOp",EDGE,"E31.2.9.0")}),-1.0]])]});
            var Q157;
            Q157=makeQuery(id+"F5.imprint","IMPRINT",FACE,{"disambiguationData":[TD([[makeQuery(id+"F5.imprint","IMPRINT",EDGE,{"derivedFrom":sQuery(id+"F5.wireOp",EDGE,"E31.5.7.3")}),-1.0]])]});
            var Q158;
            Q158=makeQuery(id+"F5.imprint","IMPRINT",FACE,{"disambiguationData":[TD([[makeQuery(id+"F5.imprint","IMPRINT",EDGE,{"derivedFrom":sQuery(id+"F5.wireOp",EDGE,"E31.3.0.3")}),-1.0]])]});
            var Q159;
            Q159=makeQuery(id+"F5.imprint","IMPRINT",FACE,{"disambiguationData":[TD([[makeQuery(id+"F5.imprint","IMPRINT",EDGE,{"derivedFrom":sQuery(id+"F5.wireOp",EDGE,"E31.5.15.3")}),-1.0]])]});
            var Q160;
            Q160=makeQuery(id+"F5.imprint","IMPRINT",FACE,{"disambiguationData":[TD([[makeQuery(id+"F5.imprint","IMPRINT",EDGE,{"derivedFrom":sQuery(id+"F5.wireOp",EDGE,"E31.3.8.3")}),-1.0]])]});
            var Q161;
            Q161=makeQuery(id+"F5.imprint","IMPRINT",FACE,{"disambiguationData":[TD([[makeQuery(id+"F5.imprint","IMPRINT",EDGE,{"derivedFrom":sQuery(id+"F5.wireOp",EDGE,"E31.4.0.0")}),-1.0]])]});
            var Q162;
            Q162=makeQuery(id+"F5.imprint","IMPRINT",FACE,{"disambiguationData":[TD([[makeQuery(id+"F5.imprint","IMPRINT",EDGE,{"derivedFrom":sQuery(id+"F5.wireOp",EDGE,"E31.0.10.0")}),-1.0]])]});
            var Q163;
            Q163=makeQuery(id+"F5.imprint","IMPRINT",FACE,{"disambiguationData":[TD([[makeQuery(id+"F5.imprint","IMPRINT",EDGE,{"derivedFrom":sQuery(id+"F5.wireOp",EDGE,"E31.1.1.3")}),-1.0]])]});
            var Q164;
            Q164=makeQuery(id+"F5.imprint","IMPRINT",FACE,{"disambiguationData":[TD([[makeQuery(id+"F5.imprint","IMPRINT",EDGE,{"derivedFrom":sQuery(id+"F5.wireOp",EDGE,"E31.2.1.0")}),-1.0]])]});
            var Q165;
            Q165=makeQuery(id+"F5.imprint","IMPRINT",FACE,{"disambiguationData":[TD([[makeQuery(id+"F5.imprint","IMPRINT",EDGE,{"derivedFrom":sQuery(id+"F5.wireOp",EDGE,"E31.1.9.3")}),-1.0]])]});
            var Q166;
            Q166=makeQuery(id+"F5.imprint","IMPRINT",FACE,{"disambiguationData":[TD([[makeQuery(id+"F5.imprint","IMPRINT",EDGE,{"derivedFrom":sQuery(id+"F5.wireOp",EDGE,"E31.8.5.3")}),-1.0]])]});
            var Q167;
            Q167=makeQuery(id+"F5.imprint","IMPRINT",FACE,{"disambiguationData":[TD([[makeQuery(id+"F5.imprint","IMPRINT",EDGE,{"derivedFrom":sQuery(id+"F5.wireOp",EDGE,"E31.8.13.3")}),-1.0]])]});
            var Q168;
            Q168=makeQuery(id+"F5.imprint","IMPRINT",FACE,{"disambiguationData":[TD([[makeQuery(id+"F5.imprint","IMPRINT",EDGE,{"derivedFrom":sQuery(id+"F5.wireOp",EDGE,"E31.9.10.0")}),-1.0]])]});
            var Q169;
            Q169=makeQuery(id+"F5.imprint","IMPRINT",FACE,{"disambiguationData":[TD([[makeQuery(id+"F5.imprint","IMPRINT",EDGE,{"derivedFrom":sQuery(id+"F5.wireOp",EDGE,"E31.6.14.3")}),-1.0]])]});
            var Q170;
            Q170=makeQuery(id+"F5.imprint","IMPRINT",FACE,{"disambiguationData":[TD([[makeQuery(id+"F5.imprint","IMPRINT",EDGE,{"derivedFrom":sQuery(id+"F5.wireOp",EDGE,"E31.6.6.3")}),-1.0]])]});
            var Q171;
            Q171=makeQuery(id+"F5.imprint","IMPRINT",FACE,{"disambiguationData":[TD([[makeQuery(id+"F5.imprint","IMPRINT",EDGE,{"derivedFrom":sQuery(id+"F5.wireOp",EDGE,"E31.7.6.0")}),-1.0]])]});
            var Q172;
            Q172=makeQuery(id+"F5.imprint","IMPRINT",FACE,{"disambiguationData":[TD([[makeQuery(id+"F5.imprint","IMPRINT",EDGE,{"derivedFrom":sQuery(id+"F5.wireOp",EDGE,"E31.7.14.0")}),-1.0]])]});
            var Q173;
            Q173=makeQuery(id+"F5.imprint","IMPRINT",FACE,{"disambiguationData":[TD([[makeQuery(id+"F5.imprint","IMPRINT",EDGE,{"derivedFrom":sQuery(id+"F5.wireOp",EDGE,"E31.4.7.3")}),-1.0]])]});
            var Q174;
            Q174=makeQuery(id+"F5.imprint","IMPRINT",FACE,{"disambiguationData":[TD([[makeQuery(id+"F5.imprint","IMPRINT",EDGE,{"derivedFrom":sQuery(id+"F5.wireOp",EDGE,"E31.4.15.3")}),-1.0]])]});
            var Q175;
            Q175=makeQuery(id+"F5.imprint","IMPRINT",FACE,{"disambiguationData":[TD([[makeQuery(id+"F5.imprint","IMPRINT",EDGE,{"derivedFrom":sQuery(id+"F5.wireOp",EDGE,"E31.5.15.0")}),-1.0]])]});
            var Q176;
            Q176=makeQuery(id+"F5.imprint","IMPRINT",FACE,{"disambiguationData":[TD([[makeQuery(id+"F5.imprint","IMPRINT",EDGE,{"derivedFrom":sQuery(id+"F5.wireOp",EDGE,"E31.5.7.0")}),-1.0]])]});
            var Q177;
            Q177=makeQuery(id+"F5.imprint","IMPRINT",FACE,{"disambiguationData":[TD([[makeQuery(id+"F5.imprint","IMPRINT",EDGE,{"derivedFrom":sQuery(id+"F5.wireOp",EDGE,"E31.2.8.3")}),-1.0]])]});
            var Q178;
            Q178=makeQuery(id+"F5.imprint","IMPRINT",FACE,{"disambiguationData":[TD([[makeQuery(id+"F5.imprint","IMPRINT",EDGE,{"derivedFrom":sQuery(id+"F5.wireOp",EDGE,"E31.3.8.0")}),-1.0]])]});
            var Q179;
            Q179=makeQuery(id+"F5.imprint","IMPRINT",FACE,{"disambiguationData":[TD([[makeQuery(id+"F5.imprint","IMPRINT",EDGE,{"derivedFrom":sQuery(id+"F5.wireOp",EDGE,"E31.3.0.0")}),-1.0]])]});
            var Q180;
            Q180=makeQuery(id+"F5.imprint","IMPRINT",FACE,{"disambiguationData":[TD([[makeQuery(id+"F5.imprint","IMPRINT",EDGE,{"derivedFrom":sQuery(id+"F5.wireOp",EDGE,"E31.3.16.3")}),-1.0]])]});
            var Q181;
            Q181=makeQuery(id+"F5.imprint","IMPRINT",FACE,{"disambiguationData":[TD([[makeQuery(id+"F5.imprint","IMPRINT",EDGE,{"derivedFrom":sQuery(id+"F5.wireOp",EDGE,"E31.0.9.3")}),-1.0]])]});
            var Q182;
            Q182=makeQuery(id+"F5.imprint","IMPRINT",FACE,{"disambiguationData":[TD([[makeQuery(id+"F5.imprint","IMPRINT",EDGE,{"derivedFrom":sQuery(id+"F5.wireOp",EDGE,"E31.1.1.0")}),-1.0]])]});
            var Q183;
            Q183=makeQuery(id+"F5.imprint","IMPRINT",FACE,{"disambiguationData":[TD([[makeQuery(id+"F5.imprint","IMPRINT",EDGE,{"derivedFrom":sQuery(id+"F5.wireOp",EDGE,"E31.1.9.0")}),-1.0]])]});
            var Q184;
            Q184=makeQuery(id+"F5.imprint","IMPRINT",FACE,{"disambiguationData":[TD([[makeQuery(id+"F5.imprint","IMPRINT",EDGE,{"derivedFrom":sQuery(id+"F5.wireOp",EDGE,"E31.2.0.3")}),-1.0]])]});
            var Q185;
            Q185=makeQuery(id+"F5.imprint","IMPRINT",FACE,{"disambiguationData":[TD([[makeQuery(id+"F5.imprint","IMPRINT",EDGE,{"derivedFrom":sQuery(id+"F5.wireOp",EDGE,"E31.8.5.0")}),-1.0]])]});
            var Q186;
            Q186=makeQuery(id+"F5.imprint","IMPRINT",FACE,{"disambiguationData":[TD([[makeQuery(id+"F5.imprint","IMPRINT",EDGE,{"derivedFrom":sQuery(id+"F5.wireOp",EDGE,"E31.8.13.0")}),-1.0]])]});
            var Q187;
            Q187=makeQuery(id+"F5.imprint","IMPRINT",FACE,{"disambiguationData":[TD([[makeQuery(id+"F5.imprint","IMPRINT",EDGE,{"derivedFrom":sQuery(id+"F5.wireOp",EDGE,"E31.9.9.0")}),-1.0]])]});
            var Q188;
            Q188=makeQuery(id+"F5.imprint","IMPRINT",FACE,{"disambiguationData":[TD([[makeQuery(id+"F5.imprint","IMPRINT",EDGE,{"derivedFrom":sQuery(id+"F5.wireOp",EDGE,"E31.6.6.0")}),-1.0]])]});
            var Q189;
            Q189=makeQuery(id+"F5.imprint","IMPRINT",FACE,{"disambiguationData":[TD([[makeQuery(id+"F5.imprint","IMPRINT",EDGE,{"derivedFrom":sQuery(id+"F5.wireOp",EDGE,"E31.6.14.0")}),-1.0]])]});
            var Q190;
            Q190=makeQuery(id+"F5.imprint","IMPRINT",FACE,{"disambiguationData":[TD([[makeQuery(id+"F5.imprint","IMPRINT",EDGE,{"derivedFrom":sQuery(id+"F5.wireOp",EDGE,"E31.7.5.3")}),-1.0]])]});
            var Q191;
            Q191=makeQuery(id+"F5.imprint","IMPRINT",FACE,{"disambiguationData":[TD([[makeQuery(id+"F5.imprint","IMPRINT",EDGE,{"derivedFrom":sQuery(id+"F5.wireOp",EDGE,"E31.4.7.0")}),-1.0]])]});
            var Q192;
            Q192=makeQuery(id+"F5.imprint","IMPRINT",FACE,{"disambiguationData":[TD([[makeQuery(id+"F5.imprint","IMPRINT",EDGE,{"derivedFrom":sQuery(id+"F5.wireOp",EDGE,"E31.7.13.3")}),-1.0]])]});
            var Q193;
            Q193=makeQuery(id+"F5.imprint","IMPRINT",FACE,{"disambiguationData":[TD([[makeQuery(id+"F5.imprint","IMPRINT",EDGE,{"derivedFrom":sQuery(id+"F5.wireOp",EDGE,"E31.4.15.0")}),-1.0]])]});
            var Q194;
            Q194=makeQuery(id+"F5.imprint","IMPRINT",FACE,{"disambiguationData":[TD([[makeQuery(id+"F5.imprint","IMPRINT",EDGE,{"derivedFrom":sQuery(id+"F5.wireOp",EDGE,"E31.5.14.3")}),-1.0]])]});
            var Q195;
            Q195=makeQuery(id+"F5.imprint","IMPRINT",FACE,{"disambiguationData":[TD([[makeQuery(id+"F5.imprint","IMPRINT",EDGE,{"derivedFrom":sQuery(id+"F5.wireOp",EDGE,"E31.5.6.3")}),-1.0]])]});
            var Q196;
            Q196=makeQuery(id+"F5.imprint","IMPRINT",FACE,{"disambiguationData":[TD([[makeQuery(id+"F5.imprint","IMPRINT",EDGE,{"derivedFrom":sQuery(id+"F5.wireOp",EDGE,"E31.2.8.0")}),-1.0]])]});
            var Q197;
            Q197=makeQuery(id+"F5.imprint","IMPRINT",FACE,{"disambiguationData":[TD([[makeQuery(id+"F5.imprint","IMPRINT",EDGE,{"derivedFrom":sQuery(id+"F5.wireOp",EDGE,"E31.2.16.3")}),-1.0]])]});
            var Q198;
            Q198=makeQuery(id+"F5.imprint","IMPRINT",FACE,{"disambiguationData":[TD([[makeQuery(id+"F5.imprint","IMPRINT",EDGE,{"derivedFrom":sQuery(id+"F5.wireOp",EDGE,"E31.3.7.3")}),-1.0]])]});
            var Q199;
            Q199=makeQuery(id+"F5.imprint","IMPRINT",FACE,{"disambiguationData":[TD([[makeQuery(id+"F5.imprint","IMPRINT",EDGE,{"derivedFrom":sQuery(id+"F5.wireOp",EDGE,"E31.3.15.3")}),-1.0]])]});
            var Q200;
            Q200=makeQuery(id+"F5.imprint","IMPRINT",FACE,{"disambiguationData":[TD([[makeQuery(id+"F5.imprint","IMPRINT",EDGE,{"derivedFrom":sQuery(id+"F5.wireOp",EDGE,"E31.0.9.0")}),-1.0]])]});
            var Q201;
            Q201=makeQuery(id+"F5.imprint","IMPRINT",FACE,{"disambiguationData":[TD([[makeQuery(id+"F5.imprint","IMPRINT",EDGE,{"derivedFrom":sQuery(id+"F5.wireOp",EDGE,"E31.1.0.3")}),-1.0]])]});
            var Q202;
            Q202=makeQuery(id+"F5.imprint","IMPRINT",FACE,{"disambiguationData":[TD([[makeQuery(id+"F5.imprint","IMPRINT",EDGE,{"derivedFrom":sQuery(id+"F5.wireOp",EDGE,"E31.1.8.3")}),-1.0]])]});
            var Q203;
            Q203=makeQuery(id+"F5.imprint","IMPRINT",FACE,{"disambiguationData":[TD([[makeQuery(id+"F5.imprint","IMPRINT",EDGE,{"derivedFrom":sQuery(id+"F5.wireOp",EDGE,"E31.2.0.0")}),-1.0]])]});
            var Q204;
            Q204=makeQuery(id+"F5.imprint","IMPRINT",FACE,{"disambiguationData":[TD([[makeQuery(id+"F5.imprint","IMPRINT",EDGE,{"derivedFrom":sQuery(id+"F5.wireOp",EDGE,"E31.8.4.3")}),-1.0]])]});
            var Q205;
            Q205=makeQuery(id+"F5.imprint","IMPRINT",FACE,{"disambiguationData":[TD([[makeQuery(id+"F5.imprint","IMPRINT",EDGE,{"derivedFrom":sQuery(id+"F5.wireOp",EDGE,"E31.8.12.3")}),-1.0]])]});
            var Q206;
            Q206=makeQuery(id+"F5.imprint","IMPRINT",FACE,{"disambiguationData":[TD([[makeQuery(id+"F5.imprint","IMPRINT",EDGE,{"derivedFrom":sQuery(id+"F5.wireOp",EDGE,"E31.9.8.0")}),-1.0]])]});
            var Q207;
            Q207=makeQuery(id+"F5.imprint","IMPRINT",FACE,{"disambiguationData":[TD([[makeQuery(id+"F5.imprint","IMPRINT",EDGE,{"derivedFrom":sQuery(id+"F5.wireOp",EDGE,"E31.6.5.3")}),-1.0]])]});
            var Q208;
            Q208=makeQuery(id+"F5.imprint","IMPRINT",FACE,{"disambiguationData":[TD([[makeQuery(id+"F5.imprint","IMPRINT",EDGE,{"derivedFrom":sQuery(id+"F5.wireOp",EDGE,"E31.6.13.3")}),-1.0]])]});
            var Q209;
            Q209=makeQuery(id+"F5.imprint","IMPRINT",FACE,{"disambiguationData":[TD([[makeQuery(id+"F5.imprint","IMPRINT",EDGE,{"derivedFrom":sQuery(id+"F5.wireOp",EDGE,"E31.7.5.0")}),-1.0]])]});
            var Q210;
            Q210=makeQuery(id+"F5.imprint","IMPRINT",FACE,{"disambiguationData":[TD([[makeQuery(id+"F5.imprint","IMPRINT",EDGE,{"derivedFrom":sQuery(id+"F5.wireOp",EDGE,"E31.7.13.0")}),-1.0]])]});
            var Q211;
            Q211=makeQuery(id+"F5.imprint","IMPRINT",FACE,{"disambiguationData":[TD([[makeQuery(id+"F5.imprint","IMPRINT",EDGE,{"derivedFrom":sQuery(id+"F5.wireOp",EDGE,"E31.4.6.3")}),-1.0]])]});
            var Q212;
            Q212=makeQuery(id+"F5.imprint","IMPRINT",FACE,{"disambiguationData":[TD([[makeQuery(id+"F5.imprint","IMPRINT",EDGE,{"derivedFrom":sQuery(id+"F5.wireOp",EDGE,"E31.4.14.3")}),-1.0]])]});
            var Q213;
            Q213=makeQuery(id+"F5.imprint","IMPRINT",FACE,{"disambiguationData":[TD([[makeQuery(id+"F5.imprint","IMPRINT",EDGE,{"derivedFrom":sQuery(id+"F5.wireOp",EDGE,"E31.5.6.0")}),-1.0]])]});
            var Q214;
            Q214=makeQuery(id+"F5.imprint","IMPRINT",FACE,{"disambiguationData":[TD([[makeQuery(id+"F5.imprint","IMPRINT",EDGE,{"derivedFrom":sQuery(id+"F5.wireOp",EDGE,"E31.5.14.0")}),-1.0]])]});
            var Q215;
            Q215=makeQuery(id+"F5.imprint","IMPRINT",FACE,{"disambiguationData":[TD([[makeQuery(id+"F5.imprint","IMPRINT",EDGE,{"derivedFrom":sQuery(id+"F5.wireOp",EDGE,"E31.2.7.3")}),-1.0]])]});
            var Q216;
            Q216=makeQuery(id+"F5.imprint","IMPRINT",FACE,{"disambiguationData":[TD([[makeQuery(id+"F5.imprint","IMPRINT",EDGE,{"derivedFrom":sQuery(id+"F5.wireOp",EDGE,"E31.2.15.3")}),-1.0]])]});
            var Q217;
            Q217=makeQuery(id+"F5.imprint","IMPRINT",FACE,{"disambiguationData":[TD([[makeQuery(id+"F5.imprint","IMPRINT",EDGE,{"derivedFrom":sQuery(id+"F5.wireOp",EDGE,"E31.3.7.0")}),-1.0]])]});
            var Q218;
            Q218=makeQuery(id+"F5.imprint","IMPRINT",FACE,{"disambiguationData":[TD([[makeQuery(id+"F5.imprint","IMPRINT",EDGE,{"derivedFrom":sQuery(id+"F5.wireOp",EDGE,"E31.3.15.0")}),-1.0]])]});
            var Q219;
            Q219=makeQuery(id+"F5.imprint","IMPRINT",FACE,{"disambiguationData":[TD([[makeQuery(id+"F5.imprint","IMPRINT",EDGE,{"derivedFrom":sQuery(id+"F5.wireOp",EDGE,"E31.0.8.3")}),-1.0]])]});
            var Q220;
            Q220=makeQuery(id+"F5.imprint","IMPRINT",FACE,{"disambiguationData":[TD([[makeQuery(id+"F5.imprint","IMPRINT",EDGE,{"derivedFrom":sQuery(id+"F5.wireOp",EDGE,"E31.1.0.0")}),-1.0]])]});
            var Q221;
            Q221=makeQuery(id+"F5.imprint","IMPRINT",FACE,{"disambiguationData":[TD([[makeQuery(id+"F5.imprint","IMPRINT",EDGE,{"derivedFrom":sQuery(id+"F5.wireOp",EDGE,"E31.1.8.0")}),-1.0]])]});
            var Q222;
            Q222=makeQuery(id+"F5.imprint","IMPRINT",FACE,{"disambiguationData":[TD([[makeQuery(id+"F5.imprint","IMPRINT",EDGE,{"derivedFrom":sQuery(id+"F5.wireOp",EDGE,"E31.1.16.3")}),-1.0]])]});
            var Q223;
            Q223=makeQuery(id+"F5.imprint","IMPRINT",FACE,{"disambiguationData":[TD([[makeQuery(id+"F5.imprint","IMPRINT",EDGE,{"derivedFrom":sQuery(id+"F5.wireOp",EDGE,"E31.8.4.0")}),-1.0]])]});
            var Q224;
            Q224=makeQuery(id+"F5.imprint","IMPRINT",FACE,{"disambiguationData":[TD([[makeQuery(id+"F5.imprint","IMPRINT",EDGE,{"derivedFrom":sQuery(id+"F5.wireOp",EDGE,"E31.8.12.0")}),-1.0]])]});
            var Q225;
            Q225=makeQuery(id+"F5.imprint","IMPRINT",FACE,{"disambiguationData":[TD([[makeQuery(id+"F5.imprint","IMPRINT",EDGE,{"derivedFrom":sQuery(id+"F5.wireOp",EDGE,"E31.9.7.0")}),-1.0]])]});
            var Q226;
            Q226=makeQuery(id+"F5.imprint","IMPRINT",FACE,{"disambiguationData":[TD([[makeQuery(id+"F5.imprint","IMPRINT",EDGE,{"derivedFrom":sQuery(id+"F5.wireOp",EDGE,"E31.6.5.0")}),-1.0]])]});
            var Q227;
            Q227=makeQuery(id+"F5.imprint","IMPRINT",FACE,{"disambiguationData":[TD([[makeQuery(id+"F5.imprint","IMPRINT",EDGE,{"derivedFrom":sQuery(id+"F5.wireOp",EDGE,"E31.6.13.0")}),-1.0]])]});
            var Q228;
            Q228=makeQuery(id+"F5.imprint","IMPRINT",FACE,{"disambiguationData":[TD([[makeQuery(id+"F5.imprint","IMPRINT",EDGE,{"derivedFrom":sQuery(id+"F5.wireOp",EDGE,"E31.7.4.3")}),-1.0]])]});
            var Q229;
            Q229=makeQuery(id+"F5.imprint","IMPRINT",FACE,{"disambiguationData":[TD([[makeQuery(id+"F5.imprint","IMPRINT",EDGE,{"derivedFrom":sQuery(id+"F5.wireOp",EDGE,"E31.7.12.3")}),-1.0]])]});
            var Q230;
            Q230=makeQuery(id+"F5.imprint","IMPRINT",FACE,{"disambiguationData":[TD([[makeQuery(id+"F5.imprint","IMPRINT",EDGE,{"derivedFrom":sQuery(id+"F5.wireOp",EDGE,"E31.4.6.0")}),-1.0]])]});
            var Q231;
            Q231=makeQuery(id+"F5.imprint","IMPRINT",FACE,{"disambiguationData":[TD([[makeQuery(id+"F5.imprint","IMPRINT",EDGE,{"derivedFrom":sQuery(id+"F5.wireOp",EDGE,"E31.5.5.3")}),-1.0]])]});
            var Q232;
            Q232=makeQuery(id+"F5.imprint","IMPRINT",FACE,{"disambiguationData":[TD([[makeQuery(id+"F5.imprint","IMPRINT",EDGE,{"derivedFrom":sQuery(id+"F5.wireOp",EDGE,"E31.4.14.0")}),-1.0]])]});
            var Q233;
            Q233=makeQuery(id+"F5.imprint","IMPRINT",FACE,{"disambiguationData":[TD([[makeQuery(id+"F5.imprint","IMPRINT",EDGE,{"derivedFrom":sQuery(id+"F5.wireOp",EDGE,"E31.5.13.3")}),-1.0]])]});
            var Q234;
            Q234=makeQuery(id+"F5.imprint","IMPRINT",FACE,{"disambiguationData":[TD([[makeQuery(id+"F5.imprint","IMPRINT",EDGE,{"derivedFrom":sQuery(id+"F5.wireOp",EDGE,"E31.2.15.0")}),-1.0]])]});
            var Q235;
            Q235=makeQuery(id+"F5.imprint","IMPRINT",FACE,{"disambiguationData":[TD([[makeQuery(id+"F5.imprint","IMPRINT",EDGE,{"derivedFrom":sQuery(id+"F5.wireOp",EDGE,"E31.2.7.0")}),-1.0]])]});
            var Q236;
            Q236=makeQuery(id+"F5.imprint","IMPRINT",FACE,{"disambiguationData":[TD([[makeQuery(id+"F5.imprint","IMPRINT",EDGE,{"derivedFrom":sQuery(id+"F5.wireOp",EDGE,"E31.3.6.3")}),-1.0]])]});
            var Q237;
            Q237=makeQuery(id+"F5.imprint","IMPRINT",FACE,{"disambiguationData":[TD([[makeQuery(id+"F5.imprint","IMPRINT",EDGE,{"derivedFrom":sQuery(id+"F5.wireOp",EDGE,"E31.3.14.3")}),-1.0]])]});
            var Q238;
            Q238=makeQuery(id+"F5.imprint","IMPRINT",FACE,{"disambiguationData":[TD([[makeQuery(id+"F5.imprint","IMPRINT",EDGE,{"derivedFrom":sQuery(id+"F5.wireOp",EDGE,"E31.0.8.0")}),-1.0]])]});
            var Q239;
            Q239=makeQuery(id+"F5.imprint","IMPRINT",FACE,{"disambiguationData":[TD([[makeQuery(id+"F5.imprint","IMPRINT",EDGE,{"derivedFrom":sQuery(id+"F5.wireOp",EDGE,"E31.0.16.3")}),-1.0]])]});
            var Q240;
            Q240=makeQuery(id+"F5.imprint","IMPRINT",FACE,{"disambiguationData":[TD([[makeQuery(id+"F5.imprint","IMPRINT",EDGE,{"derivedFrom":sQuery(id+"F5.wireOp",EDGE,"E31.1.7.3")}),-1.0]])]});
            var Q241;
            Q241=makeQuery(id+"F5.imprint","IMPRINT",FACE,{"disambiguationData":[TD([[makeQuery(id+"F5.imprint","IMPRINT",EDGE,{"derivedFrom":sQuery(id+"F5.wireOp",EDGE,"E31.1.15.3")}),-1.0]])]});
            var Q242;
            Q242=makeQuery(id+"F5.imprint","IMPRINT",FACE,{"disambiguationData":[TD([[makeQuery(id+"F5.imprint","IMPRINT",EDGE,{"derivedFrom":sQuery(id+"F5.wireOp",EDGE,"E31.8.3.0")}),-1.0]])]});
            var Q243;
            Q243=makeQuery(id+"F5.imprint","IMPRINT",FACE,{"disambiguationData":[TD([[makeQuery(id+"F5.imprint","IMPRINT",EDGE,{"derivedFrom":sQuery(id+"F5.wireOp",EDGE,"E31.8.11.0")}),-1.0]])]});
            var Q244;
            Q244=makeQuery(id+"F5.imprint","IMPRINT",FACE,{"disambiguationData":[TD([[makeQuery(id+"F5.imprint","IMPRINT",EDGE,{"derivedFrom":sQuery(id+"F5.wireOp",EDGE,"E31.9.5.0")}),-1.0]])]});
            var Q245;
            Q245=makeQuery(id+"F5.imprint","IMPRINT",FACE,{"disambiguationData":[TD([[makeQuery(id+"F5.imprint","IMPRINT",EDGE,{"derivedFrom":sQuery(id+"F5.wireOp",EDGE,"E31.6.4.0")}),-1.0]])]});
            var Q246;
            Q246=makeQuery(id+"F5.imprint","IMPRINT",FACE,{"disambiguationData":[TD([[makeQuery(id+"F5.imprint","IMPRINT",EDGE,{"derivedFrom":sQuery(id+"F5.wireOp",EDGE,"E31.6.12.0")}),-1.0]])]});
            var Q247;
            Q247=makeQuery(id+"F5.imprint","IMPRINT",FACE,{"disambiguationData":[TD([[makeQuery(id+"F5.imprint","IMPRINT",EDGE,{"derivedFrom":sQuery(id+"F5.wireOp",EDGE,"E31.7.3.3")}),-1.0]])]});
            var Q248;
            Q248=makeQuery(id+"F5.imprint","IMPRINT",FACE,{"disambiguationData":[TD([[makeQuery(id+"F5.imprint","IMPRINT",EDGE,{"derivedFrom":sQuery(id+"F5.wireOp",EDGE,"E31.7.11.3")}),-1.0]])]});
            var Q249;
            Q249=makeQuery(id+"F5.imprint","IMPRINT",FACE,{"disambiguationData":[TD([[makeQuery(id+"F5.imprint","IMPRINT",EDGE,{"derivedFrom":sQuery(id+"F5.wireOp",EDGE,"E31.4.5.0")}),-1.0]])]});
            var Q250;
            Q250=makeQuery(id+"F5.imprint","IMPRINT",FACE,{"disambiguationData":[TD([[makeQuery(id+"F5.imprint","IMPRINT",EDGE,{"derivedFrom":sQuery(id+"F5.wireOp",EDGE,"E31.4.13.0")}),-1.0]])]});
            var Q251;
            Q251=makeQuery(id+"F5.imprint","IMPRINT",FACE,{"disambiguationData":[TD([[makeQuery(id+"F5.imprint","IMPRINT",EDGE,{"derivedFrom":sQuery(id+"F5.wireOp",EDGE,"E31.5.4.3")}),-1.0]])]});
            var Q252;
            Q252=makeQuery(id+"F5.imprint","IMPRINT",FACE,{"disambiguationData":[TD([[makeQuery(id+"F5.imprint","IMPRINT",EDGE,{"derivedFrom":sQuery(id+"F5.wireOp",EDGE,"E31.5.12.3")}),-1.0]])]});
            var Q253;
            Q253=makeQuery(id+"F5.imprint","IMPRINT",FACE,{"disambiguationData":[TD([[makeQuery(id+"F5.imprint","IMPRINT",EDGE,{"derivedFrom":sQuery(id+"F5.wireOp",EDGE,"E31.2.6.0")}),-1.0]])]});
            var Q254;
            Q254=makeQuery(id+"F5.imprint","IMPRINT",FACE,{"disambiguationData":[TD([[makeQuery(id+"F5.imprint","IMPRINT",EDGE,{"derivedFrom":sQuery(id+"F5.wireOp",EDGE,"E31.2.14.0")}),-1.0]])]});
            var Q255;
            Q255=makeQuery(id+"F5.imprint","IMPRINT",FACE,{"disambiguationData":[TD([[makeQuery(id+"F5.imprint","IMPRINT",EDGE,{"derivedFrom":sQuery(id+"F5.wireOp",EDGE,"E31.3.13.3")}),-1.0]])]});
            var Q256;
            Q256=makeQuery(id+"F5.imprint","IMPRINT",FACE,{"disambiguationData":[TD([[makeQuery(id+"F5.imprint","IMPRINT",EDGE,{"derivedFrom":sQuery(id+"F5.wireOp",EDGE,"E31.3.5.3")}),-1.0]])]});
            var Q257;
            Q257=makeQuery(id+"F5.imprint","IMPRINT",FACE,{"disambiguationData":[TD([[makeQuery(id+"F5.imprint","IMPRINT",EDGE,{"derivedFrom":sQuery(id+"F5.wireOp",EDGE,"E31.0.15.0")}),-1.0]])]});
            var Q258;
            Q258=makeQuery(id+"F5.imprint","IMPRINT",FACE,{"disambiguationData":[TD([[makeQuery(id+"F5.imprint","IMPRINT",EDGE,{"derivedFrom":sQuery(id+"F5.wireOp",EDGE,"E31.1.6.3")}),-1.0]])]});
            var Q259;
            Q259=makeQuery(id+"F5.imprint","IMPRINT",FACE,{"disambiguationData":[TD([[makeQuery(id+"F5.imprint","IMPRINT",EDGE,{"derivedFrom":sQuery(id+"F5.wireOp",EDGE,"E31.1.14.3")}),-1.0]])]});
            var Q260;
            Q260=makeQuery(id+"F5.imprint","IMPRINT",FACE,{"disambiguationData":[TD([[makeQuery(id+"F5.imprint","IMPRINT",EDGE,{"derivedFrom":sQuery(id+"F5.wireOp",EDGE,"E31.8.2.3")}),-1.0]])]});
            var Q261;
            Q261=makeQuery(id+"F5.imprint","IMPRINT",FACE,{"disambiguationData":[TD([[makeQuery(id+"F5.imprint","IMPRINT",EDGE,{"derivedFrom":sQuery(id+"F5.wireOp",EDGE,"E31.8.10.3")}),-1.0]])]});
            var Q262;
            Q262=makeQuery(id+"F5.imprint","IMPRINT",FACE,{"disambiguationData":[TD([[makeQuery(id+"F5.imprint","IMPRINT",EDGE,{"derivedFrom":sQuery(id+"F5.wireOp",EDGE,"E31.9.4.0")}),-1.0]])]});
            var Q263;
            Q263=makeQuery(id+"F5.imprint","IMPRINT",FACE,{"disambiguationData":[TD([[makeQuery(id+"F5.imprint","IMPRINT",EDGE,{"derivedFrom":sQuery(id+"F5.wireOp",EDGE,"E31.6.3.3")}),-1.0]])]});
            var Q264;
            Q264=makeQuery(id+"F5.imprint","IMPRINT",FACE,{"disambiguationData":[TD([[makeQuery(id+"F5.imprint","IMPRINT",EDGE,{"derivedFrom":sQuery(id+"F5.wireOp",EDGE,"E31.6.11.3")}),-1.0]])]});
            var Q265;
            Q265=makeQuery(id+"F5.imprint","IMPRINT",FACE,{"disambiguationData":[TD([[makeQuery(id+"F5.imprint","IMPRINT",EDGE,{"derivedFrom":sQuery(id+"F5.wireOp",EDGE,"E31.7.3.0")}),-1.0]])]});
            var Q266;
            Q266=makeQuery(id+"F5.imprint","IMPRINT",FACE,{"disambiguationData":[TD([[makeQuery(id+"F5.imprint","IMPRINT",EDGE,{"derivedFrom":sQuery(id+"F5.wireOp",EDGE,"E31.7.11.0")}),-1.0]])]});
            var Q267;
            Q267=makeQuery(id+"F5.imprint","IMPRINT",FACE,{"disambiguationData":[TD([[makeQuery(id+"F5.imprint","IMPRINT",EDGE,{"derivedFrom":sQuery(id+"F5.wireOp",EDGE,"E31.4.4.3")}),-1.0]])]});
            var Q268;
            Q268=makeQuery(id+"F5.imprint","IMPRINT",FACE,{"disambiguationData":[TD([[makeQuery(id+"F5.imprint","IMPRINT",EDGE,{"derivedFrom":sQuery(id+"F5.wireOp",EDGE,"E31.4.12.3")}),-1.0]])]});
            var Q269;
            Q269=makeQuery(id+"F5.imprint","IMPRINT",FACE,{"disambiguationData":[TD([[makeQuery(id+"F5.imprint","IMPRINT",EDGE,{"derivedFrom":sQuery(id+"F5.wireOp",EDGE,"E31.5.4.0")}),-1.0]])]});
            var Q270;
            Q270=makeQuery(id+"F5.imprint","IMPRINT",FACE,{"disambiguationData":[TD([[makeQuery(id+"F5.imprint","IMPRINT",EDGE,{"derivedFrom":sQuery(id+"F5.wireOp",EDGE,"E31.5.12.0")}),-1.0]])]});
            var Q271;
            Q271=makeQuery(id+"F5.imprint","IMPRINT",FACE,{"disambiguationData":[TD([[makeQuery(id+"F5.imprint","IMPRINT",EDGE,{"derivedFrom":sQuery(id+"F5.wireOp",EDGE,"E31.2.5.3")}),-1.0]])]});
            var Q272;
            Q272=makeQuery(id+"F5.imprint","IMPRINT",FACE,{"disambiguationData":[TD([[makeQuery(id+"F5.imprint","IMPRINT",EDGE,{"derivedFrom":sQuery(id+"F5.wireOp",EDGE,"E31.2.13.3")}),-1.0]])]});
            var Q273;
            Q273=makeQuery(id+"F5.imprint","IMPRINT",FACE,{"disambiguationData":[TD([[makeQuery(id+"F5.imprint","IMPRINT",EDGE,{"derivedFrom":sQuery(id+"F5.wireOp",EDGE,"E31.3.5.0")}),-1.0]])]});
            var Q274;
            Q274=makeQuery(id+"F5.imprint","IMPRINT",FACE,{"disambiguationData":[TD([[makeQuery(id+"F5.imprint","IMPRINT",EDGE,{"derivedFrom":sQuery(id+"F5.wireOp",EDGE,"E31.3.13.0")}),-1.0]])]});
            var Q275;
            Q275=makeQuery(id+"F5.imprint","IMPRINT",FACE,{"disambiguationData":[TD([[makeQuery(id+"F5.imprint","IMPRINT",EDGE,{"derivedFrom":sQuery(id+"F5.wireOp",EDGE,"E31.0.14.3")}),-1.0]])]});
            var Q276;
            Q276=makeQuery(id+"F5.imprint","IMPRINT",FACE,{"disambiguationData":[TD([[makeQuery(id+"F5.imprint","IMPRINT",EDGE,{"derivedFrom":sQuery(id+"F5.wireOp",EDGE,"E31.1.6.0")}),-1.0]])]});
            var Q277;
            Q277=makeQuery(id+"F5.imprint","IMPRINT",FACE,{"disambiguationData":[TD([[makeQuery(id+"F5.imprint","IMPRINT",EDGE,{"derivedFrom":sQuery(id+"F5.wireOp",EDGE,"E31.1.14.0")}),-1.0]])]});
            var Q278;
            Q278=makeQuery(id+"F5.imprint","IMPRINT",FACE,{"disambiguationData":[TD([[makeQuery(id+"F5.imprint","IMPRINT",EDGE,{"derivedFrom":sQuery(id+"F5.wireOp",EDGE,"E31.0.15.3")}),-1.0]])]});
            var Q279;
            Q279=makeQuery(id+"F5.imprint","IMPRINT",FACE,{"disambiguationData":[TD([[makeQuery(id+"F5.imprint","IMPRINT",EDGE,{"derivedFrom":sQuery(id+"F5.wireOp",EDGE,"E31.1.7.0")}),-1.0]])]});
            var Q280;
            Q280=makeQuery(id+"F5.imprint","IMPRINT",FACE,{"disambiguationData":[TD([[makeQuery(id+"F5.imprint","IMPRINT",EDGE,{"derivedFrom":sQuery(id+"F5.wireOp",EDGE,"E31.1.15.0")}),-1.0]])]});
            var Q281;
            Q281=makeQuery(id+"F5.imprint","IMPRINT",FACE,{"disambiguationData":[TD([[makeQuery(id+"F5.imprint","IMPRINT",EDGE,{"derivedFrom":sQuery(id+"F5.wireOp",EDGE,"E31.2.6.3")}),-1.0]])]});
            var Q282;
            Q282=makeQuery(id+"F5.imprint","IMPRINT",FACE,{"disambiguationData":[TD([[makeQuery(id+"F5.imprint","IMPRINT",EDGE,{"derivedFrom":sQuery(id+"F5.wireOp",EDGE,"E31.8.11.3")}),-1.0]])]});
            var Q283;
            Q283=makeQuery(id+"F5.imprint","IMPRINT",FACE,{"disambiguationData":[TD([[makeQuery(id+"F5.imprint","IMPRINT",EDGE,{"derivedFrom":sQuery(id+"F5.wireOp",EDGE,"E31.9.6.0")}),-1.0]])]});
            var Q284;
            Q284=makeQuery(id+"F5.imprint","IMPRINT",FACE,{"disambiguationData":[TD([[makeQuery(id+"F5.imprint","IMPRINT",EDGE,{"derivedFrom":sQuery(id+"F5.wireOp",EDGE,"E31.6.12.3")}),-1.0]])]});
            var Q285;
            Q285=makeQuery(id+"F5.imprint","IMPRINT",FACE,{"disambiguationData":[TD([[makeQuery(id+"F5.imprint","IMPRINT",EDGE,{"derivedFrom":sQuery(id+"F5.wireOp",EDGE,"E31.7.4.0")}),-1.0]])]});
            var Q286;
            Q286=makeQuery(id+"F5.imprint","IMPRINT",FACE,{"disambiguationData":[TD([[makeQuery(id+"F5.imprint","IMPRINT",EDGE,{"derivedFrom":sQuery(id+"F5.wireOp",EDGE,"E31.7.12.0")}),-1.0]])]});
            var Q287;
            Q287=makeQuery(id+"F5.imprint","IMPRINT",FACE,{"disambiguationData":[TD([[makeQuery(id+"F5.imprint","IMPRINT",EDGE,{"derivedFrom":sQuery(id+"F5.wireOp",EDGE,"E31.8.3.3")}),-1.0]])]});
            var Q288;
            Q288=makeQuery(id+"F5.imprint","IMPRINT",FACE,{"disambiguationData":[TD([[makeQuery(id+"F5.imprint","IMPRINT",EDGE,{"derivedFrom":sQuery(id+"F5.wireOp",EDGE,"E31.4.13.3")}),-1.0]])]});
            var Q289;
            Q289=makeQuery(id+"F5.imprint","IMPRINT",FACE,{"disambiguationData":[TD([[makeQuery(id+"F5.imprint","IMPRINT",EDGE,{"derivedFrom":sQuery(id+"F5.wireOp",EDGE,"E31.5.5.0")}),-1.0]])]});
            var Q290;
            Q290=makeQuery(id+"F5.imprint","IMPRINT",FACE,{"disambiguationData":[TD([[makeQuery(id+"F5.imprint","IMPRINT",EDGE,{"derivedFrom":sQuery(id+"F5.wireOp",EDGE,"E31.5.13.0")}),-1.0]])]});
            var Q291;
            Q291=makeQuery(id+"F5.imprint","IMPRINT",FACE,{"disambiguationData":[TD([[makeQuery(id+"F5.imprint","IMPRINT",EDGE,{"derivedFrom":sQuery(id+"F5.wireOp",EDGE,"E31.6.4.3")}),-1.0]])]});
            var Q292;
            Q292=makeQuery(id+"F5.imprint","IMPRINT",FACE,{"disambiguationData":[TD([[makeQuery(id+"F5.imprint","IMPRINT",EDGE,{"derivedFrom":sQuery(id+"F5.wireOp",EDGE,"E31.2.14.3")}),-1.0]])]});
            var Q293;
            Q293=makeQuery(id+"F5.imprint","IMPRINT",FACE,{"disambiguationData":[TD([[makeQuery(id+"F5.imprint","IMPRINT",EDGE,{"derivedFrom":sQuery(id+"F5.wireOp",EDGE,"E31.3.6.0")}),-1.0]])]});
            var Q294;
            Q294=makeQuery(id+"F5.imprint","IMPRINT",FACE,{"disambiguationData":[TD([[makeQuery(id+"F5.imprint","IMPRINT",EDGE,{"derivedFrom":sQuery(id+"F5.wireOp",EDGE,"E31.3.14.0")}),-1.0]])]});
            var Q295;
            Q295=makeQuery(id+"F5.imprint","IMPRINT",FACE,{"disambiguationData":[TD([[makeQuery(id+"F5.imprint","IMPRINT",EDGE,{"derivedFrom":sQuery(id+"F5.wireOp",EDGE,"E31.4.5.3")}),-1.0]])]});
            var Q296;
            Q296=makeQuery(id+"F5.imprint","IMPRINT",FACE,{"disambiguationData":[TD([[makeQuery(id+"F5.imprint","IMPRINT",EDGE,{"derivedFrom":sQuery(id+"F5.wireOp",EDGE,"E31.0.6.0")}),-1.0]])]});
            var Q297;
            Q297=makeQuery(id+"F5.imprint","IMPRINT",FACE,{"disambiguationData":[TD([[makeQuery(id+"F5.imprint","IMPRINT",EDGE,{"derivedFrom":sQuery(id+"F5.wireOp",EDGE,"E31.0.5.3")}),-1.0]])]});
            var Q298;
            Q298=makeQuery(id+"F5.imprint","IMPRINT",FACE,{"disambiguationData":[TD([[makeQuery(id+"F5.imprint","IMPRINT",EDGE,{"derivedFrom":sQuery(id+"F5.wireOp",EDGE,"E31.0.4.3")}),-1.0]])]});
            var Q299;
            Q299=makeQuery(id+"F5.imprint","IMPRINT",FACE,{"disambiguationData":[TD([[makeQuery(id+"F5.imprint","IMPRINT",EDGE,{"derivedFrom":sQuery(id+"F5.wireOp",EDGE,"E31.0.5.0")}),-1.0]])]});
            var Q300;
            Q300=makeQuery(id+"F5.imprint","IMPRINT",FACE,{"disambiguationData":[TD([[makeQuery(id+"F5.imprint","IMPRINT",EDGE,{"derivedFrom":sQuery(id+"F5.wireOp",EDGE,"E31.0.4.0")}),-1.0]])]});
            var Q301;
            Q301=makeQuery(id+"F5.imprint","IMPRINT",FACE,{"disambiguationData":[TD([[makeQuery(id+"F5.imprint","IMPRINT",EDGE,{"derivedFrom":sQuery(id+"F5.wireOp",EDGE,"E31.0.3.3")}),-1.0]])]});
            var Q302;
            Q302=makeQuery(id+"F5.imprint","IMPRINT",FACE,{"disambiguationData":[TD([[makeQuery(id+"F5.imprint","IMPRINT",EDGE,{"derivedFrom":sQuery(id+"F5.wireOp",EDGE,"E31.0.3.0")}),-1.0]])]});
            var Q303;
            Q303=makeQuery(id+"F5.imprint","IMPRINT",FACE,{"disambiguationData":[TD([[makeQuery(id+"F5.imprint","IMPRINT",EDGE,{"derivedFrom":sQuery(id+"F5.wireOp",EDGE,"E31.0.2.3")}),-1.0]])]});
            var Q304;
            Q304=makeQuery(id+"F5.imprint","IMPRINT",FACE,{"disambiguationData":[TD([[makeQuery(id+"F5.imprint","IMPRINT",EDGE,{"derivedFrom":sQuery(id+"F5.wireOp",EDGE,"E31.0.2.0")}),-1.0]])]});
            var Q305;
            Q305=makeQuery(id+"F5.imprint","IMPRINT",FACE,{"disambiguationData":[TD([[makeQuery(id+"F5.imprint","IMPRINT",EDGE,{"derivedFrom":sQuery(id+"F5.wireOp",EDGE,"E31.0.1.3")}),-1.0]])]});
            var Q306;
            Q306=makeQuery(id+"F5.imprint","IMPRINT",FACE,{"disambiguationData":[TD([[makeQuery(id+"F5.imprint","IMPRINT",EDGE,{"derivedFrom":sQuery(id+"F5.wireOp",EDGE,"E31.0.1.0")}),-1.0]])]});
            var Q307;
            Q307=makeQuery(id+"F5.imprint","IMPRINT",FACE,{"disambiguationData":[TD([[makeQuery(id+"F5.imprint","IMPRINT",EDGE,{"derivedFrom":sQuery(id+"F5.wireOp",EDGE,"E31.0.7.0")}),-1.0]])]});
            var Q308;
            Q308=makeQuery(id+"F5.imprint","IMPRINT",FACE,{"disambiguationData":[TD([[makeQuery(id+"F5.imprint","IMPRINT",EDGE,{"derivedFrom":sQuery(id+"F5.wireOp",EDGE,"E31.0.6.3")}),-1.0]])]});
            var Q309;
            Q309=makeQuery(id+"F5.imprint","IMPRINT",FACE,{"disambiguationData":[TD([[makeQuery(id+"F5.imprint","IMPRINT",EDGE,{"derivedFrom":sQuery(id+"F5.wireOp",EDGE,"E31.0.7.3")}),-1.0]])]});
            var Q310;
            Q310=makeQuery(id+"F5.imprint","IMPRINT",FACE,{"disambiguationData":[TD([[makeQuery(id+"F5.imprint","IMPRINT",EDGE,{"derivedFrom":sQuery(id+"F5.wireOp",EDGE,"E31.4.8.3")}),-1.0]])]});
            var Q311;
            Q311=makeQuery(id+"F5.imprint","IMPRINT",FACE,{"disambiguationData":[TD([[makeQuery(id+"F5.imprint","IMPRINT",EDGE,{"derivedFrom":sQuery(id+"F5.wireOp",EDGE,"E30.0")}),-1.0]])]});
            var Q312;
            Q312=makeQuery(id+"F5.imprint","IMPRINT",FACE,{"disambiguationData":[TD([[makeQuery(id+"F5.imprint","IMPRINT",EDGE,{"derivedFrom":sQuery(id+"F5.wireOp",EDGE,"E28.0")}),-1.0]])]});
            extrude(context, id + "F6", {"entities" : qUnion([Q0, Q1, Q2, Q3, Q4, Q5, Q6, Q7, Q8, Q9, Q10, Q11, Q12, Q13, Q14, Q15, Q16, Q17, Q18, Q19, Q20, Q21, Q22, Q23, Q24, Q25, Q26, Q27, Q28, Q29, Q30, Q31, Q32, Q33, Q34, Q35, Q36, Q37, Q38, Q39, Q40, Q41, Q42, Q43, Q44, Q45, Q46, Q47, Q48, Q49, Q50, Q51, Q52, Q53, Q54, Q55, Q56, Q57, Q58, Q59, Q60, Q61, Q62, Q63, Q64, Q65, Q66, Q67, Q68, Q69, Q70, Q71, Q72, Q73, Q74, Q75, Q76, Q77, Q78, Q79, Q80, Q81, Q82, Q83, Q84, Q85, Q86, Q87, Q88, Q89, Q90, Q91, Q92, Q93, Q94, Q95, Q96, Q97, Q98, Q99, Q100, Q101, Q102, Q103, Q104, Q105, Q106, Q107, Q108, Q109, Q110, Q111, Q112, Q113, Q114, Q115, Q116, Q117, Q118, Q119, Q120, Q121, Q122, Q123, Q124, Q125, Q126, Q127, Q128, Q129, Q130, Q131, Q132, Q133, Q134, Q135, Q136, Q137, Q138, Q139, Q140, Q141, Q142, Q143, Q144, Q145, Q146, Q147, Q148, Q149, Q150, Q151, Q152, Q153, Q154, Q155, Q156, Q157, Q158, Q159, Q160, Q161, Q162, Q163, Q164, Q165, Q166, Q167, Q168, Q169, Q170, Q171, Q172, Q173, Q174, Q175, Q176, Q177, Q178, Q179, Q180, Q181, Q182, Q183, Q184, Q185, Q186, Q187, Q188, Q189, Q190, Q191, Q192, Q193, Q194, Q195, Q196, Q197, Q198, Q199, Q200, Q201, Q202, Q203, Q204, Q205, Q206, Q207, Q208, Q209, Q210, Q211, Q212, Q213, Q214, Q215, Q216, Q217, Q218, Q219, Q220, Q221, Q222, Q223, Q224, Q225, Q226, Q227, Q228, Q229, Q230, Q231, Q232, Q233, Q234, Q235, Q236, Q237, Q238, Q239, Q240, Q241, Q242, Q243, Q244, Q245, Q246, Q247, Q248, Q249, Q250, Q251, Q252, Q253, Q254, Q255, Q256, Q257, Q258, Q259, Q260, Q261, Q262, Q263, Q264, Q265, Q266, Q267, Q268, Q269, Q270, Q271, Q272, Q273, Q274, Q275, Q276, Q277, Q278, Q279, Q280, Q281, Q282, Q283, Q284, Q285, Q286, Q287, Q288, Q289, Q290, Q291, Q292, Q293, Q294, Q295, Q296, Q297, Q298, Q299, Q300, Q301, Q302, Q303, Q304, Q305, Q306, Q307, Q308, Q309, Q310, Q311, Q312]), "operationType" : NewBodyOperationType.REMOVE, "oppositeDirection" : true, "depth" : 3 * mm});
        }
    });
